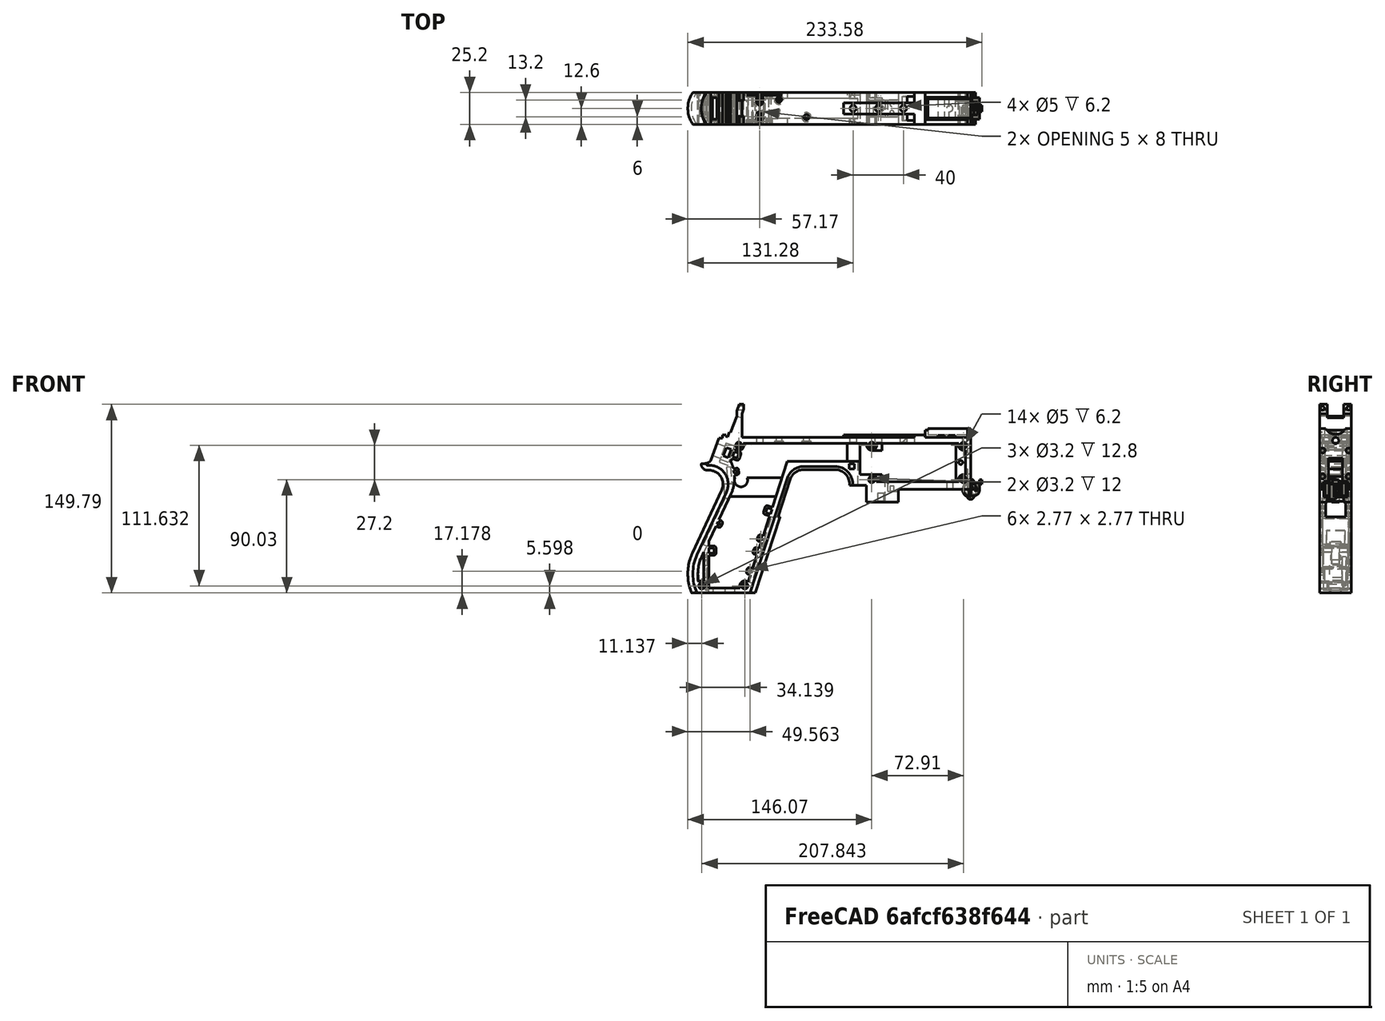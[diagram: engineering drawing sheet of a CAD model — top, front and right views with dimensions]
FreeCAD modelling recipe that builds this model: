
FCSTD DOCUMENT  (FreeCAD 1.0R39319 (Git))
Label: PICON-OF_ver_46
License: All rights reserved
LicenseURL: https://en.wikipedia.org/wiki/All_rights_reserved
objects: Sketcher::SketchObject×119, Part::Extrusion×62, Part::Cut×48, PartDesign::Pad×29, PartDesign::Pocket×18, PartDesign::Chamfer×15, PartDesign::Body×10, PartDesign::Fillet×6, Part::MultiFuse×4, PartDesign::SubtractivePipe×4, Part::Part2DObjectPython×4, PartDesign::SubtractiveLoft×4, PartDesign::Plane×2, PartDesign::SubShapeBinder×2, Part::Sweep×1, PartDesign::ShapeBinder×1, Mesh::Feature×1
note: 600 computed .brp shape members not serialized (recipe doc carries the construction recipe); baked Part::Feature solids carry a one-line shape summary decoded from their .brp

FEATURE [Sketcher::SketchObject] Sketch  label="corpo principale"
  ArcFitTolerance = 1e-06
  AttacherType = Attacher::AttachEngine3D
  AttachmentSupport = -> [XZ_Plane]
  FullyConstrained = true
  MakeInternals = false
  MapMode = 5
  Placement = pos=(0,0,0) rot=(1,0,0;1.5708rad)
  sketch-geometry (65):
    g0: LineSegment StartX=0 StartY=0 StartZ=0 EndX=-57.2 EndY=0 EndZ=0
    g1: LineSegment StartX=-57.2 StartY=0 StartZ=0 EndX=-57.2 EndY=-10.4 EndZ=0
    g2: LineSegment StartX=-57.2 StartY=-10.4 StartZ=0 EndX=-82.8 EndY=-10.4 EndZ=0
    g3: LineSegment StartX=-82.8 StartY=-10.4 StartZ=0 EndX=-82.8 EndY=3.2 EndZ=0
    g4: LineSegment StartX=-82.8 StartY=3.2 StartZ=0 EndX=-93.6 EndY=3.2 EndZ=0
    g5: LineSegment StartX=-93.6 StartY=3.2 StartZ=0 EndX=-93.6 EndY=4 EndZ=0
    g6: LineSegment StartX=-107.6 StartY=18 StartZ=0 EndX=-132.428 EndY=18 EndZ=0
    g7: LineSegment StartX=-145.743 StartY=8.32624 StartZ=0 EndX=-175.232 EndY=-82.4316 EndZ=0
    g8: LineSegment StartX=-175.232 StartY=-82.4316 StartZ=0 EndX=-217.232 EndY=-82.4316 EndZ=0
    g9: LineSegment StartX=-217.232 StartY=-52.1862 StartZ=0 EndX=-193.988 EndY=-2.33927 EndZ=0
    g10: LineSegment StartX=-206.196 StartY=23.0857 StartZ=0 EndX=-199.861 EndY=40.4914 EndZ=0
    g11: LineSegment StartX=-199.861 StartY=40.4914 StartZ=0 EndX=-197.061 EndY=40.4914 EndZ=0
    g12: LineSegment StartX=-197.061 StartY=40.4914 StartZ=0 EndX=-197.061 EndY=42.8914 EndZ=0
    g13: LineSegment StartX=-197.061 StartY=42.8914 StartZ=0 EndX=-194.261 EndY=42.8914 EndZ=0
    g14: LineSegment StartX=-194.261 StartY=42.8914 StartZ=0 EndX=-194.535 EndY=42.1397 EndZ=0
    g15: LineSegment StartX=-194.535 StartY=42.1397 StartZ=0 EndX=-193.031 EndY=41.5924 EndZ=0
    g16: LineSegment StartX=-193.031 StartY=41.5924 StartZ=0 EndX=-191.663 EndY=45.3512 EndZ=0
    g17: LineSegment StartX=-191.663 StartY=45.3512 StartZ=0 EndX=-190.536 EndY=44.9408 EndZ=0
    g18: LineSegment StartX=-190.536 StartY=44.9408 StartZ=0 EndX=-185.747 EndY=58.0965 EndZ=0
    g19: LineSegment StartX=-185.747 StartY=58.0965 StartZ=0 EndX=-185.747 EndY=62.0965 EndZ=0
    g20: LineSegment StartX=-185.747 StartY=62.0965 StartZ=0 EndX=-183.832 EndY=67.3588 EndZ=0
    g21: LineSegment StartX=-183.832 StartY=67.3588 StartZ=0 EndX=-180.232 EndY=67.3588 EndZ=0
    g22: LineSegment StartX=-180.232 StartY=67.3588 StartZ=0 EndX=-180.232 EndY=63.7588 EndZ=0
    g23: LineSegment StartX=-180.232 StartY=63.7588 StartZ=0 EndX=-181.6 EndY=60 EndZ=0
    g24: LineSegment StartX=-181.6 StartY=60 StartZ=0 EndX=-181.6 EndY=41.2 EndZ=0
    g25: LineSegment StartX=-181.6 StartY=41.2 StartZ=0 EndX=-100.8 EndY=41.2 EndZ=0
    g26: LineSegment StartX=-36 StartY=43.2 StartZ=0 EndX=-36 EndY=41.2 EndZ=0
    g27: LineSegment StartX=0 StartY=48 StartZ=0 EndX=0 EndY=0 EndZ=0
    g28: LineSegment StartX=-209.901 StartY=19.85 StartZ=0 EndX=-209.901 EndY=20.1 EndZ=0
    g29: LineSegment StartX=-208.001 StartY=22 StartZ=0 EndX=-207.747 EndY=22 EndZ=0
    g30: LineSegment StartX=-207.583 StartY=19 StartZ=0 EndX=-209.051 EndY=19 EndZ=0
    g31: ArcOfCircle CenterX=-208.001 CenterY=20.1 CenterZ=0 NormalX=0 NormalY=0 NormalZ=1 AngleXU=0 Radius=1.9 StartAngle=1.5708 EndAngle=3.14159
    g32: GeomPoint [constr] X=-209.901 Y=22 Z=0
    g33: ArcOfCircle CenterX=-209.051 CenterY=19.85 CenterZ=0 NormalX=0 NormalY=0 NormalZ=1 AngleXU=0 Radius=0.85 StartAngle=3.14159 EndAngle=4.71239
    g34: GeomPoint [constr] X=-209.901 Y=19 Z=0
    g35: ArcOfCircle CenterX=-207.747 CenterY=23.65 CenterZ=0 NormalX=0 NormalY=0 NormalZ=1 AngleXU=0 Radius=1.65 StartAngle=4.71239 EndAngle=5.93412
    g36: GeomPoint [constr] X=-206.591 Y=22 Z=0
    g37: LineSegment StartX=-4 StartY=6 StartZ=0 EndX=-4 EndY=36.4 EndZ=0
    g38: LineSegment StartX=-4 StartY=36.4 StartZ=0 EndX=-185.2 EndY=36.4 EndZ=0
    g39: LineSegment StartX=-185.2 StartY=36.4 StartZ=0 EndX=-190.441 EndY=22 EndZ=0
    g40: LineSegment StartX=-214.575 StartY=-78.4316 StartZ=0 EndX=-178.142 EndY=-78.4316 EndZ=0
    g41: LineSegment StartX=-178.142 StartY=-78.4316 StartZ=0 EndX=-145.51 EndY=22 EndZ=0
    g42: LineSegment StartX=-145.51 StartY=22 StartZ=0 EndX=-87.91 EndY=22 EndZ=0
    g43: LineSegment StartX=-87.91 StartY=22 StartZ=0 EndX=-87.91 EndY=11.6 EndZ=0
    g44: LineSegment StartX=-87.91 StartY=11.6 StartZ=0 EndX=-80.11 EndY=11.6 EndZ=0
    g45: LineSegment StartX=-80.11 StartY=11.6 StartZ=0 EndX=-80.11 EndY=6 EndZ=0
    g46: LineSegment StartX=-80.11 StartY=6 StartZ=0 EndX=-4 EndY=6 EndZ=0
    g47: LineSegment StartX=-190.363 StartY=-4.02975 StartZ=0 EndX=-213.607 EndY=-53.8767 EndZ=0
    g48: ArcOfCircle CenterX=-132.428 CenterY=4 CenterZ=0 NormalX=0 NormalY=0 NormalZ=1 AngleXU=0 Radius=14 StartAngle=1.5708 EndAngle=2.82743
    g49: GeomPoint [constr] X=-142.6 Y=18 Z=0
    g50: ArcOfCircle CenterX=-107.6 CenterY=4 CenterZ=0 NormalX=0 NormalY=0 NormalZ=1 AngleXU=0 Radius=14 StartAngle=0 EndAngle=1.5708
    g51: GeomPoint [constr] X=-93.6 Y=18 Z=0
    g52: ArcOfCircle CenterX=-184.801 CenterY=-67.3089 CenterZ=0 NormalX=0 NormalY=0 NormalZ=1 AngleXU=0 Radius=35.7833 StartAngle=2.70526 EndAngle=3.57792
    g53: ArcOfCircle CenterX=-207.583 CenterY=4 CenterZ=0 NormalX=0 NormalY=0 NormalZ=1 AngleXU=0 Radius=15 StartAngle=5.84685 EndAngle=7.85398
    g54: LineSegment [constr] StartX=-213.607 StartY=-53.8767 StartZ=0 EndX=-217.232 EndY=-52.1862 EndZ=0
    g55: ArcOfCircle CenterX=-184.801 CenterY=-67.3089 CenterZ=0 NormalX=0 NormalY=0 NormalZ=1 AngleXU=0 Radius=31.7833 StartAngle=2.70526 EndAngle=3.49911
    g56: ArcOfCircle CenterX=-218.095 CenterY=8.90192 CenterZ=0 NormalX=0 NormalY=0 NormalZ=1 AngleXU=0 Radius=30.5989 StartAngle=5.84685 EndAngle=6.72553
    g57: LineSegment StartX=-44.6 StartY=43.2 StartZ=0 EndX=-36 EndY=43.2 EndZ=0
    g58: LineSegment StartX=-100.8 StartY=41.2 StartZ=0 EndX=-44.6 EndY=41.2 EndZ=0
    g59: LineSegment StartX=-44.6 StartY=41.2 StartZ=0 EndX=-44.6 EndY=43.2 EndZ=0
    g60: LineSegment StartX=-2.4 StartY=48 StartZ=0 EndX=0 EndY=48 EndZ=0
    g61: LineSegment StartX=-36 StartY=41.2 StartZ=0 EndX=-2.4 EndY=41.2 EndZ=0
    g62: LineSegment StartX=-2.4 StartY=41.2 StartZ=0 EndX=-2.4 EndY=48 EndZ=0
    g63: LineSegment [constr] StartX=-181.6 StartY=36.4 StartZ=0 EndX=-152.209 EndY=36.4 EndZ=0
    g64: LineSegment [constr] StartX=-181.6 StartY=36.4 StartZ=0 EndX=-130.41 EndY=36.4 EndZ=0
  constraints (183):
    c: Coincident(g-1,g0)
    c: PointOnObject(g0,g-1)
    c: Coincident(g0,g1)
    c: Vertical(g1)
    c: Coincident(g1,g2)
    c: Horizontal(g2)
    c: Coincident(g2,g3)
    c: Vertical(g3)
    c: Coincident(g3,g4)
    c: Coincident(g4,g5)
    c: Vertical(g5)
    c: Horizontal(g6)
    c: Coincident(g7,g8)
    c: Horizontal(g8)
    c: Coincident(g10,g11)
    c: Horizontal(g11)
    c: Coincident(g11,g12)
    c: Vertical(g12)
    c: Coincident(g12,g13)
    c: Horizontal(g13)
    c: Coincident(g13,g14)
    c: Coincident(g14,g15)
    c: Coincident(g15,g16)
    c: Coincident(g16,g17)
    c: Coincident(g17,g18)
    c: Coincident(g18,g19)
    c: Vertical(g19)
    c: Coincident(g19,g20)
    c: Coincident(g20,g21)
    c: Horizontal(g21)
    c: Coincident(g21,g22)
    c: Vertical(g22)
    c: Coincident(g22,g23)
    c: Coincident(g23,g24)
    c: Vertical(g24)
    c: Coincident(g24,g25)
    c: Horizontal(g25)
    c: Coincident(g57,g26)
    c: Vertical(g26)
    c: Coincident(g26,g61)
    c: PointOnObject(g60,g-2)
    c: Coincident(g60,g27)
    c: Coincident(g27,g0)
    c: DistanceY(g27,g27) = 48
    c: DistanceY(g1,g1) = 10.4
    c: DistanceX(g0,g0) = 57.2
    c: DistanceX(g2,g2) = 25.6
    c: Horizontal(g4)
    c: DistanceY(g3,g3) = 13.6
    c: DistanceX(g4,g4) = 10.8
    c: DistanceY(g5,g51) = 14.8
    c: DistanceX(g49,g51) = 49
    c: Distance(g7,g49) = 105.6
    c: DistanceX(g61,g60) = 36
    c: DistanceX(g25,g25) = 80.8
    c: DistanceY(g24,g24) = 18.8
    c: DistanceY(g22,g22) = 3.6
    c: Distance(g23) = 4
    c: Angle(g-1,g23) = 1.22173
    c: DistanceX(g21,g21) = 3.6
    c: Distance(g20) = 5.6
    c: Angle(g-1,g20) = 1.22173
    c: DistanceY(g19,g19) = 4
    c: Distance(g18) = 14
    c: Angle(g-1,g18) = 1.22173
    c: Distance(g17) = 1.2
    c: Distance(g16) = 4
    c: Angle(g16) = 1.22173
    c: Perpendicular(g18,g17)
    c: Distance(g15) = 1.6
    c: Perpendicular(g16,g15)
    c: Distance(g14) = 0.8
    c: DistanceX(g13,g13) = 2.8
    c: Perpendicular(g15,g14)
    c: DistanceY(g12,g12) = 2.4
    c: DistanceX(g11,g11) = 2.8
    c: Distance(g9) = 55
    c: Angle(g9,g-1) = 2.00713
    c: Horizontal(g29)
    c: Vertical(g28)
    c: Horizontal(g30)
    c: PointOnObject(g32,g29)
    c: PointOnObject(g32,g28)
    c: Tangent(g29,g31) = 1.5708
    c: Tangent(g28,g31) = 1.5708
    c: PointOnObject(g34,g28)
    c: PointOnObject(g34,g30)
    c: Tangent(g28,g33) = 1.5708
    c: Tangent(g30,g33) = 1.5708
    c: PointOnObject(g36,g29)
    c: PointOnObject(g36,g10)
    c: Tangent(g29,g35) = -1.5708
    c: Tangent(g10,g35) = -1.5708
    c: Angle(g-1,g10) = 1.22173
    c: Radius(g35) = 1.65
    c: Vertical(g37)
    c: Coincident(g37,g38)
    c: Horizontal(g38)
    c: Coincident(g38,g39)
    c: Horizontal(g40)
    c: Coincident(g40,g41)
    c: Coincident(g41,g42)
    c: Horizontal(g42)
    c: Coincident(g42,g43)
    c: Vertical(g43)
    c: Coincident(g43,g44)
    c: Horizontal(g44)
    c: Coincident(g44,g45)
    c: Vertical(g45)
    c: Coincident(g45,g46)
    c: Coincident(g46,g37)
    c: Horizontal(g46)
    c: DistanceY(g0,g37) = 6
    c: DistanceX(g37,g0) = 4
    c: DistanceY(g37,g25) = 4.8
    c: DistanceX(g38,g38) = 181.2
    c: DistanceX(g42,g42) = 57.6
    c: DistanceY(g49,g41) = 4
    c: DistanceX(g41,g49) = 2.91
    c: DistanceY(g43,g43) = 10.4
    c: DistanceX(g44,g44) = 7.8
    c: DistanceY(g7,g40) = 4
    c: Distance(g47) = 55
    c: Angle(g-1,g39) = 1.22173
    c: PointOnObject(g49,g7)
    c: PointOnObject(g49,g6)
    c: Tangent(g7,g48) = -1.5708
    c: Tangent(g6,g48) = -1.5708
    c: PointOnObject(g51,g5)
    c: PointOnObject(g51,g6)
    c: Tangent(g5,g50) = -1.5708
    c: Tangent(g6,g50) = -1.5708
    c: Radius(g50) = 14
    c: Radius(g48) = 14
    c: DistanceX(g8,g8) = 42
    c: Angle(g7,g-1) = 1.88496
    c: Parallel(g41,g7)
    c: Parallel(g47,g9)
    c: Coincident(g52,g8)
    c: Tangent(g52,g9) = 1.5708
    c: DistanceX(g9,g8) = 0
    c: Tangent(g53,g9) = -1.5708
    c: Tangent(g53,g30) = -1.5708
    c: Diameter(g53) = 30
    c: DistanceY(g53,g0) = -4
    c: Coincident(g54,g47)
    c: Distance(g54) = 4
    c: Coincident(g54,g9)
    c: Coincident(g55,g40)
    c: Tangent(g55,g47) = -1.5708
    c: Coincident(g52,g55)
    c: Coincident(g56,g39)
    c: Tangent(g56,g47) = 1.5708
    c: Horizontal(g57)
    c: DistanceX(g57,g57) = 8.6
    c: Coincident(g58,g25)
    c: Horizontal(g58)
    c: Coincident(g59,g58)
    c: Vertical(g59)
    c: DistanceY(g58,g57) = 2
    c: DistanceX(g58,g58) = 56.2
    c: Coincident(g59,g57)
    c: DistanceY(g41,g36) = 0
    c: DistanceY(g36,g39) = 0
    c: DistanceY(g28,g28) = 0.25
    c: DistanceX(g30,g36) = 2.46
    c: DistanceX(g28,g29) = 1.9
    c: Coincident(g62,g60)
    c: Horizontal(g60)
    c: DistanceX(g62,g27) = 2.4
    c: Coincident(g61,g62)
    c: DistanceY(g26,g26) = 2
    c: Vertical(g62)
    c: DistanceY(g61,g60) = 6.8
    c: Horizontal(g61)
    c: Distance(g63) = 29.391
    c: PointOnObject(g63,g38)
    c: PointOnObject(g63,g38)
    c: Distance(g64) = 51.19
    c: PointOnObject(g64,g38)
    c: PointOnObject(g64,g38)
    c: DistanceX(g24,g63) = 0
    c: DistanceX(g24,g64) = 0
FEATURE [Part::Extrusion] Extrude  label="Extrude corpo principale"
  Base = -> Sketch
  Dir = (0,-1,2e-16)
  DirMode = 2
  FaceMakerClass = Part::FaceMakerBullseye
  FaceMakerMode = 3
  LengthFwd = 25.2
  LengthRev = 12.6
  Solid = true
  Symmetric = true
FEATURE [Sketcher::SketchObject] Sketch002  label="scavo grilletto"
  ArcFitTolerance = 1e-06
  AttachmentSupport = -> [XZ_Plane]
  ExternalGeometry = -> [Sketch]
  FullyConstrained = true
  MakeInternals = false
  MapMode = 5
  Placement = pos=(0,0,0) rot=(1,0,0;1.5708rad)
  sketch-geometry (4):
    g0: LineSegment StartX=-89.51 StartY=22 StartZ=0 EndX=-152.71 EndY=22 EndZ=0
    g1: LineSegment StartX=-152.71 StartY=22 StartZ=0 EndX=-167.006 EndY=-22 EndZ=0
    g2: LineSegment StartX=-167.006 StartY=-22 StartZ=0 EndX=-89.51 EndY=-22 EndZ=0
    g3: LineSegment StartX=-89.51 StartY=-22 StartZ=0 EndX=-89.51 EndY=22 EndZ=0
  constraints (12):
    c: Horizontal(g0)
    c: Coincident(g0,g1)
    c: Coincident(g1,g2)
    c: Horizontal(g2)
    c: Coincident(g2,g3)
    c: Coincident(g3,g0)
    c: Vertical(g3)
    c: Angle(g1,g0) = 1.88496
    c: DistanceY(g3,g3) = 44
    c: DistanceX(g0,g0) = 63.2
    c: DistanceX(g0,g-3) = 1.6
    c: DistanceY(g-3,g0) = 0
FEATURE [Sketcher::SketchObject] Sketch004  label="traiettoria arrotondamento impugnatura anteriore"
  ArcFitTolerance = 1e-06
  AttachmentSupport = -> [XZ_Plane]
  ExternalGeometry = -> [Sketch]
  FullyConstrained = true
  MakeInternals = false
  MapMode = 5
  Placement = pos=(0,0,0) rot=(1,0,0;1.5708rad)
  sketch-geometry (13):
    g0: LineSegment StartX=-175.232 StartY=-82.4316 StartZ=0 EndX=-145.743 EndY=8.32624 EndZ=0
    g1: LineSegment StartX=-93.6 StartY=3.2 StartZ=0 EndX=-93.6 EndY=4 EndZ=0
    g2: LineSegment StartX=-132.428 StartY=18 StartZ=0 EndX=-107.6 EndY=18 EndZ=0
    g3: ArcOfCircle CenterX=-132.428 CenterY=4 CenterZ=0 NormalX=0 NormalY=0 NormalZ=1 AngleXU=0 Radius=14 StartAngle=1.5708 EndAngle=2.82743
    g4: ArcOfCircle CenterX=-107.6 CenterY=4 CenterZ=0 NormalX=0 NormalY=0 NormalZ=1 AngleXU=0 Radius=14 StartAngle=0 EndAngle=1.5708
    g5: LineSegment StartX=-175.232 StartY=-82.4316 StartZ=0 EndX=-217.232 EndY=-82.4316 EndZ=0
    g6: LineSegment StartX=-217.232 StartY=-52.1862 StartZ=0 EndX=-193.988 EndY=-2.33927 EndZ=0
    g7: LineSegment StartX=-209.051 StartY=19 StartZ=0 EndX=-207.583 EndY=19 EndZ=0
    g8: LineSegment StartX=-209.901 StartY=20.1 StartZ=0 EndX=-209.901 EndY=19.85 EndZ=0
    g9: ArcOfCircle CenterX=-184.801 CenterY=-67.3089 CenterZ=0 NormalX=0 NormalY=0 NormalZ=1 AngleXU=0 Radius=35.7833 StartAngle=2.70526 EndAngle=3.57792
    g10: ArcOfCircle CenterX=-207.583 CenterY=4 CenterZ=0 NormalX=0 NormalY=0 NormalZ=1 AngleXU=0 Radius=15 StartAngle=5.84685 EndAngle=7.85398
    g11: ArcOfCircle CenterX=-209.051 CenterY=19.85 CenterZ=0 NormalX=0 NormalY=0 NormalZ=1 AngleXU=0 Radius=0.85 StartAngle=3.14159 EndAngle=4.71239
    g12: ArcOfCircle CenterX=-208.001 CenterY=20.1 CenterZ=0 NormalX=0 NormalY=0 NormalZ=1 AngleXU=0 Radius=1.9 StartAngle=1.5708 EndAngle=3.14159
  constraints (26):
    c: Coincident(g0,g-3)
    c: Coincident(g0,g-6)
    c: Coincident(g1,g-8)
    c: Coincident(g1,g-7)
    c: Coincident(g2,g-5)
    c: Coincident(g2,g-4)
    c: Coincident(g3,g2)
    c: Tangent(g3,g0) = 1.5708
    c: Coincident(g4,g1)
    c: Tangent(g4,g2) = 1.5708
    c: Coincident(g5,g0)
    c: Coincident(g5,g-9)
    c: Coincident(g6,g-12)
    c: Coincident(g6,g-11)
    c: Coincident(g7,g-15)
    c: Coincident(g7,g-14)
    c: Coincident(g8,g-16)
    c: Coincident(g8,g-17)
    c: Tangent(g9,g6) = 1.5708
    c: Coincident(g9,g5)
    c: Coincident(g10,g7)
    c: Tangent(g10,g6) = -1.5708
    c: Tangent(g11,g7) = -1.5708
    c: Coincident(g11,g8)
    c: Tangent(g12,g8) = -1.5708
    c: Coincident(g12,g-17)
FEATURE [PartDesign::Plane] DatumPlane  label="Piano per disegno arrotondamento impugnatura"
  AttachmentSupport = -> [Sketch]
  Length = 73.6581
  MapMode = 7
  Placement = pos=(-145.743,1.8e-15,8.32624) rot=(0.154555,0.154555,0.97582;1.59527rad)
  ResizeMode = 0
  Width = 303.511
FEATURE [Sketcher::SketchObject] Sketch005  label="forma arrotondamento impugnatura anteriore"
  ArcFitTolerance = 1e-06
  AttachmentSupport = -> [DatumPlane]
  FullyConstrained = true
  MakeInternals = false
  MapMode = 5
  Placement = pos=(-145.743,1.8e-15,8.32624) rot=(0.154555,0.154555,0.97582;1.59527rad)
  sketch-geometry (5):
    g0: GeomPoint [constr] X=0 Y=-4 Z=0
    g1: GeomPoint [constr] X=-12.6 Y=7.1e-15 Z=0
    g2: GeomPoint [constr] X=12.6 Y=4.97e-14 Z=0
    g3: LineSegment StartX=-12.6 StartY=7.1e-15 StartZ=0 EndX=12.6 EndY=4.97e-14 EndZ=0
    g4: ArcOfCircle CenterX=-3.88e-14 CenterY=17.845 CenterZ=0 NormalX=0 NormalY=0 NormalZ=1 AngleXU=0 Radius=21.845 StartAngle=4.09759 EndAngle=5.32718
  constraints (11):
    c: DistanceY(g0,g-1) = 4
    c: DistanceX(g-1,g0) = 0
    c: DistanceX(g1,g-1) = 12.6
    c: DistanceX(g-1,g2) = 12.6
    c: DistanceY(g-1,g2) = 0
    c: DistanceY(g-1,g1) = 0
    c: Coincident(g3,g1)
    c: Coincident(g3,g2)
    c: Coincident(g4,g1)
    c: Coincident(g4,g2)
    c: PointOnObject(g0,g4)
FEATURE [Part::Sweep] Sweep  label="Sweep impugnatura"
  Frenet = true
  Sections = -> [Sketch005]
  Solid = true
  Spine = -> Sketch [Edge32,Edge33,Edge34,Edge35,Edge36,Edge37,Edge38,Edge39,Edge40,Edge41,Edge42,Edge43,Edge44]
  Transition = 1
FEATURE [Sketcher::SketchObject] Sketch008  label="buchi e pulizie varie"
  ArcFitTolerance = 1e-06
  AttachmentSupport = -> [XZ_Plane]
  ExternalGeometry = -> [Sketch]
  FullyConstrained = true
  MakeInternals = false
  MapMode = 5
  Placement = pos=(0,0,0) rot=(1,0,0;1.5708rad)
  sketch-geometry (26):
    g0: LineSegment StartX=-96.278 StartY=20.155 StartZ=0 EndX=-92.278 EndY=20.155 EndZ=0
    g1: LineSegment StartX=-92.278 StartY=20.155 StartZ=0 EndX=-92.278 EndY=16.155 EndZ=0
    g2: LineSegment StartX=-92.278 StartY=16.155 StartZ=0 EndX=-96.278 EndY=16.155 EndZ=0
    g3: LineSegment StartX=-96.278 StartY=16.155 StartZ=0 EndX=-96.278 EndY=20.155 EndZ=0
    g4: LineSegment StartX=-222.232 StartY=-82.4316 StartZ=0 EndX=-170.232 EndY=-82.4316 EndZ=0
    g5: LineSegment StartX=-170.232 StartY=-82.4316 StartZ=0 EndX=-170.232 EndY=-86.4316 EndZ=0
    g6: LineSegment StartX=-170.232 StartY=-86.4316 StartZ=0 EndX=-222.232 EndY=-86.4316 EndZ=0
    g7: LineSegment StartX=-222.232 StartY=-86.4316 StartZ=0 EndX=-222.232 EndY=-82.4316 EndZ=0
    g8: LineSegment StartX=-213.901 StartY=20.1 StartZ=0 EndX=-213.901 EndY=26 EndZ=0
    g9: LineSegment StartX=-213.901 StartY=26 StartZ=0 EndX=-206.196 EndY=26 EndZ=0
    g10: LineSegment StartX=-17.4 StartY=42.8 StartZ=0 EndX=-12.4 EndY=42.8 EndZ=0
    g11: LineSegment StartX=-12.4 StartY=42.8 StartZ=0 EndX=-12.4 EndY=41.2 EndZ=0
    g12: LineSegment StartX=-12.4 StartY=41.2 StartZ=0 EndX=-17.4 EndY=41.2 EndZ=0
    g13: LineSegment StartX=-17.4 StartY=41.2 StartZ=0 EndX=-17.4 EndY=42.8 EndZ=0
    g14: LineSegment StartX=-25.9 StartY=42.8 StartZ=0 EndX=-20.9 EndY=42.8 EndZ=0
    g15: LineSegment StartX=-20.9 StartY=42.8 StartZ=0 EndX=-20.9 EndY=41.2 EndZ=0
    g16: LineSegment StartX=-20.9 StartY=41.2 StartZ=0 EndX=-25.9 EndY=41.2 EndZ=0
    g17: LineSegment StartX=-25.9 StartY=41.2 StartZ=0 EndX=-25.9 EndY=42.8 EndZ=0
    g18: GeomPoint [constr] X=-206.196 Y=23.0857 Z=0
    g19: GeomPoint [constr] X=-213.901 Y=20.1 Z=0
    g20: BSplineCurve PolesCount=4 KnotsCount=2 Degree=3 IsPeriodic=0
    g21-g24: Circle [constr] x4 (B-spline internal-alignment scaffolding for g20; pole/knot coordinates omitted)
    g25: LineSegment StartX=-206.196 StartY=26 StartZ=0 EndX=-206.196 EndY=23.0857 EndZ=0
  constraints (73):
    c: Horizontal(g0)
    c: Coincident(g1,g0)
    c: Vertical(g1)
    c: Coincident(g2,g1)
    c: Horizontal(g2)
    c: Coincident(g3,g2)
    c: Coincident(g3,g0)
    c: Vertical(g3)
    c: DistanceX(g0,g-4) = 4.368
    c: DistanceY(g0,g-4) = 1.845
    c: DistanceY(g1,g1) = 4
    c: DistanceX(g2,g2) = 4
    c: Horizontal(g4)
    c: Coincident(g5,g4)
    c: Vertical(g5)
    c: Coincident(g6,g5)
    c: Horizontal(g6)
    c: Coincident(g7,g6)
    c: Coincident(g7,g4)
    c: Vertical(g7)
    c: DistanceY(g7,g7) = 4
    c: DistanceX(g4,g-5) = 5
    c: DistanceX(g-5,g4) = 5
    c: DistanceY(g4,g-5) = 0
    c: Coincident(g9,g8)
    c: Parallel(g9,g-6)
    c: DistanceX(g8,g-8) = 4
    c: Horizontal(g10)
    c: Coincident(g11,g10)
    c: Vertical(g11)
    c: Coincident(g12,g11)
    c: Horizontal(g12)
    c: Coincident(g13,g12)
    c: Coincident(g13,g10)
    c: Vertical(g13)
    c: Horizontal(g14)
    c: Coincident(g15,g14)
    c: Vertical(g15)
    c: Coincident(g16,g15)
    c: Horizontal(g16)
    c: Coincident(g17,g16)
    c: Coincident(g17,g14)
    c: Vertical(g17)
    c: DistanceY(g11,g10) = 1.6
    c: DistanceX(g10,g10) = 5
    c: DistanceY(g15,g14) = 1.6
    c: DistanceX(g14,g14) = 5
    c: DistanceX(g15,g12) = 3.5
    c: DistanceX(g11,g-9) = 10
    c: DistanceY(g-9,g11) = 0
    c: DistanceY(g-9,g15) = 0
    c: Perpendicular(g8,g9)
    c: DistanceY(g-7,g9) = 4
    c: DistanceY(g8,g-8) = 0
    c: InternalAlignment(g18,g20)
    c: InternalAlignment(g19,g20)
    c: InternalAlignment(g21,g20)
    c: Weight(g21) = 1
    c: InternalAlignment(g22,g20)
    c: Equal(g22,g21)
    c: InternalAlignment(g23,g20)
    c: Equal(g23,g21)
    c: InternalAlignment(g24,g20)
    c: Equal(g24,g21)
    c: Coincident(g18,g-12)
    c: Coincident(g19,g8)
    c: Coincident(g25,g9)
    c: Coincident(g25,g20)
    c: Vertical(g25)
    c: DistanceY(g20,g23) = 0
    c: DistanceY(g22,g18) = 2.26
    c: DistanceX(g22,g18) = 0.93
    c: DistanceX(g20,g23) = 2.9
FEATURE [Part::Extrusion] Extrude004  label="Extrude Buchi e pulizie varie"
  Base = -> Sketch008
  Dir = (0,-1,2e-16)
  DirMode = 2
  FaceMakerClass = Part::FaceMakerBullseye
  FaceMakerMode = 3
  LengthFwd = 25.2
  LengthRev = 0
  Solid = true
  Symmetric = true
FEATURE [Sketcher::SketchObject] Sketch009  label="rinforzi"
  ArcFitTolerance = 1e-06
  AttachmentSupport = -> [XZ_Plane]
  ExternalGeometry = -> [Sketch]
  FullyConstrained = true
  MakeInternals = false
  MapMode = 5
  Placement = pos=(0,0,0) rot=(1,0,0;1.5708rad)
  sketch-geometry (9):
    g0: LineSegment StartX=-87.91 StartY=22 StartZ=0 EndX=-87.91 EndY=36.4 EndZ=0
    g1: LineSegment StartX=-87.91 StartY=36.4 StartZ=0 EndX=-97.91 EndY=36.4 EndZ=0
    g2: LineSegment StartX=-97.91 StartY=36.4 StartZ=0 EndX=-97.91 EndY=22 EndZ=0
    g3: LineSegment StartX=-97.91 StartY=22 StartZ=0 EndX=-87.91 EndY=22 EndZ=0
    g4: LineSegment StartX=-149.713 StartY=9.06563 StartZ=0 EndX=-154.586 EndY=-5.93437 EndZ=0
    g5: LineSegment StartX=-154.586 StartY=-5.93437 StartZ=0 EndX=-191.863 EndY=-5.93437 EndZ=0
    g6: LineSegment StartX=-191.863 StartY=-5.93437 StartZ=0 EndX=-191.863 EndY=9.06563 EndZ=0
    g7: LineSegment StartX=-191.863 StartY=9.06563 StartZ=0 EndX=-149.713 EndY=9.06563 EndZ=0
    g8: LineSegment [constr] StartX=-145.51 StartY=22 StartZ=0 EndX=-149.713 EndY=9.06563 EndZ=0
  constraints (25):
    c: Vertical(g0)
    c: Coincident(g1,g0)
    c: Horizontal(g1)
    c: Coincident(g2,g1)
    c: Vertical(g2)
    c: Coincident(g3,g2)
    c: Coincident(g3,g0)
    c: Horizontal(g3)
    c: Coincident(g0,g-4)
    c: DistanceX(g3,g3) = 10
    c: DistanceY(g0,g-3) = 0
    c: Coincident(g5,g4)
    c: Horizontal(g5)
    c: Coincident(g6,g5)
    c: Vertical(g6)
    c: Coincident(g7,g6)
    c: Coincident(g7,g4)
    c: Horizontal(g7)
    c: Distance(g8) = 13.6
    c: Parallel(g-6,g8)
    c: Coincident(g-6,g8)
    c: Parallel(g4,g-6)
    c: DistanceY(g4,g4) = 15
    c: Coincident(g4,g8)
    c: DistanceX(g-5,g5) = -1.5
FEATURE [Part::Extrusion] Extrude001  label="Extrude scavo grilletto"
  Base = -> Sketch002
  Dir = (0,-1,2e-16)
  DirMode = 2
  FaceMakerClass = Part::FaceMakerBullseye
  FaceMakerMode = 3
  LengthFwd = 16
  LengthRev = 0
  Solid = true
  Symmetric = true
FEATURE [Part::Extrusion] Extrude005  label="Extrude Rinforzi"
  Base = -> Sketch009
  Dir = (0,-1,2e-16)
  DirMode = 2
  FaceMakerClass = Part::FaceMakerBullseye
  FaceMakerMode = 3
  LengthFwd = 2
  LengthRev = 0
  Placement = pos=(0,12.6,0) rot=(0,0,1;0rad)
  Solid = true
  Symmetric = false
FEATURE [PartDesign::ShapeBinder] CopyCut
  TraceSupport = false
FEATURE [PartDesign::Plane] DatumPlane001
  AttachmentSupport = -> [CopyCut]
  Length = 283.944
  MapMode = 5
  Placement = pos=(0,12.6,0) rot=(0,0.707107,0.707107;3.14159rad)
  ResizeMode = 0
  Width = 188.15
FEATURE [Sketcher::SketchObject] Sketch010  label="buco neopixel"
  ArcFitTolerance = 1e-06
  AttachmentSupport = -> [XZ_Plane]
  ExternalGeometry = -> [Sketch]
  FullyConstrained = true
  MakeInternals = false
  MapMode = 5
  Placement = pos=(0,0,0) rot=(1,0,0;1.5708rad)
  sketch-geometry (5):
    g0: LineSegment [constr] StartX=-199.861 StartY=40.4914 StartZ=0 EndX=-201.368 EndY=36.3521 EndZ=0
    g1: LineSegment StartX=-201.368 StartY=36.3521 StartZ=0 EndX=-204.932 EndY=26.5605 EndZ=0
    g2: LineSegment StartX=-201.368 StartY=36.3521 StartZ=0 EndX=-180.2 EndY=28.6477 EndZ=0
    g3: LineSegment StartX=-180.2 StartY=28.6477 StartZ=0 EndX=-183.764 EndY=18.8561 EndZ=0
    g4: LineSegment StartX=-183.764 StartY=18.8561 StartZ=0 EndX=-204.932 EndY=26.5605 EndZ=0
  constraints (14):
    c: Parallel(g0,g-3)
    c: Distance(g0) = 4.405
    c: Coincident(g0,g-3)
    c: Coincident(g2,g1)
    c: Coincident(g3,g2)
    c: Coincident(g4,g3)
    c: Coincident(g4,g1)
    c: Parallel(g1,g-3)
    c: Distance(g1) = 10.42
    c: Coincident(g1,g0)
    c: Parallel(g2,g4)
    c: Perpendicular(g1,g2)
    c: DistanceX(g-4,g2) = 5
    c: Parallel(g3,g1)
FEATURE [Part::Extrusion] Extrude006  label="Extrude buco neopixel"
  Base = -> Sketch010
  Dir = (0,-1,2e-16)
  DirMode = 2
  FaceMakerClass = Part::FaceMakerBullseye
  FaceMakerMode = 3
  LengthFwd = 17.2
  LengthRev = 0
  Solid = true
  Symmetric = true
FEATURE [Sketcher::SketchObject] Sketch011  label="fermo grilletto"
  ArcFitTolerance = 1e-06
  AttachmentSupport = -> [XZ_Plane]
  ExternalGeometry = -> [Sketch]
  FullyConstrained = true
  MakeInternals = false
  MapMode = 5
  Placement = pos=(0,0,0) rot=(1,0,0;1.5708rad)
  sketch-geometry (18):
    g0: LineSegment [constr] StartX=-145.51 StartY=22 StartZ=0 EndX=-157.347 EndY=-14.4293 EndZ=0
    g1: LineSegment [constr] StartX=-157.347 StartY=-14.4293 StartZ=0 EndX=-157.841 EndY=-15.951 EndZ=0
    g2: LineSegment StartX=-161.151 StartY=-13.1932 StartZ=0 EndX=-155.825 EndY=-14.9237 EndZ=0
    g3: LineSegment StartX=-163.167 StartY=-14.2205 StartZ=0 EndX=-164.403 EndY=-18.0247 EndZ=0
    g4: LineSegment StartX=-163.376 StartY=-20.0408 StartZ=0 EndX=-158.05 EndY=-21.7713 EndZ=0
    g5: LineSegment StartX=-158.05 StartY=-21.7713 StartZ=0 EndX=-155.825 EndY=-14.9237 EndZ=0
    g6: LineSegment StartX=-161.645 StartY=-14.7149 StartZ=0 EndX=-157.841 EndY=-15.951 EndZ=0
    g7: LineSegment StartX=-157.841 StartY=-15.951 StartZ=0 EndX=-159.077 EndY=-19.7552 EndZ=0
    g8: LineSegment StartX=-159.077 StartY=-19.7552 StartZ=0 EndX=-162.881 EndY=-18.5191 EndZ=0
    g9: LineSegment StartX=-162.881 StartY=-18.5191 StartZ=0 EndX=-161.645 EndY=-14.7149 EndZ=0
    g10: LineSegment [constr] StartX=-161.645 StartY=-14.7149 StartZ=0 EndX=-161.151 EndY=-13.1932 EndZ=0
    g11: LineSegment [constr] StartX=-159.077 StartY=-19.7552 StartZ=0 EndX=-157.555 EndY=-20.2496 EndZ=0
    g12: LineSegment [constr] StartX=-159.077 StartY=-19.7552 StartZ=0 EndX=-159.572 EndY=-21.2769 EndZ=0
    g13: LineSegment [constr] StartX=-161.645 StartY=-14.7149 StartZ=0 EndX=-163.167 EndY=-14.2205 EndZ=0
    g14: ArcOfCircle CenterX=-161.645 CenterY=-14.7149 CenterZ=0 NormalX=0 NormalY=0 NormalZ=1 AngleXU=0 Radius=1.6 StartAngle=1.25664 EndAngle=2.82743
    g15: GeomPoint [constr] X=-162.673 Y=-12.6988 Z=0
    g16: ArcOfCircle CenterX=-162.881 CenterY=-18.5191 CenterZ=0 NormalX=0 NormalY=0 NormalZ=1 AngleXU=0 Radius=1.6 StartAngle=2.82743 EndAngle=4.39823
    g17: GeomPoint [constr] X=-164.897 Y=-19.5464 Z=0
  constraints (48):
    c: Parallel(g0,g-3)
    c: Distance(g0) = 38.304
    c: Coincident(g0,g-3)
    c: Parallel(g1,g-3)
    c: Distance(g1) = 1.6
    c: Coincident(g1,g0)
    c: Coincident(g5,g4)
    c: Coincident(g5,g2)
    c: Coincident(g7,g6)
    c: Coincident(g8,g7)
    c: Coincident(g9,g8)
    c: Coincident(g9,g6)
    c: Parallel(g7,g-3)
    c: Parallel(g9,g7)
    c: Perpendicular(g6,g7)
    c: Parallel(g6,g8)
    c: Distance(g6) = 4
    c: Distance(g9) = 4
    c: Parallel(g5,g7)
    c: Parallel(g9,g3)
    c: Parallel(g2,g6)
    c: Parallel(g4,g8)
    c: Parallel(g13,g6)
    c: Parallel(g10,g9)
    c: Parallel(g11,g8)
    c: Parallel(g12,g7)
    c: Distance(g10) = 1.6
    c: Distance(g13) = 1.6
    c: Distance(g12) = 1.6
    c: Distance(g11) = 1.6
    c: Coincident(g10,g6)
    c: Coincident(g13,g6)
    c: Coincident(g12,g7)
    c: Coincident(g11,g7)
    c: Distance(g10,g15) = 1.6
    c: Distance(g15,g13) = 1.6
    c: Distance(g4,g12) = 1.6
    c: Distance(g4,g11) = 1.6
    c: PointOnObject(g15,g2)
    c: Tangent(g3,g14) = -1.5708
    c: Tangent(g2,g14) = 1.5708
    c: PointOnObject(g17,g4)
    c: PointOnObject(g17,g3)
    c: Tangent(g4,g16) = -1.5708
    c: Tangent(g3,g16) = -1.5708
    c: Equal(g16,g14)
    c: Coincident(g16,g8)
    c: Coincident(g6,g1)
FEATURE [Part::Extrusion] Extrude007  label="Extrude fermo grilletto"
  Base = -> Sketch011
  Dir = (0,-1,2e-16)
  DirMode = 2
  FaceMakerClass = Part::FaceMakerBullseye
  FaceMakerMode = 3
  LengthFwd = 25.2
  LengthRev = 0
  Solid = true
  Symmetric = true
FEATURE [Sketcher::SketchObject] Sketch012  label="buco oled"
  ArcFitTolerance = 1e-06
  AttachmentSupport = -> [XZ_Plane]
  ExternalGeometry = -> [Sketch]
  FullyConstrained = true
  MakeInternals = false
  MapMode = 5
  Placement = pos=(0,0,0) rot=(1,0,0;1.5708rad)
  sketch-geometry (4):
    g0: LineSegment StartX=-185.747 StartY=58.0965 StartZ=0 EndX=-180.232 EndY=56.0891 EndZ=0
    g1: LineSegment StartX=-185.747 StartY=58.0965 StartZ=0 EndX=-185.747 EndY=67.3588 EndZ=0
    g2: LineSegment StartX=-185.747 StartY=67.3588 StartZ=0 EndX=-180.232 EndY=67.3588 EndZ=0
    g3: LineSegment StartX=-180.232 StartY=67.3588 StartZ=0 EndX=-180.232 EndY=56.0891 EndZ=0
  constraints (10):
    c: Coincident(g1,g0)
    c: Coincident(g2,g1)
    c: Coincident(g3,g2)
    c: Coincident(g3,g0)
    c: Parallel(g1,g-5)
    c: Perpendicular(g-3,g0)
    c: Parallel(g2,g-6)
    c: Parallel(g3,g-4)
    c: Coincident(g0,g-5)
    c: Coincident(g2,g-6)
FEATURE [Part::Extrusion] Extrude008  label="Extrude buco oled"
  Base = -> Sketch012
  Dir = (0,-1,2e-16)
  DirMode = 2
  FaceMakerClass = Part::FaceMakerBullseye
  FaceMakerMode = 3
  LengthFwd = 12.8
  LengthRev = 0
  Solid = true
  Symmetric = true
FEATURE [Sketcher::SketchObject] Sketch013  label="buco pompa"
  ArcFitTolerance = 1e-06
  AttachmentSupport = -> [XZ_Plane]
  ExternalGeometry = -> [Sketch]
  FullyConstrained = true
  MakeInternals = false
  MapMode = 5
  Placement = pos=(0,0,0) rot=(1,0,0;1.5708rad)
  sketch-geometry (8):
    g0: LineSegment StartX=-82.8 StartY=-10.4 StartZ=0 EndX=-82.8 EndY=-9.6 EndZ=0
    g1: LineSegment StartX=-82.8 StartY=-9.6 StartZ=0 EndX=-67.9 EndY=-9.6 EndZ=0
    g2: LineSegment StartX=-67.9 StartY=-9.6 StartZ=0 EndX=-67.9 EndY=6 EndZ=0
    g3: LineSegment StartX=-67.9 StartY=6 StartZ=0 EndX=-65.9 EndY=6 EndZ=0
    g4: LineSegment StartX=-65.9 StartY=6 StartZ=0 EndX=-65.9 EndY=-1.7 EndZ=0
    g5: LineSegment StartX=-65.9 StartY=-1.7 StartZ=0 EndX=-57.2 EndY=-1.7 EndZ=0
    g6: LineSegment StartX=-57.2 StartY=-1.7 StartZ=0 EndX=-57.2 EndY=-10.4 EndZ=0
    g7: LineSegment StartX=-57.2 StartY=-10.4 StartZ=0 EndX=-82.8 EndY=-10.4 EndZ=0
  constraints (22):
    c: Vertical(g0)
    c: Coincident(g1,g0)
    c: Horizontal(g1)
    c: Coincident(g2,g1)
    c: Vertical(g2)
    c: Coincident(g3,g2)
    c: Horizontal(g3)
    c: Coincident(g4,g3)
    c: Vertical(g4)
    c: Coincident(g5,g4)
    c: Horizontal(g5)
    c: Coincident(g6,g5)
    c: Vertical(g6)
    c: Coincident(g7,g6)
    c: Coincident(g7,g0)
    c: DistanceY(g0,g0) = 0.8
    c: DistanceY(g6,g6) = 8.7
    c: DistanceX(g1,g1) = 14.9
    c: DistanceX(g3,g3) = 2
    c: Coincident(g0,g-4)
    c: DistanceY(g2,g-6) = 0
    c: Coincident(g6,g-5)
FEATURE [Part::Extrusion] Extrude009  label="Extrude buco pompa"
  Base = -> Sketch013
  Dir = (0,-1,2e-16)
  DirMode = 2
  FaceMakerClass = Part::FaceMakerBullseye
  FaceMakerMode = 3
  LengthFwd = 13.2
  LengthRev = 0
  Solid = true
  Symmetric = true
FEATURE [Sketcher::SketchObject] Sketch014  label="buco frontale"
  ArcFitTolerance = 1e-06
  AttachmentSupport = -> [XZ_Plane]
  ExternalGeometry = -> [Sketch]
  FullyConstrained = true
  MakeInternals = false
  MapMode = 5
  Placement = pos=(0,0,0) rot=(1,0,0;1.5708rad)
  sketch-geometry (10):
    g0: LineSegment StartX=0 StartY=0 StartZ=0 EndX=0 EndY=24.671 EndZ=0
    g1: LineSegment StartX=0 StartY=24.671 StartZ=0 EndX=-4 EndY=24.671 EndZ=0
    g2: LineSegment StartX=-4 StartY=24.671 StartZ=0 EndX=-4 EndY=16 EndZ=0
    g3: LineSegment StartX=-4 StartY=16 StartZ=0 EndX=-2.4 EndY=16 EndZ=0
    g4: LineSegment StartX=-2.4 StartY=16 StartZ=0 EndX=-2.4 EndY=10 EndZ=0
    g5: LineSegment StartX=-2.4 StartY=10 StartZ=0 EndX=-12 EndY=10 EndZ=0
    g6: LineSegment StartX=-12 StartY=10 StartZ=0 EndX=-12 EndY=6 EndZ=0
    g7: LineSegment StartX=-12 StartY=6 StartZ=0 EndX=-2.4 EndY=6 EndZ=0
    g8: LineSegment StartX=-2.4 StartY=6 StartZ=0 EndX=-2.4 EndY=0 EndZ=0
    g9: LineSegment StartX=-2.4 StartY=0 StartZ=0 EndX=0 EndY=0 EndZ=0
  constraints (29):
    c: Vertical(g0)
    c: Coincident(g1,g0)
    c: Horizontal(g1)
    c: Coincident(g2,g1)
    c: Vertical(g2)
    c: Coincident(g3,g2)
    c: Horizontal(g3)
    c: Coincident(g4,g3)
    c: Vertical(g4)
    c: Coincident(g5,g4)
    c: Horizontal(g5)
    c: Coincident(g6,g5)
    c: Vertical(g6)
    c: Coincident(g7,g6)
    c: Coincident(g8,g7)
    c: Vertical(g8)
    c: Coincident(g9,g8)
    c: Coincident(g9,g0)
    c: Horizontal(g9)
    c: DistanceY(g0,g0) = 24.671
    c: Horizontal(g7)
    c: DistanceY(g6,g6) = 4
    c: DistanceY(g4,g4) = 6
    c: DistanceX(g9,g9) = 2.4
    c: Coincident(g0,g-1)
    c: DistanceY(g-3,g7) = 0
    c: DistanceX(g8,g4) = 0
    c: DistanceX(g-3,g1) = 0
    c: DistanceX(g6,g-3) = 8
FEATURE [Part::Extrusion] Extrude010  label="Extrude buco frontale"
  Base = -> Sketch014
  Dir = (0,-1,2e-16)
  DirMode = 2
  FaceMakerClass = Part::FaceMakerBullseye
  FaceMakerMode = 3
  LengthFwd = 11.2
  LengthRev = 0
  Solid = true
  Symmetric = true
FEATURE [Sketcher::SketchObject] Sketch015  label="guida rail"
  ArcFitTolerance = 1e-06
  AttachmentSupport = -> [XZ_Plane]
  ExternalGeometry = -> [Sketch]
  FullyConstrained = true
  MakeInternals = false
  MapMode = 5
  Placement = pos=(0,0,0) rot=(1,0,0;1.5708rad)
  sketch-geometry (4):
    g0: LineSegment StartX=-100.8 StartY=43.2 StartZ=0 EndX=-44.6 EndY=43.2 EndZ=0
    g1: LineSegment StartX=-44.6 StartY=43.2 StartZ=0 EndX=-44.6 EndY=41.2 EndZ=0
    g2: LineSegment StartX=-44.6 StartY=41.2 StartZ=0 EndX=-100.8 EndY=41.2 EndZ=0
    g3: LineSegment StartX=-100.8 StartY=41.2 StartZ=0 EndX=-100.8 EndY=43.2 EndZ=0
  constraints (9):
    c: Horizontal(g0)
    c: Coincident(g1,g0)
    c: Coincident(g2,g1)
    c: Coincident(g3,g2)
    c: Coincident(g3,g0)
    c: Vertical(g3)
    c: Coincident(g2,g-3)
    c: Coincident(g1,g-3)
    c: Coincident(g0,g-4)
FEATURE [Part::Extrusion] Extrude011  label="Extrude guida rail"
  Base = -> Sketch015
  Dir = (0,-1,2e-16)
  DirMode = 2
  FaceMakerClass = Part::FaceMakerBullseye
  FaceMakerMode = 3
  LengthFwd = 9
  LengthRev = 0
  Solid = true
  Symmetric = true
FEATURE [Sketcher::SketchObject] Sketch016  label="guide per coperture laterali"
  ArcFitTolerance = 1e-06
  AttachmentSupport = -> [XZ_Plane]
  ExternalGeometry = -> [Sketch]
  FullyConstrained = true
  MakeInternals = false
  MapMode = 5
  Placement = pos=(0,0,0) rot=(1,0,0;1.5708rad)
  sketch-geometry (14):
    g0: Circle CenterX=-5.6 CenterY=7.6 CenterZ=0 NormalX=0 NormalY=0 NormalZ=1 AngleXU=0 Radius=1.6
    g1: Circle CenterX=-5.6 CenterY=7.6 CenterZ=0 NormalX=0 NormalY=0 NormalZ=1 AngleXU=0 Radius=4
    g2: Circle CenterX=-5.6 CenterY=34.8 CenterZ=0 NormalX=0 NormalY=0 NormalZ=1 AngleXU=0 Radius=1.6
    g3: Circle CenterX=-5.6 CenterY=34.8 CenterZ=0 NormalX=0 NormalY=0 NormalZ=1 AngleXU=0 Radius=4
    g4: Circle CenterX=-184.08 CenterY=34.8 CenterZ=0 NormalX=0 NormalY=0 NormalZ=1 AngleXU=0 Radius=1.6
    g5: Circle CenterX=-184.08 CenterY=34.8 CenterZ=0 NormalX=0 NormalY=0 NormalZ=1 AngleXU=0 Radius=4
    g6: Circle CenterX=-179.305 CenterY=-76.8316 CenterZ=0 NormalX=0 NormalY=0 NormalZ=1 AngleXU=0 Radius=1.6
    g7: Circle CenterX=-179.305 CenterY=-76.8316 CenterZ=0 NormalX=0 NormalY=0 NormalZ=1 AngleXU=0 Radius=4
    g8: Circle CenterX=-213.443 CenterY=-76.8316 CenterZ=0 NormalX=0 NormalY=0 NormalZ=1 AngleXU=0 Radius=1.6
    g9: Circle CenterX=-213.443 CenterY=-76.8316 CenterZ=0 NormalX=0 NormalY=0 NormalZ=1 AngleXU=0 Radius=4
    g10: Circle CenterX=-78.51 CenterY=7.6 CenterZ=0 NormalX=0 NormalY=0 NormalZ=1 AngleXU=0 Radius=1.6
    g11: Circle CenterX=-78.51 CenterY=7.6 CenterZ=0 NormalX=0 NormalY=0 NormalZ=1 AngleXU=0 Radius=4
    g12: Circle CenterX=-78.51 CenterY=34.8 CenterZ=0 NormalX=0 NormalY=0 NormalZ=1 AngleXU=0 Radius=1.6
    g13: Circle CenterX=-78.51 CenterY=34.8 CenterZ=0 NormalX=0 NormalY=0 NormalZ=1 AngleXU=0 Radius=4
  constraints (35):
    c: Diameter(g0) = 3.2
    c: Diameter(g1) = 8
    c: Coincident(g0,g1)
    c: Diameter(g2) = 3.2
    c: Diameter(g3) = 8
    c: Coincident(g3,g2)
    c: Tangent(g2,g-7)
    c: Diameter(g4) = 3.2
    c: Diameter(g5) = 8
    c: Coincident(g5,g4)
    c: Tangent(g4,g-7)
    c: Tangent(g4,g-8)
    c: Diameter(g6) = 3.2
    c: Diameter(g7) = 8
    c: Coincident(g7,g6)
    c: Tangent(g6,g-9)
    c: Tangent(g6,g-10)
    c: Diameter(g8) = 3.2
    c: Diameter(g9) = 8
    c: Coincident(g9,g8)
    c: Tangent(g8,g-10)
    c: Tangent(g8,g-11)
    c: Diameter(g10) = 3.2
    c: Diameter(g11) = 8
    c: Diameter(g12) = 3.2
    c: Diameter(g13) = 8
    c: Coincident(g12,g13)
    c: Coincident(g10,g11)
    c: Tangent(g12,g-7)
    c: DistanceX(g12,g10) = 0
    c: Tangent(g2,g-6)
    c: Tangent(g0,g-6)
    c: Tangent(g0,g-3)
    c: Tangent(g10,g-3)
    c: Tangent(g10,g-4)
FEATURE [Part::Extrusion] Extrude012  label="extrude guide per coperture laterali"
  Base = -> Sketch016
  Dir = (0,-1,2e-16)
  DirMode = 2
  FaceMakerClass = Part::FaceMakerBullseye
  FaceMakerMode = 3
  LengthFwd = 25.2
  LengthRev = 0
  Solid = true
  Symmetric = true
FEATURE [Sketcher::SketchObject] Sketch017  label="supporto CAM"
  ArcFitTolerance = 1e-06
  AttachmentSupport = -> [XZ_Plane]
  ExternalGeometry = -> [Sketch]
  FullyConstrained = true
  MakeInternals = false
  MapMode = 5
  Placement = pos=(0,0,0) rot=(1,0,0;1.5708rad)
  sketch-geometry (6):
    g0: LineSegment StartX=-2.4 StartY=48 StartZ=0 EndX=-2.4 EndY=41.2 EndZ=0
    g1: LineSegment StartX=-2.4 StartY=48 StartZ=0 EndX=-34 EndY=48 EndZ=0
    g2: LineSegment StartX=-34 StartY=48 StartZ=0 EndX=-34 EndY=46.72 EndZ=0
    g3: LineSegment StartX=-34 StartY=46.72 StartZ=0 EndX=-36 EndY=46.72 EndZ=0
    g4: LineSegment StartX=-36 StartY=46.72 StartZ=0 EndX=-36 EndY=41.2 EndZ=0
    g5: LineSegment StartX=-36 StartY=41.2 StartZ=0 EndX=-2.4 EndY=41.2 EndZ=0
  constraints (15):
    c: Coincident(g1,g0)
    c: Horizontal(g1)
    c: Coincident(g2,g1)
    c: Vertical(g2)
    c: Coincident(g3,g2)
    c: Horizontal(g3)
    c: Coincident(g4,g3)
    c: Coincident(g5,g4)
    c: DistanceX(g1,g0) = 31.6
    c: Coincident(g5,g0)
    c: Vertical(g4)
    c: DistanceY(g2,g1) = 1.28
    c: Coincident(g0,g-3)
    c: Coincident(g0,g-3)
    c: Coincident(g4,g-4)
FEATURE [Part::Extrusion] Extrude013  label="Extrude supporto CAM"
  Base = -> Sketch017
  Dir = (0,-1,2e-16)
  DirMode = 2
  FaceMakerClass = Part::FaceMakerBullseye
  FaceMakerMode = 3
  LengthFwd = 17.8
  LengthRev = 0
  Solid = true
  Symmetric = true
FEATURE [Sketcher::SketchObject] Sketch018  label="Scavo CAM"
  ArcFitTolerance = 1e-06
  AttachmentSupport = -> [YZ_Plane]
  ExternalGeometry = -> [Sketch]
  FullyConstrained = true
  MakeInternals = false
  MapMode = 5
  Placement = pos=(0,0,0) rot=(0.57735,0.57735,0.57735;2.0944rad)
  sketch-geometry (4):
    g0: LineSegment StartX=-7.73 StartY=48 StartZ=0 EndX=7.73 EndY=48 EndZ=0
    g1: LineSegment [constr] StartX=1.07e-14 StartY=48 StartZ=0 EndX=0 EndY=43.5155 EndZ=0
    g2: ArcOfCircle CenterX=9e-15 CenterY=52.42 CenterZ=0 NormalX=0 NormalY=0 NormalZ=1 AngleXU=0 Radius=8.90445 StartAngle=3.66102 EndAngle=5.76376
    g3: Circle [constr] CenterX=9e-15 CenterY=52.42 CenterZ=0 NormalX=0 NormalY=0 NormalZ=1 AngleXU=0 Radius=8.9
  constraints (13):
    c: Horizontal(g0)
    c: DistanceY(g-3,g0) = 0
    c: DistanceX(g0,g0) = 15.46
    c: DistanceX(g0,g-3) = 7.73
    c: DistanceX(g-3) = 0
    c: Coincident(g1,g-3)
    c: PointOnObject(g1,g-2)
    c: Coincident(g2,g0)
    c: Coincident(g2,g0)
    c: PointOnObject(g1,g2)
    c: Diameter(g3) = 17.8
    c: DistanceY(g1,g3) = 4.42
    c: Coincident(g2,g3)
FEATURE [Part::Extrusion] Extrude014  label="Extrude Scavo CAM"
  Base = -> Sketch018
  Dir = (1,0,0)
  DirMode = 2
  FaceMakerClass = Part::FaceMakerBullseye
  FaceMakerMode = 3
  LengthFwd = -34
  LengthRev = 0
  Solid = true
  Symmetric = false
FEATURE [Sketcher::SketchObject] Sketch019  label="scavo rumble"
  ArcFitTolerance = 1e-06
  AttachmentSupport = -> [XZ_Plane]
  ExternalGeometry = -> [Sketch]
  FullyConstrained = true
  MakeInternals = false
  MapMode = 5
  Placement = pos=(0,0,0) rot=(1,0,0;1.5708rad)
  sketch-geometry (6):
    g0: LineSegment StartX=-163.771 StartY=-21.9058 StartZ=0 EndX=-158.636 EndY=-23.5745 EndZ=0
    g1: LineSegment StartX=-158.636 StartY=-23.5745 StartZ=0 EndX=-165.743 EndY=-45.4488 EndZ=0
    g2: LineSegment StartX=-165.743 StartY=-45.4488 StartZ=0 EndX=-170.879 EndY=-43.7801 EndZ=0
    g3: LineSegment StartX=-170.879 StartY=-43.7801 StartZ=0 EndX=-163.771 EndY=-21.9058 EndZ=0
    g4: LineSegment [constr] StartX=-145.51 StartY=22 StartZ=0 EndX=-160.157 EndY=-23.0801 EndZ=0
    g5: LineSegment [constr] StartX=-158.636 StartY=-23.5745 StartZ=0 EndX=-160.157 EndY=-23.0801 EndZ=0
  constraints (17):
    c: Coincident(g1,g0)
    c: Coincident(g2,g1)
    c: Coincident(g3,g2)
    c: Coincident(g3,g0)
    c: Parallel(g3,g-3)
    c: Parallel(g3,g1)
    c: Perpendicular(g3,g0)
    c: Perpendicular(g2,g3)
    c: Distance(g2,g0) = 23
    c: Parallel(g4,g-3)
    c: Distance(g4) = 47.4
    c: Coincident(g4,g-3)
    c: Parallel(g5,g0)
    c: Distance(g5) = 1.6
    c: Coincident(g5,g0)
    c: Distance(g5,g0) = 3.8
    c: Coincident(g5,g4)
FEATURE [Part::Extrusion] Extrude015  label="scavo rumble001"
  Base = -> Sketch019
  Dir = (0,-1,2e-16)
  DirMode = 2
  FaceMakerClass = Part::FaceMakerBullseye
  FaceMakerMode = 3
  LengthFwd = 21
  LengthRev = 0
  Solid = true
  Symmetric = true
FEATURE [Sketcher::SketchObject] Sketch020  label="fermo rumble"
  ArcFitTolerance = 1e-06
  AttachmentSupport = -> [XZ_Plane]
  ExternalGeometry = -> [Sketch019,Sketch]
  FullyConstrained = true
  MakeInternals = false
  MapMode = 5
  Placement = pos=(0,0,0) rot=(1,0,0;1.5708rad)
  sketch-geometry (16):
    g0: LineSegment [constr] StartX=-165.905 StartY=-40.7697 StartZ=0 EndX=-167.265 EndY=-44.9544 EndZ=0
    g1: LineSegment [constr] StartX=-167.265 StartY=-44.9544 StartZ=0 EndX=-165.743 EndY=-45.4488 EndZ=0
    g2: LineSegment StartX=-167.318 StartY=-37.9976 StartZ=0 EndX=-165.225 EndY=-38.6774 EndZ=0
    g3: LineSegment StartX=-165.225 StartY=-38.6774 StartZ=0 EndX=-165.905 EndY=-40.7697 EndZ=0
    g4: LineSegment StartX=-165.905 StartY=-40.7697 StartZ=0 EndX=-167.997 EndY=-40.0899 EndZ=0
    g5: LineSegment StartX=-167.997 StartY=-40.0899 StartZ=0 EndX=-167.318 EndY=-37.9976 EndZ=0
    g6: LineSegment StartX=-166.823 StartY=-36.4759 StartZ=0 EndX=-163.399 EndY=-37.5883 EndZ=0
    g7: LineSegment StartX=-163.399 StartY=-37.5883 StartZ=0 EndX=-165.006 EndY=-42.5338 EndZ=0
    g8: LineSegment StartX=-165.006 StartY=-42.5338 StartZ=0 EndX=-168.43 EndY=-41.4214 EndZ=0
    g9: LineSegment StartX=-169.457 StartY=-39.4053 StartZ=0 EndX=-168.839 EndY=-37.5031 EndZ=0
    g10: LineSegment [constr] StartX=-168.839 StartY=-37.5031 StartZ=0 EndX=-168.345 EndY=-35.9815 EndZ=0
    g11: LineSegment [constr] StartX=-168.345 StartY=-35.9815 StartZ=0 EndX=-166.823 EndY=-36.4759 EndZ=0
    g12: ArcOfCircle CenterX=-167.936 CenterY=-39.8997 CenterZ=0 NormalX=0 NormalY=0 NormalZ=1 AngleXU=0 Radius=1.6 StartAngle=2.82743 EndAngle=4.39823
    g13: GeomPoint [constr] X=-169.952 Y=-40.9269 Z=0
    g14: ArcOfCircle CenterX=-167.318 CenterY=-37.9976 CenterZ=0 NormalX=0 NormalY=0 NormalZ=1 AngleXU=0 Radius=1.6 StartAngle=1.25664 EndAngle=2.82743
    g15: GeomPoint [constr] X=-168.345 Y=-35.9815 Z=0
  constraints (42):
    c: Parallel(g0,g-4)
    c: Distance(g0) = 4.4
    c: Coincident(g1,g0)
    c: Perpendicular(g0,g1)
    c: Distance(g1) = 1.6
    c: Coincident(g1,g-5)
    c: Coincident(g3,g2)
    c: Coincident(g4,g3)
    c: Coincident(g5,g4)
    c: Coincident(g5,g2)
    c: Parallel(g3,g-4)
    c: Parallel(g3,g5)
    c: Perpendicular(g2,g3)
    c: Parallel(g4,g2)
    c: Distance(g2) = 2.2
    c: Distance(g3) = 2.2
    c: Coincident(g7,g6)
    c: Coincident(g8,g7)
    c: Parallel(g7,g-4)
    c: Parallel(g7,g9)
    c: Perpendicular(g6,g7)
    c: Parallel(g6,g8)
    c: Distance(g6,g15) = 5.2
    c: Distance(g7) = 5.2
    c: Coincident(g11,g10)
    c: Parallel(g10,g9)
    c: Parallel(g11,g6)
    c: Distance(g10) = 1.6
    c: Distance(g11) = 1.6
    c: Coincident(g10,g15)
    c: Distance(g11,g2) = 1.6
    c: Distance(g2,g10) = 1.6
    c: PointOnObject(g13,g8)
    c: PointOnObject(g13,g9)
    c: Tangent(g8,g12) = 1.5708
    c: Tangent(g9,g12) = 1.5708
    c: PointOnObject(g15,g9)
    c: Tangent(g6,g14) = 1.5708
    c: Tangent(g9,g14) = 1.5708
    c: Equal(g12,g14)
    c: Coincident(g6,g11)
    c: Coincident(g3,g0)
FEATURE [Part::Extrusion] Extrude016  label="Extrude fermo rumble"
  Base = -> Sketch020
  Dir = (0,-1,2e-16)
  DirMode = 2
  FaceMakerClass = Part::FaceMakerBullseye
  FaceMakerMode = 3
  LengthFwd = 25.2
  LengthRev = 0
  Solid = true
  Symmetric = true
FEATURE [Sketcher::SketchObject] Sketch021  label="perno fermo rumble001"
  ArcFitTolerance = 1e-06
  AttachmentSupport = -> [XZ_Plane001]
  FullyConstrained = true
  MakeInternals = false
  MapMode = 5
  Placement = pos=(0,0,0) rot=(1,0,0;1.5708rad)
  sketch-geometry (16):
    g0: LineSegment StartX=0 StartY=0.45 StartZ=0 EndX=0 EndY=1.55 EndZ=0
    g1: LineSegment StartX=0.45 StartY=2 StartZ=0 EndX=1.55 EndY=2 EndZ=0
    g2: LineSegment StartX=2 StartY=1.55 StartZ=0 EndX=2 EndY=0.45 EndZ=0
    g3: LineSegment StartX=1.55 StartY=0 StartZ=0 EndX=0.45 EndY=0 EndZ=0
    g4: ArcOfCircle [constr] CenterX=0.45 CenterY=1.55 CenterZ=0 NormalX=0 NormalY=0 NormalZ=1 AngleXU=0 Radius=0.45 StartAngle=1.5708 EndAngle=3.14159
    g5: GeomPoint [constr] X=0 Y=2 Z=0
    g6: LineSegment StartX=0.45 StartY=2 StartZ=0 EndX=0 EndY=1.55 EndZ=0
    g7: ArcOfCircle [constr] CenterX=1.55 CenterY=1.55 CenterZ=0 NormalX=0 NormalY=0 NormalZ=1 AngleXU=0 Radius=0.45 StartAngle=0 EndAngle=1.5708
    g8: GeomPoint [constr] X=2 Y=2 Z=0
    g9: LineSegment StartX=2 StartY=1.55 StartZ=0 EndX=1.55 EndY=2 EndZ=0
    g10: ArcOfCircle [constr] CenterX=1.55 CenterY=0.45 CenterZ=0 NormalX=0 NormalY=0 NormalZ=1 AngleXU=0 Radius=0.45 StartAngle=4.71239 EndAngle=6.28319
    g11: GeomPoint [constr] X=2 Y=0 Z=0
    g12: LineSegment StartX=1.55 StartY=0 StartZ=0 EndX=2 EndY=0.45 EndZ=0
    g13: ArcOfCircle [constr] CenterX=0.45 CenterY=0.45 CenterZ=0 NormalX=0 NormalY=0 NormalZ=1 AngleXU=0 Radius=0.45 StartAngle=3.14159 EndAngle=4.71239
    g14: GeomPoint [constr] X=0 Y=0 Z=0
    g15: LineSegment StartX=0 StartY=0.45 StartZ=0 EndX=0.45 EndY=0 EndZ=0
  constraints (35):
    c: Coincident(g14,g-1)
    c: PointOnObject(g5,g-2)
    c: Horizontal(g1)
    c: Vertical(g2)
    c: Horizontal(g3)
    c: DistanceX(g5,g8) = 2
    c: DistanceY(g11,g8) = 2
    c: PointOnObject(g5,g0)
    c: PointOnObject(g5,g1)
    c: Tangent(g0,g4) = 1.5708
    c: Tangent(g1,g4) = 1.5708
    c: Coincident(g6,g0)
    c: Coincident(g6,g1)
    c: PointOnObject(g8,g2)
    c: PointOnObject(g8,g1)
    c: Tangent(g2,g7) = 1.5708
    c: Tangent(g1,g7) = 1.5708
    c: Coincident(g9,g2)
    c: Coincident(g9,g1)
    c: PointOnObject(g11,g2)
    c: PointOnObject(g11,g3)
    c: Tangent(g2,g10) = 1.5708
    c: Tangent(g3,g10) = 1.5708
    c: Coincident(g12,g2)
    c: Coincident(g12,g3)
    c: PointOnObject(g14,g0)
    c: PointOnObject(g14,g3)
    c: Tangent(g0,g13) = 1.5708
    c: Tangent(g3,g13) = 1.5708
    c: Coincident(g15,g0)
    c: Coincident(g15,g3)
    c: Equal(g6,g9)
    c: Equal(g9,g12)
    c: Equal(g12,g15)
    c: DistanceX(g14,g3) = 0.45
FEATURE [Sketcher::SketchObject] Sketch022  label="fori per M3x5(OD)x6(L)"
  ArcFitTolerance = 1e-06
  AttachmentSupport = -> [XZ_Plane]
  ExternalGeometry = -> [Sketch016]
  FullyConstrained = true
  MakeInternals = false
  MapMode = 5
  Placement = pos=(0,0,0) rot=(1,0,0;1.5708rad)
  sketch-geometry (7):
    g0: Circle CenterX=-5.6 CenterY=34.8 CenterZ=0 NormalX=0 NormalY=0 NormalZ=1 AngleXU=0 Radius=2.5
    g1: Circle CenterX=-5.6 CenterY=7.6 CenterZ=0 NormalX=0 NormalY=0 NormalZ=1 AngleXU=0 Radius=2.5
    g2: Circle CenterX=-78.51 CenterY=34.8 CenterZ=0 NormalX=0 NormalY=0 NormalZ=1 AngleXU=0 Radius=2.5
    g3: Circle CenterX=-78.51 CenterY=7.6 CenterZ=0 NormalX=0 NormalY=0 NormalZ=1 AngleXU=0 Radius=2.5
    g4: Circle CenterX=-184.08 CenterY=34.8 CenterZ=0 NormalX=0 NormalY=0 NormalZ=1 AngleXU=0 Radius=2.5
    g5: Circle CenterX=-179.305 CenterY=-76.8316 CenterZ=0 NormalX=0 NormalY=0 NormalZ=1 AngleXU=0 Radius=2.5
    g6: Circle CenterX=-213.443 CenterY=-76.8316 CenterZ=0 NormalX=0 NormalY=0 NormalZ=1 AngleXU=0 Radius=2.5
  constraints (14):
    c: Diameter(g0) = 5
    c: Diameter(g1) = 5
    c: Diameter(g2) = 5
    c: Diameter(g3) = 5
    c: Diameter(g4) = 5
    c: Diameter(g5) = 5
    c: Diameter(g6) = 5
    c: Coincident(g0,g-8)
    c: Coincident(g1,g-9)
    c: Coincident(g2,g-6)
    c: Coincident(g3,g-7)
    c: Coincident(g4,g-5)
    c: Coincident(g5,g-4)
    c: Coincident(g6,g-3)
FEATURE [Part::Extrusion] Extrude018  label="Extrude fori M3x5x6 - dx"
  Base = -> Sketch022
  Dir = (0,-1,2e-16)
  DirMode = 2
  FaceMakerClass = Part::FaceMakerBullseye
  FaceMakerMode = 3
  LengthFwd = 6.2
  LengthRev = 0
  Placement = pos=(0,-9.5,0) rot=(0,0,1;0rad)
  Solid = true
  Symmetric = true
FEATURE [Part::Extrusion] Extrude019  label="Extrude fori M3x5x6 - sx"
  Base = -> Sketch022
  Dir = (0,-1,2e-16)
  DirMode = 2
  FaceMakerClass = Part::FaceMakerBullseye
  FaceMakerMode = 3
  LengthFwd = 6.2
  LengthRev = 0
  Placement = pos=(0,9.5,0) rot=(0,0,1;0rad)
  Solid = true
  Symmetric = true
FEATURE [Sketcher::SketchObject] Sketch023  label="foro anteriore M3x5x6"
  ArcFitTolerance = 1e-06
  AttachmentSupport = -> [YZ_Plane]
  FullyConstrained = true
  MakeInternals = false
  MapMode = 5
  Placement = pos=(0,0,0) rot=(0.57735,0.57735,0.57735;2.0944rad)
  sketch-geometry (2):
    g0: LineSegment [constr] StartX=0 StartY=0 StartZ=0 EndX=0 EndY=38.6 EndZ=0
    g1: Circle CenterX=0 CenterY=38.6 CenterZ=0 NormalX=0 NormalY=0 NormalZ=1 AngleXU=0 Radius=2.5
  constraints (5):
    c: Coincident(g0,g-1)
    c: PointOnObject(g0,g-2)
    c: DistanceY(g0,g0) = 38.6
    c: Diameter(g1) = 5
    c: Coincident(g1,g0)
FEATURE [Part::Extrusion] Extrude020  label="Extrude foro anteriore M3x5x6"
  Base = -> Sketch023
  Dir = (1,0,0)
  DirMode = 2
  FaceMakerClass = Part::FaceMakerBullseye
  FaceMakerMode = 3
  LengthFwd = -6.2
  LengthRev = 0
  Solid = true
  Symmetric = false
FEATURE [Sketcher::SketchObject] Sketch024  label="fori per viti frontale"
  ArcFitTolerance = 1e-06
  AttachmentSupport = -> [YZ_Plane]
  FullyConstrained = true
  MakeInternals = false
  MapMode = 5
  Placement = pos=(0,0,0) rot=(0.57735,0.57735,0.57735;2.0944rad)
  sketch-geometry (9):
    g0: LineSegment [constr] StartX=-10.3 StartY=30.721 StartZ=0 EndX=10.3 EndY=30.721 EndZ=0
    g1: LineSegment [constr] StartX=10.3 StartY=30.721 StartZ=0 EndX=10.3 EndY=10.121 EndZ=0
    g2: LineSegment [constr] StartX=10.3 StartY=10.121 StartZ=0 EndX=-10.3 EndY=10.121 EndZ=0
    g3: LineSegment [constr] StartX=-10.3 StartY=10.121 StartZ=0 EndX=-10.3 EndY=30.721 EndZ=0
    g4: LineSegment [constr] StartX=0 StartY=0 StartZ=0 EndX=0 EndY=10.121 EndZ=0
    g5: Circle CenterX=-10.3 CenterY=30.721 CenterZ=0 NormalX=0 NormalY=0 NormalZ=1 AngleXU=0 Radius=2
    g6: Circle CenterX=10.3 CenterY=30.721 CenterZ=0 NormalX=0 NormalY=0 NormalZ=1 AngleXU=0 Radius=2
    g7: Circle CenterX=-10.3 CenterY=10.121 CenterZ=0 NormalX=0 NormalY=0 NormalZ=1 AngleXU=0 Radius=2
    g8: Circle CenterX=10.3 CenterY=10.121 CenterZ=0 NormalX=0 NormalY=0 NormalZ=1 AngleXU=0 Radius=2
  constraints (22):
    c: Horizontal(g0)
    c: Coincident(g1,g0)
    c: Vertical(g1)
    c: Coincident(g2,g1)
    c: Horizontal(g2)
    c: Coincident(g3,g2)
    c: Coincident(g3,g0)
    c: Vertical(g3)
    c: DistanceX(g0,g0) = 20.6
    c: DistanceY(g3,g3) = 20.6
    c: Coincident(g4,g-1)
    c: PointOnObject(g4,g-2)
    c: DistanceY(g4,g4) = 10.121
    c: Symmetric(g2,g2,g4)
    c: Diameter(g5) = 4
    c: Diameter(g6) = 4
    c: Diameter(g7) = 4
    c: Diameter(g8) = 4
    c: Coincident(g5,g0)
    c: Coincident(g6,g0)
    c: Coincident(g7,g2)
    c: Coincident(g8,g1)
FEATURE [Part::Extrusion] Extrude021  label="Extrude fori per viti frontale"
  Base = -> Sketch024
  Dir = (1,0,0)
  DirMode = 2
  FaceMakerClass = Part::FaceMakerBullseye
  FaceMakerMode = 3
  LengthFwd = -2.4
  LengthRev = 0
  Solid = true
  Symmetric = false
FEATURE [Sketcher::SketchObject] Sketch025  label="foro per filo CAM"
  ArcFitTolerance = 1e-06
  AttachmentSupport = -> [XZ_Plane]
  ExternalGeometry = -> [Sketch]
  FullyConstrained = true
  MakeInternals = false
  MapMode = 5
  Placement = pos=(0,0,0) rot=(1,0,0;1.5708rad)
  sketch-geometry (4):
    g0: LineSegment StartX=-44.6 StartY=41.2 StartZ=0 EndX=-44.6 EndY=36.4 EndZ=0
    g1: LineSegment StartX=-44.6 StartY=36.4 StartZ=0 EndX=-54.6 EndY=36.4 EndZ=0
    g2: LineSegment StartX=-54.6 StartY=36.4 StartZ=0 EndX=-50.4 EndY=41.2 EndZ=0
    g3: LineSegment StartX=-50.4 StartY=41.2 StartZ=0 EndX=-44.6 EndY=41.2 EndZ=0
  constraints (11):
    c: Vertical(g0)
    c: Coincident(g1,g0)
    c: Horizontal(g1)
    c: Coincident(g2,g1)
    c: Coincident(g3,g2)
    c: Coincident(g3,g0)
    c: Horizontal(g3)
    c: Coincident(g0,g-3)
    c: DistanceY(g0,g-4) = 0
    c: DistanceX(g3,g3) = 5.8
    c: DistanceX(g1,g1) = 10
FEATURE [Part::Extrusion] Extrude022  label="Extrude foro per filo CAM dx"
  Base = -> Sketch025
  Dir = (0,-1,2e-16)
  DirMode = 2
  FaceMakerClass = Part::FaceMakerBullseye
  FaceMakerMode = 3
  LengthFwd = 4.9
  LengthRev = 0
  Placement = pos=(0,6.95,0) rot=(0,0,1;0rad)
  Solid = true
  Symmetric = true
FEATURE [Part::Extrusion] Extrude023  label="Extrude foro per filo CAM sx"
  Base = -> Sketch025
  Dir = (0,-1,2e-16)
  DirMode = 2
  FaceMakerClass = Part::FaceMakerBullseye
  FaceMakerMode = 3
  LengthFwd = 4.9
  LengthRev = 0
  Placement = pos=(0,-6.95,0) rot=(0,0,1;0rad)
  Solid = true
  Symmetric = true
FEATURE [Sketcher::SketchObject] Sketch026  label="foro sotto anteriore M3x5x6"
  ArcFitTolerance = 1e-06
  AttachmentSupport = -> [XY_Plane]
  FullyConstrained = true
  MakeInternals = false
  MapMode = 5
  sketch-geometry (2):
    g0: LineSegment [constr] StartX=0 StartY=0 StartZ=0 EndX=-16.5 EndY=0 EndZ=0
    g1: Circle CenterX=-16.5 CenterY=0 CenterZ=0 NormalX=0 NormalY=0 NormalZ=1 AngleXU=0 Radius=2.5
  constraints (5):
    c: Distance(g0) = 16.5
    c: Coincident(g0,g-1)
    c: PointOnObject(g0,g-1)
    c: Diameter(g1) = 5
    c: Coincident(g0,g1)
FEATURE [Sketcher::SketchObject] Sketch027  label="foro sotto posteriore M3x5x6"
  ArcFitTolerance = 1e-06
  AttachmentSupport = -> [XY_Plane]
  ExternalGeometry = -> [Sketch]
  FullyConstrained = true
  MakeInternals = false
  MapMode = 5
  sketch-geometry (2):
    g0: LineSegment [constr] StartX=-82.8 StartY=2e-16 StartZ=0 EndX=-71.3 EndY=2e-16 EndZ=0
    g1: Circle CenterX=-71.3 CenterY=2e-16 CenterZ=0 NormalX=0 NormalY=0 NormalZ=1 AngleXU=0 Radius=2.5
  constraints (5):
    c: Distance(g0) = 11.5
    c: Coincident(g0,g-3)
    c: PointOnObject(g0,g-3)
    c: Diameter(g1) = 5
    c: Coincident(g1,g0)
FEATURE [Sketcher::SketchObject] Sketch029  label="fori sotto impugnatura"
  ArcFitTolerance = 1e-06
  AttachmentSupport = -> [XY_Plane]
  ExternalGeometry = -> [Sketch]
  FullyConstrained = true
  MakeInternals = false
  MapMode = 5
  sketch-geometry (15):
    g0: LineSegment [constr] StartX=-175.232 StartY=-1.83e-14 StartZ=0 EndX=-191.232 EndY=0 EndZ=0
    g1: Circle CenterX=-191.232 CenterY=0 CenterZ=0 NormalX=0 NormalY=0 NormalZ=1 AngleXU=0 Radius=3.95
    g2: LineSegment [constr] StartX=-175.232 StartY=-1.83e-14 StartZ=0 EndX=-204.275 EndY=0 EndZ=0
    g3: LineSegment StartX=-204.275 StartY=3.525 StartZ=0 EndX=-204.275 EndY=-3.525 EndZ=0
    g4: LineSegment StartX=-205.4 StartY=-4.65 StartZ=0 EndX=-206.65 EndY=-4.65 EndZ=0
    g5: LineSegment StartX=-207.775 StartY=-3.525 StartZ=0 EndX=-207.775 EndY=3.525 EndZ=0
    g6: LineSegment StartX=-206.65 StartY=4.65 StartZ=0 EndX=-205.4 EndY=4.65 EndZ=0
    g7: ArcOfCircle CenterX=-206.65 CenterY=3.525 CenterZ=0 NormalX=0 NormalY=0 NormalZ=1 AngleXU=0 Radius=1.125 StartAngle=1.5708 EndAngle=3.14159
    g8: GeomPoint [constr] X=-207.775 Y=4.65 Z=0
    g9: ArcOfCircle CenterX=-205.4 CenterY=3.525 CenterZ=0 NormalX=0 NormalY=0 NormalZ=1 AngleXU=0 Radius=1.125 StartAngle=0 EndAngle=1.5708
    g10: GeomPoint [constr] X=-204.275 Y=4.65 Z=0
    g11: ArcOfCircle CenterX=-205.4 CenterY=-3.525 CenterZ=0 NormalX=0 NormalY=0 NormalZ=1 AngleXU=0 Radius=1.125 StartAngle=4.71239 EndAngle=6.28319
    g12: GeomPoint [constr] X=-204.275 Y=-4.65 Z=0
    g13: ArcOfCircle CenterX=-206.65 CenterY=-3.525 CenterZ=0 NormalX=0 NormalY=0 NormalZ=1 AngleXU=0 Radius=1.125 StartAngle=3.14159 EndAngle=4.71239
    g14: GeomPoint [constr] X=-207.775 Y=-4.65 Z=0
  constraints (35):
    c: Distance(g0) = 16
    c: Coincident(g0,g-3)
    c: PointOnObject(g0,g-1)
    c: Diameter(g1) = 7.9
    c: Coincident(g1,g0)
    c: Coincident(g2,g0)
    c: PointOnObject(g2,g-1)
    c: Vertical(g3)
    c: Horizontal(g4)
    c: Vertical(g5)
    c: Horizontal(g6)
    c: DistanceY(g12,g10) = 9.3
    c: DistanceX(g8,g10) = 3.5
    c: Symmetric(g10,g12,g2)
    c: PointOnObject(g8,g5)
    c: PointOnObject(g8,g6)
    c: Tangent(g5,g7) = 1.5708
    c: Tangent(g6,g7) = 1.5708
    c: PointOnObject(g10,g3)
    c: PointOnObject(g10,g6)
    c: Tangent(g3,g9) = 1.5708
    c: Tangent(g6,g9) = 1.5708
    c: PointOnObject(g12,g3)
    c: PointOnObject(g12,g4)
    c: Tangent(g3,g11) = 1.5708
    c: Tangent(g4,g11) = 1.5708
    c: PointOnObject(g14,g4)
    c: PointOnObject(g14,g5)
    c: Tangent(g4,g13) = 1.5708
    c: Tangent(g5,g13) = 1.5708
    c: Equal(g7,g9)
    c: Equal(g9,g11)
    c: Equal(g11,g13)
    c: DistanceX(g6,g6) = 1.25
    c: DistanceX(g-5,g5) = 6.8
FEATURE [Sketcher::SketchObject] Sketch030  label="fori superiori per solenoide e oled"
  ArcFitTolerance = 1e-06
  AttachmentSupport = -> [XY_Plane]
  ExternalGeometry = -> [Sketch]
  FullyConstrained = true
  MakeInternals = false
  MapMode = 5
  sketch-geometry (33):
    g0: LineSegment [constr] StartX=-181.6 StartY=1.12e-14 StartZ=0 EndX=-169.91 EndY=0 EndZ=0
    g1: LineSegment [constr] StartX=-169.91 StartY=0 StartZ=0 EndX=-169.91 EndY=-2.6 EndZ=0
    g2: LineSegment [constr] StartX=-169.91 StartY=0 StartZ=0 EndX=-169.91 EndY=2.6 EndZ=0
    g3: LineSegment StartX=-169.91 StartY=4.975 StartZ=0 EndX=-169.91 EndY=8.225 EndZ=0
    g4: LineSegment StartX=-167.535 StartY=10.6 StartZ=0 EndX=-167.285 EndY=10.6 EndZ=0
    g5: LineSegment StartX=-164.91 StartY=8.225 StartZ=0 EndX=-164.91 EndY=4.975 EndZ=0
    g6: LineSegment StartX=-167.285 StartY=2.6 StartZ=0 EndX=-167.535 EndY=2.6 EndZ=0
    g7: LineSegment StartX=-169.91 StartY=-4.975 StartZ=0 EndX=-169.91 EndY=-8.225 EndZ=0
    g8: LineSegment StartX=-167.535 StartY=-10.6 StartZ=0 EndX=-167.285 EndY=-10.6 EndZ=0
    g9: LineSegment StartX=-164.91 StartY=-8.225 StartZ=0 EndX=-164.91 EndY=-4.975 EndZ=0
    g10: LineSegment StartX=-167.285 StartY=-2.6 StartZ=0 EndX=-167.535 EndY=-2.6 EndZ=0
    g11: ArcOfCircle CenterX=-167.535 CenterY=8.225 CenterZ=0 NormalX=0 NormalY=0 NormalZ=1 AngleXU=0 Radius=2.375 StartAngle=1.5708 EndAngle=3.14159
    g12: GeomPoint [constr] X=-169.91 Y=10.6 Z=0
    g13: ArcOfCircle CenterX=-167.285 CenterY=8.225 CenterZ=0 NormalX=0 NormalY=0 NormalZ=1 AngleXU=0 Radius=2.375 StartAngle=0 EndAngle=1.5708
    g14: GeomPoint [constr] X=-164.91 Y=10.6 Z=0
    g15: ArcOfCircle CenterX=-167.285 CenterY=4.975 CenterZ=0 NormalX=0 NormalY=0 NormalZ=1 AngleXU=0 Radius=2.375 StartAngle=4.71239 EndAngle=6.28319
    g16: GeomPoint [constr] X=-164.91 Y=2.6 Z=0
    g17: ArcOfCircle CenterX=-167.535 CenterY=4.975 CenterZ=0 NormalX=0 NormalY=0 NormalZ=1 AngleXU=0 Radius=2.375 StartAngle=3.14159 EndAngle=4.71239
    g18: GeomPoint [constr] X=-169.91 Y=2.6 Z=0
    g19: ArcOfCircle CenterX=-167.535 CenterY=-4.975 CenterZ=0 NormalX=0 NormalY=0 NormalZ=1 AngleXU=0 Radius=2.375 StartAngle=1.5708 EndAngle=3.14159
    g20: GeomPoint [constr] X=-169.91 Y=-2.6 Z=0
    g21: ArcOfCircle CenterX=-167.285 CenterY=-4.975 CenterZ=0 NormalX=0 NormalY=0 NormalZ=1 AngleXU=0 Radius=2.375 StartAngle=0 EndAngle=1.5708
    g22: GeomPoint [constr] X=-164.91 Y=-2.6 Z=0
    g23: ArcOfCircle CenterX=-167.285 CenterY=-8.225 CenterZ=0 NormalX=0 NormalY=0 NormalZ=1 AngleXU=0 Radius=2.375 StartAngle=4.71239 EndAngle=6.28319
    g24: GeomPoint [constr] X=-164.91 Y=-10.6 Z=0
    g25: ArcOfCircle CenterX=-167.535 CenterY=-8.225 CenterZ=0 NormalX=0 NormalY=0 NormalZ=1 AngleXU=0 Radius=2.375 StartAngle=3.14159 EndAngle=4.71239
    g26: GeomPoint [constr] X=-169.91 Y=-10.6 Z=0
    g27: LineSegment [constr] StartX=-181.6 StartY=1.12e-14 StartZ=0 EndX=-152.209 EndY=0 EndZ=0
    g28: LineSegment [constr] StartX=-181.6 StartY=1.12e-14 StartZ=0 EndX=-130.41 EndY=0 EndZ=0
    g29: LineSegment [constr] StartX=-152.209 StartY=0 StartZ=0 EndX=-152.209 EndY=6.95 EndZ=0
    g30: LineSegment [constr] StartX=-130.41 StartY=0 StartZ=0 EndX=-130.41 EndY=-6.95 EndZ=0
    g31: Circle CenterX=-152.209 CenterY=6.95 CenterZ=0 NormalX=0 NormalY=0 NormalZ=1 AngleXU=0 Radius=2.1
    g32: Circle CenterX=-130.41 CenterY=-6.95 CenterZ=0 NormalX=0 NormalY=0 NormalZ=1 AngleXU=0 Radius=2.1
  constraints (79):
    c: Distance(g0) = 11.69
    c: PointOnObject(g0,g-1)
    c: Coincident(g-4,g0)
    c: Distance(g1) = 2.6
    c: Coincident(g1,g0)
    c: Vertical(g1)
    c: Distance(g2) = 2.6
    c: Coincident(g2,g0)
    c: Vertical(g2)
    c: Distance(g18,g12) = 8
    c: Coincident(g18,g2)
    c: Vertical(g3)
    c: Distance(g14,g12) = 5
    c: Horizontal(g4)
    c: Distance(g16,g14) = 8
    c: Vertical(g5)
    c: Distance(g26,g20) = 8
    c: Coincident(g20,g1)
    c: Vertical(g7)
    c: Distance(g26,g24) = 5
    c: Horizontal(g8)
    c: Distance(g24,g22) = 8
    c: Vertical(g9)
    c: PointOnObject(g12,g3)
    c: PointOnObject(g12,g4)
    c: Tangent(g3,g11) = 1.5708
    c: Tangent(g4,g11) = 1.5708
    c: PointOnObject(g14,g5)
    c: PointOnObject(g14,g4)
    c: Tangent(g5,g13) = 1.5708
    c: Tangent(g4,g13) = 1.5708
    c: PointOnObject(g16,g5)
    c: PointOnObject(g16,g6)
    c: Tangent(g5,g15) = 1.5708
    c: Tangent(g6,g15) = 1.5708
    c: PointOnObject(g18,g3)
    c: PointOnObject(g18,g6)
    c: Tangent(g3,g17) = 1.5708
    c: Tangent(g6,g17) = 1.5708
    c: Equal(g11,g13)
    c: Equal(g13,g15)
    c: Equal(g15,g17)
    c: DistanceX(g4,g4) = 0.25
    c: PointOnObject(g20,g7)
    c: PointOnObject(g20,g10)
    c: Tangent(g7,g19) = -1.5708
    c: Tangent(g10,g19) = -1.5708
    c: PointOnObject(g22,g9)
    c: PointOnObject(g22,g10)
    c: Tangent(g9,g21) = -1.5708
    c: Tangent(g10,g21) = -1.5708
    c: PointOnObject(g24,g9)
    c: PointOnObject(g24,g8)
    c: Tangent(g9,g23) = -1.5708
    c: Tangent(g8,g23) = -1.5708
    c: PointOnObject(g26,g8)
    c: PointOnObject(g26,g7)
    c: Tangent(g8,g25) = -1.5708
    c: Tangent(g7,g25) = -1.5708
    c: Equal(g19,g21)
    c: Equal(g21,g23)
    c: Equal(g23,g25)
    c: DistanceX(g10,g10) = 0.25
    c: Distance(g27) = 29.391
    c: Coincident(g27,g0)
    c: PointOnObject(g27,g-1)
    c: Distance(g28) = 51.19
    c: Coincident(g28,g0)
    c: PointOnObject(g28,g-1)
    c: Distance(g29) = 6.95
    c: Coincident(g29,g27)
    c: Vertical(g29)
    c: Distance(g30) = 6.95
    c: Coincident(g30,g28)
    c: Vertical(g30)
    c: Diameter(g31) = 4.2
    c: Diameter(g32) = 4.2
    c: Coincident(g32,g30)
    c: Coincident(g31,g29)
FEATURE [Sketcher::SketchObject] Sketch031  label="fori inferiori switch pompa"
  ArcFitTolerance = 1e-06
  AttachmentSupport = -> [XY_Plane]
  ExternalGeometry = -> [Sketch]
  FullyConstrained = true
  MakeInternals = false
  MapMode = 5
  sketch-geometry (4):
    g0: LineSegment [constr] StartX=-57.2 StartY=1.9e-15 StartZ=0 EndX=-62.45 EndY=1.9e-15 EndZ=0
    g1: LineSegment [constr] StartX=-62.45 StartY=3.25 StartZ=0 EndX=-62.45 EndY=-3.25 EndZ=0
    g2: Circle CenterX=-62.45 CenterY=3.25 CenterZ=0 NormalX=0 NormalY=0 NormalZ=1 AngleXU=0 Radius=1.6
    g3: Circle CenterX=-62.45 CenterY=-3.25 CenterZ=0 NormalX=0 NormalY=0 NormalZ=1 AngleXU=0 Radius=1.6
  constraints (10):
    c: Distance(g0) = 5.25
    c: Coincident(g0,g-3)
    c: PointOnObject(g0,g-3)
    c: Vertical(g1)
    c: DistanceY(g1,g1) = 6.5
    c: Symmetric(g1,g1,g0)
    c: Diameter(g2) = 3.2
    c: Diameter(g3) = 3.2
    c: Coincident(g2,g1)
    c: Coincident(g3,g1)
FEATURE [Sketcher::SketchObject] Sketch032  label="spazio per PILA 18650"
  ArcFitTolerance = 1e-06
  AttachmentSupport = -> [XY_Plane]
  ExternalGeometry = -> [Sketch]
  FullyConstrained = true
  MakeInternals = false
  MapMode = 5
  sketch-geometry (2):
    g0: LineSegment [constr] StartX=-178.142 StartY=-1.74e-14 StartZ=0 EndX=-191.142 EndY=-1.83e-14 EndZ=0
    g1: Circle CenterX=-191.142 CenterY=-1.83e-14 CenterZ=0 NormalX=0 NormalY=0 NormalZ=1 AngleXU=0 Radius=10.5
  constraints (5):
    c: Distance(g0) = 13
    c: Coincident(g0,g-3)
    c: PointOnObject(g0,g-4)
    c: Diameter(g1) = 21
    c: Coincident(g1,g0)
FEATURE [Part::Extrusion] Extrude030  label="Extrude spazio per PILA 18650"
  Base = -> Sketch032
  Dir = (0,0,1)
  DirLink = -> Sketch [Edge45]
  DirMode = 2
  FaceMakerClass = Part::FaceMakerBullseye
  FaceMakerMode = 3
  LengthFwd = 76
  LengthRev = 0
  Placement = pos=(6,0,-72) rot=(0,0,1;0rad)
  Solid = true
  Symmetric = false
FEATURE [Sketcher::SketchObject] Sketch033  label="fermo per scheda micro"
  ArcFitTolerance = 1e-06
  AttachmentSupport = -> [XZ_Plane]
  ExternalGeometry = -> [Sketch]
  FullyConstrained = true
  MakeInternals = false
  MapMode = 5
  Placement = pos=(0,0,0) rot=(1,0,0;1.5708rad)
  sketch-geometry (12):
    g0: LineSegment StartX=-11.6 StartY=6 StartZ=0 EndX=-4 EndY=6 EndZ=0
    g1: LineSegment StartX=-4 StartY=6 StartZ=0 EndX=-4 EndY=36.4 EndZ=0
    g2: LineSegment StartX=-4 StartY=36.4 StartZ=0 EndX=-11.6 EndY=36.4 EndZ=0
    g3: LineSegment StartX=-11.6 StartY=36.4 StartZ=0 EndX=-11.6 EndY=6 EndZ=0
    g4: LineSegment StartX=-80.11 StartY=11.6 StartZ=0 EndX=-70.51 EndY=11.6 EndZ=0
    g5: LineSegment StartX=-70.51 StartY=11.6 StartZ=0 EndX=-70.51 EndY=6 EndZ=0
    g6: LineSegment StartX=-70.51 StartY=6 StartZ=0 EndX=-80.11 EndY=6 EndZ=0
    g7: LineSegment StartX=-80.11 StartY=6 StartZ=0 EndX=-80.11 EndY=11.6 EndZ=0
    g8: LineSegment StartX=-78.51 StartY=36.4 StartZ=0 EndX=-70.51 EndY=36.4 EndZ=0
    g9: LineSegment StartX=-70.51 StartY=36.4 StartZ=0 EndX=-70.51 EndY=30.8 EndZ=0
    g10: LineSegment StartX=-70.51 StartY=30.8 StartZ=0 EndX=-78.51 EndY=30.8 EndZ=0
    g11: LineSegment StartX=-78.51 StartY=30.8 StartZ=0 EndX=-78.51 EndY=36.4 EndZ=0
  constraints (33):
    c: Horizontal(g0)
    c: Coincident(g1,g0)
    c: Coincident(g2,g1)
    c: Horizontal(g2)
    c: Coincident(g3,g2)
    c: Coincident(g3,g0)
    c: Vertical(g3)
    c: DistanceX(g2,g2) = 7.6
    c: Coincident(g1,g-3)
    c: Coincident(g0,g-3)
    c: Horizontal(g4)
    c: Coincident(g5,g4)
    c: Vertical(g5)
    c: Coincident(g6,g5)
    c: Horizontal(g6)
    c: Coincident(g7,g6)
    c: Coincident(g7,g4)
    c: Vertical(g7)
    c: DistanceY(g5,g5) = 5.6
    c: DistanceX(g4,g4) = 9.6
    c: Coincident(g9,g8)
    c: Vertical(g9)
    c: Coincident(g10,g9)
    c: Horizontal(g10)
    c: Coincident(g11,g10)
    c: Coincident(g11,g8)
    c: Vertical(g11)
    c: DistanceY(g9,g9) = 5.6
    c: DistanceX(g10,g10) = 8
    c: Coincident(g4,g-4)
    c: DistanceX(g4,g10) = 1.6
    c: Horizontal(g8)
    c: DistanceY(g8,g1) = 0
FEATURE [Sketcher::SketchObject] Sketch034  label="buchi guida rail"
  ArcFitTolerance = 1e-06
  AttachmentSupport = -> [XY_Plane]
  ExternalGeometry = -> [Sketch]
  FullyConstrained = true
  MakeInternals = false
  MapMode = 5
  sketch-geometry (6):
    g0: LineSegment [constr] StartX=-100.8 StartY=9.1e-15 StartZ=0 EndX=-93.3 EndY=0 EndZ=0
    g1: LineSegment [constr] StartX=-93.3 StartY=0 StartZ=0 EndX=-73.3 EndY=0 EndZ=0
    g2: LineSegment [constr] StartX=-73.3 StartY=0 StartZ=0 EndX=-53.3 EndY=0 EndZ=0
    g3: Circle CenterX=-93.3 CenterY=0 CenterZ=0 NormalX=0 NormalY=0 NormalZ=1 AngleXU=0 Radius=2.5
    g4: Circle CenterX=-73.3 CenterY=0 CenterZ=0 NormalX=0 NormalY=0 NormalZ=1 AngleXU=0 Radius=2.5
    g5: Circle CenterX=-53.3 CenterY=0 CenterZ=0 NormalX=0 NormalY=0 NormalZ=1 AngleXU=0 Radius=2.5
  constraints (15):
    c: Distance(g0) = 7.5
    c: Coincident(g0,g-3)
    c: PointOnObject(g0,g-1)
    c: Distance(g1) = 20
    c: Coincident(g1,g0)
    c: PointOnObject(g1,g-1)
    c: Distance(g2) = 20
    c: Coincident(g2,g1)
    c: PointOnObject(g2,g-1)
    c: Diameter(g3) = 5
    c: Diameter(g4) = 5
    c: Diameter(g5) = 5
    c: Coincident(g3,g0)
    c: Coincident(g4,g1)
    c: Coincident(g5,g2)
FEATURE [Part::Extrusion] Extrude032  label="Extrude buchi guida rail"
  Base = -> Sketch034
  Dir = (0,0,1)
  DirMode = 2
  FaceMakerClass = Part::FaceMakerBullseye
  FaceMakerMode = 3
  LengthFwd = -6.2
  LengthRev = 0
  Placement = pos=(0,0,43.2) rot=(0,0,1;0rad)
  Solid = true
  Symmetric = false
FEATURE [Part::Extrusion] Extrude033  label="Extrude fori superiori per solenoide e oled001"
  Base = -> Sketch030
  Dir = (0,0,1)
  DirMode = 2
  FaceMakerClass = Part::FaceMakerBullseye
  FaceMakerMode = 3
  LengthFwd = -4.8
  LengthRev = 0
  Placement = pos=(0,0,41.2) rot=(0,0,1;0rad)
  Solid = true
  Symmetric = false
FEATURE [Part::Extrusion] Extrude034  label="Extrude fori sotto impugnatura001"
  Base = -> Sketch029
  Dir = (0,0,1)
  DirMode = 2
  FaceMakerClass = Part::FaceMakerBullseye
  FaceMakerMode = 3
  LengthFwd = 5
  LengthRev = 0
  Placement = pos=(0,0,-83) rot=(0,0,1;0rad)
  Solid = true
  Symmetric = false
FEATURE [Part::Extrusion] Extrude035  label="Extrude fori inferiori switch pompa001"
  Base = -> Sketch031
  Dir = (0,0,1)
  DirMode = 2
  FaceMakerClass = Part::FaceMakerBullseye
  FaceMakerMode = 3
  LengthFwd = 4
  LengthRev = 0
  Placement = pos=(0,0,-1.7) rot=(0,0,1;0rad)
  Solid = true
  Symmetric = false
FEATURE [Part::Extrusion] Extrude036  label="Extrude foro sotto posteriore M3x5x007"
  Base = -> Sketch027
  Dir = (0,0,1)
  DirMode = 2
  FaceMakerClass = Part::FaceMakerBullseye
  FaceMakerMode = 3
  LengthFwd = 6.2
  LengthRev = 0
  Placement = pos=(0,0,-9.6) rot=(0,0,1;0rad)
  Solid = true
  Symmetric = false
FEATURE [Part::Extrusion] Extrude037  label="Extrude foro sotto anteriore M3x5x007"
  Base = -> Sketch026
  Dir = (0,0,1)
  DirMode = 2
  FaceMakerClass = Part::FaceMakerBullseye
  FaceMakerMode = 3
  LengthFwd = 6.2
  LengthRev = 0
  Solid = true
  Symmetric = false
FEATURE [Sketcher::SketchObject] Sketch035  label="foro per fissaggio micro"
  ArcFitTolerance = 1e-06
  AttachmentSupport = -> [XZ_Plane]
  ExternalGeometry = -> [Sketch,Sketch033]
  FullyConstrained = true
  MakeInternals = false
  MapMode = 5
  Placement = pos=(0,0,0) rot=(1,0,0;1.5708rad)
  sketch-geometry (3):
    g0: Circle CenterX=-7.8 CenterY=21.2 CenterZ=0 NormalX=0 NormalY=0 NormalZ=1 AngleXU=0 Radius=1.6
    g1: GeomPoint [constr] X=-4 Y=21.2 Z=0
    g2: LineSegment [constr] StartX=-4 StartY=21.2 StartZ=0 EndX=-11.6 EndY=21.2 EndZ=0
  constraints (6):
    c: Diameter(g0) = 3.2
    c: Symmetric(g-3,g-3,g1)
    c: Coincident(g2,g1)
    c: Horizontal(g2)
    c: DistanceX(g-4,g2) = 0
    c: Symmetric(g2,g1,g0)
FEATURE [Part::Extrusion] Extrude038  label="Extrude foro per fissaggio micro"
  Base = -> Sketch035
  Dir = (0,-1,2e-16)
  DirMode = 2
  FaceMakerClass = Part::FaceMakerBullseye
  FaceMakerMode = 3
  LengthFwd = 3
  LengthRev = 0
  Placement = pos=(0,8.6,0) rot=(0,0,1;0rad)
  Solid = true
  Symmetric = false
FEATURE [Sketcher::SketchObject] Sketch036  label="supporto per alimentatore"
  ArcFitTolerance = 1e-06
  AttachmentSupport = -> [XZ_Plane]
  ExternalGeometry = -> [Sketch,Sketch016,Sketch022]
  FullyConstrained = true
  MakeInternals = false
  MapMode = 5
  Placement = pos=(0,0,0) rot=(1,0,0;1.5708rad)
  sketch-geometry (5):
    g0: LineSegment StartX=-211.843 StartY=-50.0944 StartZ=0 EndX=-211.843 EndY=-80.4316 EndZ=0
    g1: LineSegment StartX=-211.843 StartY=-50.0944 StartZ=0 EndX=-207.775 EndY=-41.3701 EndZ=0
    g2: LineSegment [constr] StartX=-209.443 StartY=-50.0944 StartZ=0 EndX=-209.443 EndY=-80.4316 EndZ=0
    g3: LineSegment StartX=-207.775 StartY=-41.3701 StartZ=0 EndX=-207.775 EndY=-80.4316 EndZ=0
    g4: LineSegment StartX=-211.843 StartY=-80.4316 StartZ=0 EndX=-207.775 EndY=-80.4316 EndZ=0
  constraints (15):
    c: Vertical(g0)
    c: Coincident(g1,g0)
    c: Vertical(g2)
    c: Tangent(g2,g-5)
    c: Coincident(g3,g1)
    c: Vertical(g3)
    c: DistanceY(g-3,g3) = -2
    c: Tangent(g1,g-8)
    c: DistanceY(g-3,g0) = -2
    c: Coincident(g4,g0)
    c: Coincident(g4,g3)
    c: Tangent(g0,g-6)
    c: DistanceY(g-3,g2) = -2
    c: DistanceY(g2,g0) = 0
    c: DistanceX(g-3,g3) = 6.8
FEATURE [Part::Extrusion] Extrude039  label="Extrude039 supporto alimentatore"
  Base = -> Sketch036
  Dir = (0,-1,2e-16)
  DirMode = 2
  FaceMakerClass = Part::FaceMakerBullseye
  FaceMakerMode = 3
  LengthFwd = 25.2
  LengthRev = 0
  Solid = true
  Symmetric = true
FEATURE [Sketcher::SketchObject] Sketch037  label="scavo per alimentatore"
  ArcFitTolerance = 1e-06
  AttachmentSupport = -> [XZ_Plane]
  ExternalGeometry = -> [Sketch036]
  FullyConstrained = true
  MakeInternals = false
  MapMode = 5
  Placement = pos=(0,0,0) rot=(1,0,0;1.5708rad)
  sketch-geometry (4):
    g0: LineSegment StartX=-209.575 StartY=-50.4316 StartZ=0 EndX=-209.575 EndY=-80.4316 EndZ=0
    g1: LineSegment StartX=-209.575 StartY=-50.4316 StartZ=0 EndX=-207.775 EndY=-50.4316 EndZ=0
    g2: LineSegment StartX=-207.775 StartY=-50.4316 StartZ=0 EndX=-207.775 EndY=-80.4316 EndZ=0
    g3: LineSegment StartX=-207.775 StartY=-80.4316 StartZ=0 EndX=-209.575 EndY=-80.4316 EndZ=0
  constraints (11):
    c: Vertical(g0)
    c: Coincident(g1,g0)
    c: Horizontal(g1)
    c: Coincident(g2,g1)
    c: Vertical(g2)
    c: Coincident(g3,g2)
    c: Coincident(g3,g0)
    c: Horizontal(g3)
    c: DistanceX(g1,g1) = 1.8
    c: Coincident(g2,g-3)
    c: DistanceY(g2,g2) = 30
FEATURE [Part::Extrusion] Extrude040  label="Extrude040 scavo alimentatore"
  Base = -> Sketch037
  Dir = (0,-1,2e-16)
  DirMode = 2
  FaceMakerClass = Part::FaceMakerBullseye
  FaceMakerMode = 3
  LengthFwd = 19.5
  LengthRev = 0
  Solid = true
  Symmetric = true
FEATURE [Part::Extrusion] Extrude031  label="Extrude fermo per scheda micro"
  Base = -> Sketch033
  Dir = (0,-1,2e-16)
  DirMode = 2
  FaceMakerClass = Part::FaceMakerBullseye
  FaceMakerMode = 3
  LengthFwd = 3
  LengthRev = 0
  Placement = pos=(0,8.6,0) rot=(0,0,1;0rad)
  Solid = true
  Symmetric = false
FEATURE [Sketcher::SketchObject] Sketch038  label="scavo driver solenoide"
  ArcFitTolerance = 1e-06
  AttachmentSupport = -> [XZ_Plane]
  ExternalGeometry = -> [Sketch,Sketch036]
  FullyConstrained = true
  MakeInternals = false
  MapMode = 5
  Placement = pos=(0,0,0) rot=(1,0,0;1.5708rad)
  sketch-geometry (7):
    g0: LineSegment StartX=-192.222 StartY=-8.0175 StartZ=0 EndX=-194.941 EndY=-6.74965 EndZ=0
    g1: LineSegment StartX=-194.941 StartY=-6.74965 StartZ=0 EndX=-212.269 EndY=-43.9083 EndZ=0
    g2: LineSegment StartX=-192.222 StartY=-8.0175 StartZ=0 EndX=-188.779 EndY=-9.62345 EndZ=0
    g3: LineSegment StartX=-188.779 StartY=-9.62345 StartZ=0 EndX=-205.357 EndY=-45.1761 EndZ=0
    g4: LineSegment StartX=-205.357 StartY=-45.1761 StartZ=0 EndX=-209.55 EndY=-45.1761 EndZ=0
    g5: LineSegment [constr] StartX=-212.269 StartY=-43.9083 StartZ=0 EndX=-209.55 EndY=-45.1761 EndZ=0
    g6: LineSegment StartX=-212.269 StartY=-43.9083 StartZ=0 EndX=-209.55 EndY=-45.1761 EndZ=0
  constraints (20):
    c: Coincident(g1,g0)
    c: Coincident(g3,g2)
    c: Coincident(g4,g3)
    c: Distance(g2) = 3.8
    c: Distance(g1) = 41
    c: Coincident(g5,g1)
    c: Distance(g5) = 3
    c: Perpendicular(g5,g-3)
    c: Parallel(g1,g-3)
    c: Perpendicular(g1,g0)
    c: Distance(g0) = 3
    c: Coincident(g6,g1)
    c: Parallel(g3,g-3)
    c: Perpendicular(g2,g3)
    c: Coincident(g2,g0)
    c: Perpendicular(g-4,g4)
    c: PointOnObject(g5,g-3)
    c: Distance(g-3,g5) = 9.6
    c: Coincident(g4,g5)
    c: Coincident(g6,g4)
FEATURE [Part::Extrusion] Extrude041  label="Extrude scavo driver solenoide"
  Base = -> Sketch038
  Dir = (0,-1,2e-16)
  DirMode = 2
  FaceMakerClass = Part::FaceMakerBullseye
  FaceMakerMode = 3
  LengthFwd = 20.6
  LengthRev = 0
  Solid = true
  Symmetric = true
FEATURE [Sketcher::SketchObject] Sketch039  label="scavo per cavo usb per micro"
  ArcFitTolerance = 1e-06
  AttachmentSupport = -> [XZ_Plane]
  ExternalGeometry = -> [Sketch,Sketch016]
  FullyConstrained = true
  MakeInternals = false
  MapMode = 5
  Placement = pos=(0,0,0) rot=(1,0,0;1.5708rad)
  sketch-geometry (4):
    g0: LineSegment StartX=-82.51 StartY=36.4 StartZ=0 EndX=-74.51 EndY=36.4 EndZ=0
    g1: LineSegment StartX=-74.51 StartY=36.4 StartZ=0 EndX=-74.51 EndY=30.8 EndZ=0
    g2: LineSegment StartX=-74.51 StartY=30.8 StartZ=0 EndX=-82.51 EndY=30.8 EndZ=0
    g3: LineSegment StartX=-82.51 StartY=30.8 StartZ=0 EndX=-82.51 EndY=36.4 EndZ=0
  constraints (11):
    c: Coincident(g1,g0)
    c: Vertical(g1)
    c: Coincident(g2,g1)
    c: Horizontal(g2)
    c: Coincident(g3,g2)
    c: Coincident(g3,g0)
    c: Vertical(g3)
    c: Tangent(g0,g-3)
    c: Tangent(g2,g-4)
    c: Tangent(g3,g-4)
    c: Tangent(g1,g-4)
FEATURE [Part::Extrusion] Extrude042  label="Extrude scavo per cavo usb per micro"
  Base = -> Sketch039
  Dir = (0,-1,2e-16)
  DirMode = 2
  FaceMakerClass = Part::FaceMakerBullseye
  FaceMakerMode = 3
  LengthFwd = 11.2
  LengthRev = 0
  Solid = true
  Symmetric = true
FEATURE [Sketcher::SketchObject] Sketch040  label="scavo saldature alimentatore connettore 5v"
  ArcFitTolerance = 1e-06
  AttachmentSupport = -> [XZ_Plane]
  ExternalGeometry = -> [Sketch037]
  FullyConstrained = true
  MakeInternals = false
  MapMode = 5
  Placement = pos=(0,0,0) rot=(1,0,0;1.5708rad)
  sketch-geometry (4):
    g0: LineSegment StartX=-211.175 StartY=-52.4316 StartZ=0 EndX=-211.175 EndY=-56.4316 EndZ=0
    g1: LineSegment StartX=-211.175 StartY=-52.4316 StartZ=0 EndX=-209.575 EndY=-52.4316 EndZ=0
    g2: LineSegment StartX=-209.575 StartY=-52.4316 StartZ=0 EndX=-209.575 EndY=-56.4316 EndZ=0
    g3: LineSegment StartX=-209.575 StartY=-56.4316 StartZ=0 EndX=-211.175 EndY=-56.4316 EndZ=0
  constraints (11):
    c: Vertical(g0)
    c: Coincident(g1,g0)
    c: Horizontal(g1)
    c: Coincident(g2,g1)
    c: Coincident(g3,g2)
    c: Coincident(g3,g0)
    c: Horizontal(g3)
    c: DistanceX(g1,g1) = 1.6
    c: DistanceY(g2,g2) = 4
    c: Tangent(g2,g-3)
    c: DistanceY(g1,g-3) = 2
FEATURE [Part::Extrusion] Extrude043  label="Extrude scavo saldature alimentatore connettore 5v"
  Base = -> Sketch040
  Dir = (0,-1,2e-16)
  DirMode = 2
  FaceMakerClass = Part::FaceMakerBullseye
  FaceMakerMode = 3
  LengthFwd = 8
  LengthRev = 0
  Solid = true
  Symmetric = true
FEATURE [Sketcher::SketchObject] Sketch041  label="scavo saldature alimentatore connettore 5v verticali"
  ArcFitTolerance = 1e-06
  AttachmentSupport = -> [XZ_Plane]
  ExternalGeometry = -> [Sketch037]
  FullyConstrained = true
  MakeInternals = false
  MapMode = 5
  Placement = pos=(0,0,0) rot=(1,0,0;1.5708rad)
  sketch-geometry (4):
    g0: LineSegment StartX=-211.175 StartY=-53.6316 StartZ=0 EndX=-209.575 EndY=-53.6316 EndZ=0
    g1: LineSegment StartX=-209.575 StartY=-53.6316 StartZ=0 EndX=-209.575 EndY=-76.6316 EndZ=0
    g2: LineSegment StartX=-209.575 StartY=-76.6316 StartZ=0 EndX=-211.175 EndY=-76.6316 EndZ=0
    g3: LineSegment StartX=-211.175 StartY=-76.6316 StartZ=0 EndX=-211.175 EndY=-53.6316 EndZ=0
  constraints (11):
    c: Horizontal(g0)
    c: Coincident(g1,g0)
    c: Coincident(g2,g1)
    c: Horizontal(g2)
    c: Coincident(g3,g2)
    c: Coincident(g3,g0)
    c: Vertical(g3)
    c: DistanceY(g3,g3) = 23
    c: DistanceX(g0,g0) = 1.6
    c: Tangent(g1,g-3)
    c: DistanceY(g0,g-3) = 3.2
FEATURE [Part::Extrusion] Extrude044  label="Extrude scavo saldature alimentatore connettore 5v verticali"
  Base = -> Sketch041
  Dir = (0,-1,2e-16)
  DirMode = 2
  FaceMakerClass = Part::FaceMakerBullseye
  FaceMakerMode = 3
  LengthFwd = 3.2
  LengthRev = 0
  Placement = pos=(0,8.3,0) rot=(0,0,1;0rad)
  Solid = true
  Symmetric = false
FEATURE [Sketcher::SketchObject] Sketch042  label="fermi per driver solenoide e alimentatore"
  ArcFitTolerance = 1e-06
  AttachmentSupport = -> [XZ_Plane]
  ExternalGeometry = -> [Sketch036,Sketch037,Sketch,Sketch038]
  FullyConstrained = true
  MakeInternals = false
  MapMode = 5
  Placement = pos=(0,0,0) rot=(1,0,0;1.5708rad)
  sketch-geometry (27):
    g0: LineSegment StartX=-200.506 StartY=-25.7811 StartZ=0 EndX=-201.436 EndY=-27.775 EndZ=0
    g1: LineSegment StartX=-201.436 StartY=-27.775 StartZ=0 EndX=-199.442 EndY=-28.7048 EndZ=0
    g2: LineSegment StartX=-199.442 StartY=-28.7048 StartZ=0 EndX=-198.512 EndY=-26.7109 EndZ=0
    g3: LineSegment StartX=-198.512 StartY=-26.7109 StartZ=0 EndX=-200.506 EndY=-25.7811 EndZ=0
    g4: LineSegment StartX=-201.28 StartY=-23.6549 StartZ=0 EndX=-203.562 EndY=-28.5489 EndZ=0
    g5: LineSegment StartX=-203.562 StartY=-28.5489 StartZ=0 EndX=-200.118 EndY=-30.1549 EndZ=0
    g6: LineSegment StartX=-197.992 StartY=-29.381 StartZ=0 EndX=-197.062 EndY=-27.3871 EndZ=0
    g7: LineSegment StartX=-197.836 StartY=-25.2608 StartZ=0 EndX=-201.28 EndY=-23.6549 EndZ=0
    g8: LineSegment [constr] StartX=-198.668 StartY=-30.8311 StartZ=0 EndX=-197.992 EndY=-29.381 EndZ=0
    g9: LineSegment [constr] StartX=-198.668 StartY=-30.8311 StartZ=0 EndX=-200.118 EndY=-30.1549 EndZ=0
    g10: ArcOfCircle CenterX=-198.512 CenterY=-26.7109 CenterZ=0 NormalX=0 NormalY=0 NormalZ=1 AngleXU=0 Radius=1.6 StartAngle=5.84685 EndAngle=7.41765
    g11: GeomPoint [constr] X=-196.386 Y=-25.937 Z=0
    g12: ArcOfCircle CenterX=-199.442 CenterY=-28.7048 CenterZ=0 NormalX=0 NormalY=0 NormalZ=1 AngleXU=0 Radius=1.6 StartAngle=4.27606 EndAngle=5.84685
    g13: GeomPoint [constr] X=-198.668 Y=-30.8311 Z=0
    g14: LineSegment StartX=-207.775 StartY=-46.8316 StartZ=0 EndX=-207.775 EndY=-50.8316 EndZ=0
    g15: LineSegment StartX=-207.775 StartY=-46.8316 StartZ=0 EndX=-203.775 EndY=-46.8316 EndZ=0
    g16: LineSegment StartX=-203.775 StartY=-46.8316 StartZ=0 EndX=-203.775 EndY=-50.8316 EndZ=0
    g17: LineSegment StartX=-207.775 StartY=-50.8316 StartZ=0 EndX=-203.775 EndY=-50.8316 EndZ=0
    g18: LineSegment StartX=-209.375 StartY=-52.4316 StartZ=0 EndX=-203.775 EndY=-52.4316 EndZ=0
    g19: LineSegment StartX=-202.175 StartY=-50.8316 StartZ=0 EndX=-202.175 EndY=-46.8316 EndZ=0
    g20: LineSegment StartX=-203.775 StartY=-45.2316 StartZ=0 EndX=-209.375 EndY=-45.2316 EndZ=0
    g21: LineSegment StartX=-209.375 StartY=-45.2316 StartZ=0 EndX=-209.375 EndY=-52.4316 EndZ=0
    g22: ArcOfCircle CenterX=-203.775 CenterY=-46.8316 CenterZ=0 NormalX=0 NormalY=0 NormalZ=1 AngleXU=0 Radius=1.6 StartAngle=1.8e-15 EndAngle=1.5708
    g23: GeomPoint [constr] X=-202.175 Y=-45.2316 Z=0
    g24: ArcOfCircle CenterX=-203.775 CenterY=-50.8316 CenterZ=0 NormalX=0 NormalY=0 NormalZ=1 AngleXU=0 Radius=1.6 StartAngle=4.71239 EndAngle=6.28319
    g25: GeomPoint [constr] X=-202.175 Y=-52.4316 Z=0
    g26: LineSegment [constr] StartX=-207.775 StartY=-50.4316 StartZ=0 EndX=-207.775 EndY=-50.8316 EndZ=0
  constraints (69):
    c: Coincident(g1,g0)
    c: Coincident(g2,g1)
    c: Coincident(g3,g2)
    c: Coincident(g3,g0)
    c: Parallel(g0,g2)
    c: Perpendicular(g3,g0)
    c: Perpendicular(g1,g0)
    c: Coincident(g5,g4)
    c: Coincident(g7,g4)
    c: Distance(g3) = 2.2
    c: Distance(g2) = 2.2
    c: Parallel(g6,g2)
    c: Parallel(g6,g4)
    c: Perpendicular(g5,g6)
    c: Perpendicular(g7,g6)
    c: Distance(g13,g11) = 5.4
    c: Distance(g5,g13) = 5.4
    c: Coincident(g9,g8)
    c: Distance(g8) = 1.6
    c: Distance(g9) = 1.6
    c: Perpendicular(g9,g8)
    c: Parallel(g8,g6)
    c: Coincident(g8,g13)
    c: Distance(g8,g1) = 1.6
    c: Distance(g9,g1) = 1.6
    c: Tangent(g0,g-5)
    c: Distance(g0,g-6) = 19.2
    c: PointOnObject(g11,g7)
    c: PointOnObject(g11,g6)
    c: Tangent(g7,g10) = -1.5708
    c: Tangent(g6,g10) = -1.5708
    c: PointOnObject(g13,g5)
    c: Tangent(g5,g12) = -1.5708
    c: Tangent(g6,g12) = -1.5708
    c: Equal(g10,g12)
    c: Coincident(g10,g2)
    c: Vertical(g14)
    c: Coincident(g15,g14)
    c: Horizontal(g15)
    c: Coincident(g16,g15)
    c: Vertical(g16)
    c: Coincident(g17,g14)
    c: Coincident(g17,g16)
    c: Horizontal(g17)
    c: Distance(g16) = 4
    c: Distance(g15) = 4
    c: Horizontal(g18)
    c: Vertical(g19)
    c: Horizontal(g20)
    c: Coincident(g21,g20)
    c: Coincident(g21,g18)
    c: Vertical(g21)
    c: Distance(g20,g23) = 7.2
    c: Distance(g25,g23) = 7.2
    c: DistanceY(g18,g14) = 1.6
    c: DistanceX(g18,g14) = 1.6
    c: PointOnObject(g23,g20)
    c: PointOnObject(g23,g19)
    c: Tangent(g20,g22) = -1.5708
    c: Tangent(g19,g22) = -1.5708
    c: PointOnObject(g25,g19)
    c: Tangent(g18,g24) = -1.5708
    c: Tangent(g19,g24) = -1.5708
    c: Equal(g22,g24)
    c: Coincident(g22,g15)
    c: Vertical(g26)
    c: Distance(g26) = 0.4
    c: Coincident(g26,g-4)
    c: Coincident(g14,g26)
FEATURE [Part::Extrusion] Extrude045  label="Extrude fermi per driver solenoide e alimentatore"
  Base = -> Sketch042
  Dir = (0,-1,2e-16)
  DirMode = 2
  FaceMakerClass = Part::FaceMakerBullseye
  FaceMakerMode = 3
  LengthFwd = 25.2
  LengthRev = 0
  Solid = true
  Symmetric = true
FEATURE [Sketcher::SketchObject] Sketch043  label="scavo pulizia fermo alimentatore"
  ArcFitTolerance = 1e-06
  AttachmentSupport = -> [XZ_Plane]
  ExternalGeometry = -> [Sketch042,Sketch036,Sketch037]
  FullyConstrained = true
  MakeInternals = false
  MapMode = 5
  Placement = pos=(0,0,0) rot=(1,0,0;1.5708rad)
  sketch-geometry (6):
    g0: LineSegment StartX=-209.375 StartY=-52.4316 StartZ=0 EndX=-209.375 EndY=-50.4316 EndZ=0
    g1: LineSegment StartX=-209.375 StartY=-50.4316 StartZ=0 EndX=-207.775 EndY=-50.4316 EndZ=0
    g2: LineSegment StartX=-207.775 StartY=-50.4316 StartZ=0 EndX=-207.775 EndY=-45.2316 EndZ=0
    g3: LineSegment StartX=-207.775 StartY=-45.2316 StartZ=0 EndX=-202.175 EndY=-45.2316 EndZ=0
    g4: LineSegment StartX=-202.175 StartY=-45.2316 StartZ=0 EndX=-202.175 EndY=-52.4316 EndZ=0
    g5: LineSegment StartX=-202.175 StartY=-52.4316 StartZ=0 EndX=-209.375 EndY=-52.4316 EndZ=0
  constraints (13):
    c: Vertical(g0)
    c: Coincident(g1,g0)
    c: Coincident(g2,g1)
    c: Coincident(g3,g2)
    c: Coincident(g4,g3)
    c: Coincident(g5,g4)
    c: Coincident(g5,g0)
    c: Horizontal(g5)
    c: Coincident(g0,g-6)
    c: Tangent(g1,g-8)
    c: Tangent(g2,g-4)
    c: Tangent(g3,g-7)
    c: Tangent(g4,g-3)
FEATURE [Part::Extrusion] Extrude046  label="Extrude scavo pulizia fermo alimentatore"
  Base = -> Sketch043
  Dir = (0,-1,2e-16)
  DirMode = 2
  FaceMakerClass = Part::FaceMakerBullseye
  FaceMakerMode = 3
  LengthFwd = 19.5
  LengthRev = 0
  Solid = true
  Symmetric = true
FEATURE [Sketcher::SketchObject] Sketch044  label="buchini per fissaggio oled"
  ArcFitTolerance = 1e-06
  AttachmentSupport = -> [YZ_Plane]
  ExternalGeometry = -> [Sketch]
  FullyConstrained = true
  MakeInternals = false
  MapMode = 5
  Placement = pos=(0,0,0) rot=(0.57735,0.57735,0.57735;2.0944rad)
  sketch-geometry (5):
    g0: LineSegment [constr] StartX=1.5e-14 StartY=67.3588 StartZ=0 EndX=0 EndY=64.3588 EndZ=0
    g1: LineSegment [constr] StartX=0 StartY=64.3588 StartZ=0 EndX=10.4 EndY=64.3588 EndZ=0
    g2: LineSegment [constr] StartX=0 StartY=64.3588 StartZ=0 EndX=-10.4 EndY=64.3588 EndZ=0
    g3: Circle CenterX=10.4 CenterY=64.3588 CenterZ=0 NormalX=0 NormalY=0 NormalZ=1 AngleXU=0 Radius=1.5
    g4: Circle CenterX=-10.4 CenterY=64.3588 CenterZ=0 NormalX=0 NormalY=0 NormalZ=1 AngleXU=0 Radius=1.5
  constraints (13):
    c: Distance(g0) = 3
    c: PointOnObject(g0,g-2)
    c: Coincident(g1,g0)
    c: Horizontal(g1)
    c: Coincident(g2,g0)
    c: Horizontal(g2)
    c: DistanceX(g1,g1) = 10.4
    c: Coincident(g3,g1)
    c: Diameter(g4) = 3
    c: Coincident(g4,g2)
    c: Coincident(g0,g-7)
    c: Equal(g1,g2)
    c: Equal(g4,g3)
FEATURE [Part::Extrusion] Extrude047  label="Extrude buchini per fissaggio oled"
  Base = -> Sketch044
  Dir = (1,0,0)
  DirMode = 2
  FaceMakerClass = Part::FaceMakerBullseye
  FaceMakerMode = 3
  LengthFwd = 10
  LengthRev = 0
  Placement = pos=(-186,0,0) rot=(0,0,1;0rad)
  Solid = true
  Symmetric = false
FEATURE [Sketcher::SketchObject] Sketch046  label="scavo 5x5 neopixel"
  ArcFitTolerance = 1e-06
  AttachmentSupport = -> [YZ_Plane002]
  FullyConstrained = true
  MakeInternals = false
  MapMode = 5
  Placement = pos=(0,0,0) rot=(0.57735,0.57735,0.57735;2.0944rad)
  sketch-geometry (4):
    g0: LineSegment StartX=-2.7 StartY=2.7 StartZ=0 EndX=2.7 EndY=2.7 EndZ=0
    g1: LineSegment StartX=2.7 StartY=2.7 StartZ=0 EndX=2.7 EndY=-2.7 EndZ=0
    g2: LineSegment StartX=2.7 StartY=-2.7 StartZ=0 EndX=-2.7 EndY=-2.7 EndZ=0
    g3: LineSegment StartX=-2.7 StartY=-2.7 StartZ=0 EndX=-2.7 EndY=2.7 EndZ=0
  constraints (11):
    c: Horizontal(g0)
    c: Coincident(g1,g0)
    c: Vertical(g1)
    c: Coincident(g2,g1)
    c: Horizontal(g2)
    c: Coincident(g3,g2)
    c: Coincident(g3,g0)
    c: Vertical(g3)
    c: DistanceX(g0,g0) = 5.4
    c: DistanceY(g1,g1) = 5.4
    c: Symmetric(g0,g1,g-1)
FEATURE [Sketcher::SketchObject] Sketch047  label="scavo 10x10 neopixel corpo"
  ArcFitTolerance = 1e-06
  AttachmentOffset = pos=(0,0,1) rot=(0,0,1;0rad)
  AttachmentSupport = -> [YZ_Plane002]
  FullyConstrained = true
  MakeInternals = false
  MapMode = 5
  Placement = pos=(1,0,0) rot=(0.57735,0.57735,0.57735;2.0944rad)
  sketch-geometry (4):
    g0: LineSegment StartX=-5 StartY=5.1 StartZ=0 EndX=5 EndY=5.1 EndZ=0
    g1: LineSegment StartX=5 StartY=5.1 StartZ=0 EndX=5 EndY=-5.1 EndZ=0
    g2: LineSegment StartX=5 StartY=-5.1 StartZ=0 EndX=-5 EndY=-5.1 EndZ=0
    g3: LineSegment StartX=-5 StartY=-5.1 StartZ=0 EndX=-5 EndY=5.1 EndZ=0
  constraints (11):
    c: Horizontal(g0)
    c: Coincident(g1,g0)
    c: Vertical(g1)
    c: Coincident(g2,g1)
    c: Horizontal(g2)
    c: Coincident(g3,g2)
    c: Coincident(g3,g0)
    c: Vertical(g3)
    c: DistanceX(g0,g0) = 10
    c: DistanceY(g1,g1) = 10.2
    c: Symmetric(g0,g2,g-1)
FEATURE [Sketcher::SketchObject] Sketch048  label="buco per perno blocco neopixel"
  ArcFitTolerance = 1e-06
  AttachmentSupport = -> [XZ_Plane002]
  FullyConstrained = true
  MakeInternals = false
  MapMode = 5
  Placement = pos=(0,0,0) rot=(1,0,0;1.5708rad)
  sketch-geometry (4):
    g0: LineSegment StartX=3 StartY=1.2 StartZ=0 EndX=3 EndY=-1.2 EndZ=0
    g1: LineSegment StartX=3 StartY=-1.2 StartZ=0 EndX=5.4 EndY=-1.2 EndZ=0
    g2: LineSegment StartX=5.4 StartY=-1.2 StartZ=0 EndX=5.4 EndY=1.2 EndZ=0
    g3: LineSegment StartX=5.4 StartY=1.2 StartZ=0 EndX=3 EndY=1.2 EndZ=0
  constraints (11):
    c: Coincident(g1,g0)
    c: Horizontal(g1)
    c: Coincident(g2,g1)
    c: Vertical(g2)
    c: Coincident(g3,g2)
    c: Coincident(g3,g0)
    c: Horizontal(g3)
    c: DistanceX(g1,g1) = 2.4
    c: DistanceY(g2,g2) = 2.4
    c: Symmetric(g0,g0,g-1)
    c: DistanceX(g-1,g0) = 3
FEATURE [Sketcher::SketchObject] Sketch045  label="blocco principale per neopixel"
  ArcFitTolerance = 1e-06
  AttachmentSupport = -> [XZ_Plane002]
  ExternalGeometry = -> [Sketch048]
  FullyConstrained = true
  MakeInternals = false
  MapMode = 5
  Placement = pos=(0,0,0) rot=(1,0,0;1.5708rad)
  sketch-geometry (6):
    g0: LineSegment StartX=0 StartY=5.1 StartZ=0 EndX=0 EndY=-5.1 EndZ=0
    g1: LineSegment StartX=0 StartY=-5.1 StartZ=0 EndX=3 EndY=-5.1 EndZ=0
    g2: LineSegment StartX=7 StartY=-1.1 StartZ=0 EndX=7 EndY=5.1 EndZ=0
    g3: LineSegment StartX=7 StartY=5.1 StartZ=0 EndX=0 EndY=5.1 EndZ=0
    g4: ArcOfCircle CenterX=3 CenterY=-1.1 CenterZ=0 NormalX=0 NormalY=0 NormalZ=1 AngleXU=0 Radius=4 StartAngle=4.71239 EndAngle=6.28319
    g5: GeomPoint [constr] X=7 Y=-5.1 Z=0
  constraints (15):
    c: Vertical(g0)
    c: Coincident(g1,g0)
    c: Horizontal(g1)
    c: Vertical(g2)
    c: Coincident(g3,g2)
    c: Coincident(g3,g0)
    c: Horizontal(g3)
    c: DistanceY(g0,g0) = 10.2
    c: Symmetric(g0,g0,g-1)
    c: DistanceX(g3,g3) = 7
    c: PointOnObject(g5,g2)
    c: PointOnObject(g5,g1)
    c: Tangent(g2,g4) = -1.5708
    c: Tangent(g1,g4) = -1.5708
    c: DistanceX(g-3,g1) = 0
FEATURE [Sketcher::SketchObject] Sketch049  label="rinforzi esterni per corpo neopoixel"
  ArcFitTolerance = 1e-06
  AttachmentSupport = -> [XZ_Plane002]
  ExternalGeometry = -> [Sketch045]
  FullyConstrained = true
  MakeInternals = false
  MapMode = 5
  Placement = pos=(0,0,0) rot=(1,0,0;1.5708rad)
  sketch-geometry (8):
    g0: LineSegment StartX=1 StartY=-4.1 StartZ=0 EndX=2 EndY=-4.1 EndZ=0
    g1: LineSegment StartX=2 StartY=-4.1 StartZ=0 EndX=2 EndY=-5.1 EndZ=0
    g2: LineSegment StartX=2 StartY=-5.1 StartZ=0 EndX=1 EndY=-5.1 EndZ=0
    g3: LineSegment StartX=1 StartY=-5.1 StartZ=0 EndX=1 EndY=-4.1 EndZ=0
    g4: LineSegment StartX=1 StartY=5.1 StartZ=0 EndX=2 EndY=5.1 EndZ=0
    g5: LineSegment StartX=2 StartY=5.1 StartZ=0 EndX=2 EndY=4.1 EndZ=0
    g6: LineSegment StartX=2 StartY=4.1 StartZ=0 EndX=1 EndY=4.1 EndZ=0
    g7: LineSegment StartX=1 StartY=4.1 StartZ=0 EndX=1 EndY=5.1 EndZ=0
  constraints (24):
    c: Horizontal(g0)
    c: Coincident(g1,g0)
    c: Vertical(g1)
    c: Coincident(g2,g1)
    c: Horizontal(g2)
    c: Coincident(g3,g2)
    c: Coincident(g3,g0)
    c: Vertical(g3)
    c: Horizontal(g4)
    c: Coincident(g5,g4)
    c: Vertical(g5)
    c: Coincident(g6,g5)
    c: Horizontal(g6)
    c: Coincident(g7,g6)
    c: Coincident(g7,g4)
    c: Vertical(g7)
    c: DistanceX(g4,g4) = 1
    c: DistanceY(g5,g5) = 1
    c: DistanceX(g0,g0) = 1
    c: DistanceY(g1,g1) = 1
    c: DistanceX(g-3,g4) = 1
    c: DistanceY(g-3,g4) = 0
    c: DistanceX(g-4,g2) = 1
    c: DistanceY(g2,g-4) = 0
FEATURE [Sketcher::SketchObject] Sketch052  label="scavo saldature driver solenoide"
  ArcFitTolerance = 1e-06
  AttachmentSupport = -> [XZ_Plane]
  ExternalGeometry = -> [Sketch038]
  FullyConstrained = true
  MakeInternals = false
  MapMode = 5
  Placement = pos=(0,0,0) rot=(1,0,0;1.5708rad)
  sketch-geometry (4):
    g0: LineSegment StartX=-195.304 StartY=-6.5806 StartZ=0 EndX=-196.994 EndY=-10.2058 EndZ=0
    g1: LineSegment StartX=-196.994 StartY=-10.2058 StartZ=0 EndX=-196.632 EndY=-10.3749 EndZ=0
    g2: LineSegment StartX=-196.632 StartY=-10.3749 StartZ=0 EndX=-194.941 EndY=-6.74965 EndZ=0
    g3: LineSegment StartX=-194.941 StartY=-6.74965 StartZ=0 EndX=-195.304 EndY=-6.5806 EndZ=0
  constraints (11):
    c: Coincident(g1,g0)
    c: Coincident(g2,g1)
    c: Coincident(g3,g2)
    c: Coincident(g3,g0)
    c: Parallel(g2,g0)
    c: Perpendicular(g2,g3)
    c: Perpendicular(g1,g2,g1) = 1.5708
    c: Parallel(g2,g-3)
    c: Distance(g2) = 4
    c: Distance(g3) = 0.4
    c: Coincident(g2,g-3)
FEATURE [Part::Extrusion] Extrude055  label="Extrude scavo saldature driver solenoide"
  Base = -> Sketch052
  Dir = (0,-1,2e-16)
  DirMode = 2
  FaceMakerClass = Part::FaceMakerBullseye
  FaceMakerMode = 3
  LengthFwd = 6
  LengthRev = 0
  Solid = true
  Symmetric = true
FEATURE [Sketcher::SketchObject] Sketch053  label="scavo saldature rumble"
  ArcFitTolerance = 1e-06
  AttachmentSupport = -> [XZ_Plane]
  ExternalGeometry = -> [Sketch019]
  FullyConstrained = true
  MakeInternals = false
  MapMode = 5
  Placement = pos=(0,0,0) rot=(1,0,0;1.5708rad)
  sketch-geometry (4):
    g0: LineSegment StartX=-164.507 StartY=-41.6446 StartZ=0 EndX=-165.743 EndY=-45.4488 EndZ=0
    g1: LineSegment StartX=-165.743 StartY=-45.4488 StartZ=0 EndX=-164.602 EndY=-45.8196 EndZ=0
    g2: LineSegment StartX=-164.602 StartY=-45.8196 StartZ=0 EndX=-163.366 EndY=-42.0154 EndZ=0
    g3: LineSegment StartX=-163.366 StartY=-42.0154 StartZ=0 EndX=-164.507 EndY=-41.6446 EndZ=0
  constraints (11):
    c: Coincident(g1,g0)
    c: Coincident(g2,g1)
    c: Coincident(g3,g2)
    c: Coincident(g3,g0)
    c: Parallel(g0,g2)
    c: Perpendicular(g3,g0)
    c: Perpendicular(g1,g0)
    c: Parallel(g0,g-3)
    c: Distance(g0) = 4
    c: Distance(g1) = 1.2
    c: Coincident(g0,g-3)
FEATURE [Part::Extrusion] Extrude056  label="Extrude scavo saldature rumble"
  Base = -> Sketch053
  Dir = (0,-1,2e-16)
  DirMode = 2
  FaceMakerClass = Part::FaceMakerBullseye
  FaceMakerMode = 3
  LengthFwd = 8.4
  LengthRev = 0
  Solid = true
  Symmetric = true
FEATURE [Sketcher::SketchObject] Sketch054  label="scavo saldature alimentatore connettore USB"
  ArcFitTolerance = 1e-06
  AttachmentSupport = -> [XZ_Plane]
  ExternalGeometry = -> [Sketch037]
  FullyConstrained = true
  MakeInternals = false
  MapMode = 5
  Placement = pos=(0,0,0) rot=(1,0,0;1.5708rad)
  sketch-geometry (4):
    g0: LineSegment StartX=-209.575 StartY=-80.4316 StartZ=0 EndX=-210.375 EndY=-80.4316 EndZ=0
    g1: LineSegment StartX=-210.375 StartY=-80.4316 StartZ=0 EndX=-210.375 EndY=-72.4316 EndZ=0
    g2: LineSegment StartX=-210.375 StartY=-72.4316 StartZ=0 EndX=-209.575 EndY=-72.4316 EndZ=0
    g3: LineSegment StartX=-209.575 StartY=-72.4316 StartZ=0 EndX=-209.575 EndY=-80.4316 EndZ=0
  constraints (11):
    c: Horizontal(g0)
    c: Coincident(g1,g0)
    c: Vertical(g1)
    c: Coincident(g2,g1)
    c: Horizontal(g2)
    c: Coincident(g3,g2)
    c: Coincident(g3,g0)
    c: Vertical(g3)
    c: DistanceX(g0,g0) = 0.8
    c: DistanceY(g3,g3) = 8
    c: Coincident(g0,g-4)
FEATURE [Part::Extrusion] Extrude057  label="Extrude scavo saldature alimentatore connettore USB"
  Base = -> Sketch054
  Dir = (0,-1,2e-16)
  DirMode = 2
  FaceMakerClass = Part::FaceMakerBullseye
  FaceMakerMode = 3
  LengthFwd = 11
  LengthRev = 0
  Solid = true
  Symmetric = true
FEATURE [Sketcher::SketchObject] Sketch055  label="buco interno per micro switch"
  ArcFitTolerance = 1e-06
  AttachmentSupport = -> [XZ_Plane]
  ExternalGeometry = -> [Sketch]
  FullyConstrained = true
  MakeInternals = false
  MapMode = 5
  Placement = pos=(0,0,0) rot=(1,0,0;1.5708rad)
  sketch-geometry (11):
    g0: LineSegment [constr] StartX=-194.483 StartY=34.2854 StartZ=0 EndX=-196.022 EndY=30.0568 EndZ=0
    g1: LineSegment [constr] StartX=-196.022 StartY=30.0568 StartZ=0 EndX=-197.561 EndY=25.8282 EndZ=0
    g2: LineSegment [constr] StartX=-196.022 StartY=30.0568 StartZ=0 EndX=-194.143 EndY=29.3727 EndZ=0
    g3: LineSegment [constr] StartX=-196.022 StartY=30.0568 StartZ=0 EndX=-197.902 EndY=30.7408 EndZ=0
    g4: LineSegment StartX=-196.362 StartY=34.9694 StartZ=0 EndX=-192.604 EndY=33.6014 EndZ=0
    g5: LineSegment StartX=-199.441 StartY=26.5122 StartZ=0 EndX=-195.682 EndY=25.1441 EndZ=0
    g6: LineSegment StartX=-192.604 StartY=33.6014 StartZ=0 EndX=-195.682 EndY=25.1441 EndZ=0
    g7: LineSegment StartX=-196.362 StartY=34.9694 StartZ=0 EndX=-199.441 EndY=26.5122 EndZ=0
    g8: GeomPoint [constr] X=-187.821 Y=29.2 Z=0
    g9: LineSegment [constr] StartX=-188.505 StartY=27.3206 StartZ=0 EndX=-196.022 EndY=30.0568 EndZ=0
    g10: LineSegment [constr] StartX=-187.821 StartY=29.2 StartZ=0 EndX=-188.505 EndY=27.3206 EndZ=0
  constraints (27):
    c: Coincident(g2,g0)
    c: Parallel(g0,g-3)
    c: Tangent(g1,g0) = -1.5708
    c: Perpendicular(g0,g2)
    c: Tangent(g2,g3)
    c: Distance(g0,g1) = 9
    c: Equal(g0,g1)
    c: Distance(g3,g2) = 4
    c: Equal(g2,g3)
    c: Parallel(g3,g4)
    c: Symmetric(g4,g4,g0)
    c: Parallel(g6,g1)
    c: Parallel(g7,g1)
    c: Symmetric(g6,g6,g2)
    c: Symmetric(g5,g5,g1)
    c: Symmetric(g7,g7,g3)
    c: Coincident(g7,g4)
    c: Coincident(g6,g4)
    c: Coincident(g5,g6)
    c: Symmetric(g-3,g-3,g8)
    c: Perpendicular(g-3,g9)
    c: Distance(g9) = 8
    c: Coincident(g3,g9)
    c: Coincident(g10,g8)
    c: Parallel(g10,g-3)
    c: Distance(g10) = 2
    c: Coincident(g10,g9)
FEATURE [Sketcher::SketchObject] Sketch056  label="buco esterno per micro switch"
  ArcFitTolerance = 1e-06
  AttachmentSupport = -> [XZ_Plane]
  ExternalGeometry = -> [Sketch055]
  FullyConstrained = true
  MakeInternals = false
  MapMode = 5
  Placement = pos=(0,0,0) rot=(1,0,0;1.5708rad)
  sketch-geometry (17):
    g0: GeomPoint [constr] X=-194.143 Y=29.3727 Z=0
    g1: GeomPoint [constr] X=-194.483 Y=34.2854 Z=0
    g2: GeomPoint [constr] X=-197.902 Y=30.7408 Z=0
    g3: GeomPoint [constr] X=-197.561 Y=25.8282 Z=0
    g4: GeomPoint [constr] X=-196.022 Y=30.0568 Z=0
    g5: LineSegment [constr] StartX=-194.483 StartY=34.2854 StartZ=0 EndX=-196.022 EndY=30.0568 EndZ=0
    g6: LineSegment [constr] StartX=-196.022 StartY=30.0568 StartZ=0 EndX=-197.561 EndY=25.8282 EndZ=0
    g7: LineSegment [constr] StartX=-197.902 StartY=30.7408 StartZ=0 EndX=-196.022 EndY=30.0568 EndZ=0
    g8: LineSegment [constr] StartX=-196.022 StartY=30.0568 StartZ=0 EndX=-194.143 EndY=29.3727 EndZ=0
    g9: LineSegment [constr] StartX=-195.338 StartY=31.9362 StartZ=0 EndX=-196.022 EndY=30.0568 EndZ=0
    g10: LineSegment [constr] StartX=-196.022 StartY=30.0568 StartZ=0 EndX=-196.706 EndY=28.1774 EndZ=0
    g11: LineSegment [constr] StartX=-196.022 StartY=30.0568 StartZ=0 EndX=-196.821 EndY=30.3475 EndZ=0
    g12: LineSegment [constr] StartX=-196.022 StartY=30.0568 StartZ=0 EndX=-195.223 EndY=29.7661 EndZ=0
    g13: LineSegment StartX=-194.539 StartY=31.6454 StartZ=0 EndX=-195.907 EndY=27.8867 EndZ=0
    g14: LineSegment StartX=-196.137 StartY=32.2269 StartZ=0 EndX=-197.505 EndY=28.4681 EndZ=0
    g15: LineSegment StartX=-196.137 StartY=32.2269 StartZ=0 EndX=-194.539 EndY=31.6454 EndZ=0
    g16: LineSegment StartX=-197.505 StartY=28.4681 StartZ=0 EndX=-195.907 EndY=27.8867 EndZ=0
  constraints (34):
    c: Symmetric(g-5,g-5,g1)
    c: Symmetric(g-5,g-6,g0)
    c: Symmetric(g-6,g-6,g3)
    c: Symmetric(g-5,g-6,g2)
    c: Coincident(g5,g1)
    c: Coincident(g5,g4)
    c: Coincident(g6,g4)
    c: Coincident(g6,g3)
    c: Equal(g5,g6)
    c: Coincident(g7,g2)
    c: Coincident(g7,g4)
    c: Coincident(g8,g4)
    c: Coincident(g8,g0)
    c: Equal(g7,g8)
    c: Coincident(g11,g9)
    c: Coincident(g12,g9)
    c: Tangent(g10,g9) = -1.5708
    c: Perpendicular(g11,g9)
    c: Parallel(g9,g-4)
    c: Equal(g9,g10)
    c: Parallel(g12,g11)
    c: Equal(g11,g12)
    c: Distance(g11,g12) = 1.7
    c: Distance(g9,g10) = 4
    c: Symmetric(g13,g13,g12)
    c: Parallel(g13,g9)
    c: Symmetric(g14,g14,g11)
    c: Symmetric(g15,g15,g9)
    c: Parallel(g15,g11)
    c: Symmetric(g16,g16,g10)
    c: Coincident(g16,g14)
    c: Coincident(g15,g14)
    c: Coincident(g13,g15)
    c: Coincident(g9,g4)
FEATURE [Sketcher::SketchObject] Sketch057  label="buco interno per SWITCH"
  ArcFitTolerance = 1e-06
  AttachmentSupport = -> [XZ_Plane]
  ExternalGeometry = -> [Sketch]
  FullyConstrained = true
  MakeInternals = false
  MapMode = 5
  Placement = pos=(0,0,0) rot=(1,0,0;1.5708rad)
  sketch-geometry (10):
    g0: GeomPoint [constr] X=-187.821 Y=29.2 Z=0
    g1: LineSegment [constr] StartX=-188.505 StartY=27.3206 StartZ=0 EndX=-193.203 EndY=29.0307 EndZ=0
    g2: LineSegment [constr] StartX=-190.809 StartY=35.6086 StartZ=0 EndX=-195.597 EndY=22.4529 EndZ=0
    g3: GeomPoint [constr] X=-193.203 Y=29.0307 Z=0
    g4: LineSegment [constr] StartX=-196.492 StartY=30.2278 StartZ=0 EndX=-189.914 EndY=27.8336 EndZ=0
    g5: LineSegment StartX=-194.098 StartY=36.8056 StartZ=0 EndX=-187.52 EndY=34.4115 EndZ=0
    g6: LineSegment StartX=-194.098 StartY=36.8056 StartZ=0 EndX=-198.886 EndY=23.6499 EndZ=0
    g7: LineSegment StartX=-187.52 StartY=34.4115 StartZ=0 EndX=-192.308 EndY=21.2558 EndZ=0
    g8: LineSegment StartX=-198.886 StartY=23.6499 StartZ=0 EndX=-192.308 EndY=21.2558 EndZ=0
    g9: LineSegment [constr] StartX=-187.821 StartY=29.2 StartZ=0 EndX=-188.505 EndY=27.3206 EndZ=0
  constraints (23):
    c: Symmetric(g-3,g-3,g0)
    c: Perpendicular(g1,g-3)
    c: Parallel(g2,g-3)
    c: Symmetric(g2,g2,g3)
    c: Perpendicular(g2,g4)
    c: Symmetric(g4,g4,g3)
    c: Distance(g2) = 14
    c: Distance(g4) = 7
    c: Distance(g1) = 5
    c: Parallel(g5,g4)
    c: Parallel(g7,g2)
    c: Symmetric(g5,g5,g2)
    c: Symmetric(g6,g6,g4)
    c: Symmetric(g7,g7,g4)
    c: Symmetric(g8,g8,g2)
    c: Coincident(g6,g5)
    c: Coincident(g7,g5)
    c: Coincident(g8,g7)
    c: Coincident(g3,g1)
    c: Coincident(g9,g0)
    c: Parallel(g9,g-3)
    c: Distance(g9) = 2
    c: Coincident(g1,g9)
FEATURE [Sketcher::SketchObject] Sketch058  label="buco esterno per SWITCH"
  ArcFitTolerance = 1e-06
  AttachmentSupport = -> [XZ_Plane]
  ExternalGeometry = -> [Sketch057]
  FullyConstrained = true
  MakeInternals = false
  MapMode = 5
  Placement = pos=(0,0,0) rot=(1,0,0;1.5708rad)
  sketch-geometry (12):
    g0: GeomPoint [constr] X=-190.809 Y=35.6086 Z=0
    g1: GeomPoint [constr] X=-196.492 Y=30.2278 Z=0
    g2: GeomPoint [constr] X=-189.914 Y=27.8336 Z=0
    g3: GeomPoint [constr] X=-195.597 Y=22.4529 Z=0
    g4: GeomPoint [constr] X=-193.203 Y=29.0307 Z=0
    g5: LineSegment [constr] StartX=-192.006 StartY=32.3196 StartZ=0 EndX=-194.4 EndY=25.7418 EndZ=0
    g6: GeomPoint [constr] X=-193.203 Y=29.0307 Z=0
    g7: LineSegment [constr] StartX=-195.082 StartY=29.7148 StartZ=0 EndX=-191.324 EndY=28.3467 EndZ=0
    g8: LineSegment StartX=-193.885 StartY=33.0037 StartZ=0 EndX=-190.127 EndY=31.6356 EndZ=0
    g9: LineSegment StartX=-190.127 StartY=31.6356 StartZ=0 EndX=-192.521 EndY=25.0578 EndZ=0
    g10: LineSegment StartX=-196.28 StartY=26.4258 StartZ=0 EndX=-192.521 EndY=25.0578 EndZ=0
    g11: LineSegment StartX=-193.885 StartY=33.0037 StartZ=0 EndX=-196.28 EndY=26.4258 EndZ=0
  constraints (21):
    c: Symmetric(g-6,g-6,g3)
    c: Symmetric(g-4,g-6,g2)
    c: Symmetric(g-5,g-4,g0)
    c: Symmetric(g-5,g-6,g1)
    c: Symmetric(g1,g2,g4)
    c: Parallel(g5,g-4)
    c: Symmetric(g5,g5,g6)
    c: Perpendicular(g7,g5)
    c: Symmetric(g7,g7,g6)
    c: Distance(g5) = 7
    c: Distance(g7) = 4
    c: Parallel(g8,g7)
    c: Parallel(g11,g5)
    c: Symmetric(g8,g8,g5)
    c: Symmetric(g9,g9,g7)
    c: Symmetric(g10,g10,g5)
    c: Symmetric(g11,g11,g7)
    c: Coincident(g11,g8)
    c: Coincident(g9,g8)
    c: Coincident(g9,g10)
    c: Coincident(g6,g4)
FEATURE [Part::Extrusion] Extrude060  label="Extrude buco interno per SWITCH destro"
  Base = -> Sketch057
  Dir = (0,-1,2e-16)
  DirMode = 2
  FaceMakerClass = Part::FaceMakerBullseye
  FaceMakerMode = 3
  LengthFwd = 13.2
  LengthRev = 0
  Placement = pos=(0,2.6,0) rot=(0,0,1;0rad)
  Solid = true
  Symmetric = false
FEATURE [Part::Extrusion] Extrude061  label="Extrude buco esterno per SWITCH destro"
  Base = -> Sketch058
  Dir = (0,-1,2e-16)
  DirMode = 2
  FaceMakerClass = Part::FaceMakerBullseye
  FaceMakerMode = 3
  LengthFwd = 2
  LengthRev = 0
  Placement = pos=(0,-10.6,0) rot=(0,0,1;0rad)
  Solid = true
  Symmetric = false
FEATURE [Sketcher::SketchObject] Sketch059  label="buco per spazio introduzione SWITCH"
  ArcFitTolerance = 1e-06
  AttachmentSupport = -> [XZ_Plane]
  ExternalGeometry = -> [Sketch057,Sketch010]
  FullyConstrained = true
  MakeInternals = false
  MapMode = 5
  Placement = pos=(0,0,0) rot=(1,0,0;1.5708rad)
  sketch-geometry (8):
    g0: LineSegment [constr] StartX=-201.368 StartY=36.3521 StartZ=0 EndX=-195.094 EndY=34.0687 EndZ=0
    g1: LineSegment [constr] StartX=-194.098 StartY=36.8056 StartZ=0 EndX=-195.094 EndY=34.0687 EndZ=0
    g2: LineSegment StartX=-198.658 StartY=24.2771 StartZ=0 EndX=-199.654 EndY=21.5401 EndZ=0
    g3: LineSegment StartX=-199.654 StartY=21.5401 StartZ=0 EndX=-181.196 EndY=14.822 EndZ=0
    g4: LineSegment StartX=-181.196 StartY=14.822 StartZ=0 EndX=-180.2 EndY=17.559 EndZ=0
    g5: LineSegment StartX=-180.2 StartY=17.559 StartZ=0 EndX=-198.658 EndY=24.2771 EndZ=0
    g6: LineSegment [constr] StartX=-204.932 StartY=26.5605 StartZ=0 EndX=-198.658 EndY=24.2771 EndZ=0
    g7: LineSegment [constr] StartX=-198.658 StartY=24.2771 StartZ=0 EndX=-199.654 EndY=21.5401 EndZ=0
  constraints (20):
    c: Parallel(g1,g-3)
    c: Parallel(g0,g-4)
    c: Coincident(g0,g-4)
    c: Coincident(g1,g-3)
    c: Coincident(g0,g1)
    c: Coincident(g3,g2)
    c: Coincident(g4,g3)
    c: Coincident(g5,g4)
    c: Coincident(g5,g2)
    c: Parallel(g5,g-5)
    c: Parallel(g3,g-5)
    c: Parallel(g4,g-6)
    c: DistanceX(g-6,g4) = 0
    c: Coincident(g6,g-5)
    c: Equal(g6,g0)
    c: Coincident(g7,g6)
    c: Equal(g7,g1)
    c: Tangent(g7,g-3)
    c: Coincident(g2,g6)
    c: Coincident(g2,g7)
FEATURE [Part::Extrusion] Extrude062  label="Extrude buco per spazio introduzione SWITCH"
  Base = -> Sketch059
  Dir = (0,-1,2e-16)
  DirMode = 2
  FaceMakerClass = Part::FaceMakerBullseye
  FaceMakerMode = 3
  LengthFwd = 13.2
  LengthRev = 0
  Solid = true
  Symmetric = true
FEATURE [Part::Extrusion] Extrude063  label="Extrude buco interno per SWITCH sinistro"
  Base = -> Sketch057
  Dir = (0,-1,2e-16)
  DirMode = 2
  FaceMakerClass = Part::FaceMakerBullseye
  FaceMakerMode = 3
  LengthFwd = 13.2
  LengthRev = 0
  Placement = pos=(0,10.6,0) rot=(0,0,1;0rad)
  Solid = true
  Symmetric = false
FEATURE [Part::Extrusion] Extrude064  label="Extrude buco esterno per SWITCH sinistro"
  Base = -> Sketch058
  Dir = (0,-1,2e-16)
  DirMode = 2
  FaceMakerClass = Part::FaceMakerBullseye
  FaceMakerMode = 3
  LengthFwd = 2
  LengthRev = 0
  Placement = pos=(0,12.6,0) rot=(0,0,1;0rad)
  Solid = true
  Symmetric = false
FEATURE [Sketcher::SketchObject] Sketch061  label="struttura esterna blocco switch"
  ArcFitTolerance = 1e-06
  AttachmentSupport = -> [XZ_Plane003]
  FullyConstrained = true
  MakeInternals = false
  MapMode = 5
  Placement = pos=(0,0,0) rot=(1,0,0;1.5708rad)
  sketch-geometry (5):
    g0: LineSegment StartX=-1 StartY=-5.1 StartZ=0 EndX=1 EndY=-5.1 EndZ=0
    g1: LineSegment StartX=1 StartY=-5.1 StartZ=0 EndX=1 EndY=5.1 EndZ=0
    g2: LineSegment StartX=1 StartY=5.1 StartZ=0 EndX=-1 EndY=5.1 EndZ=0
    g3: LineSegment StartX=-1 StartY=5.1 StartZ=0 EndX=-1 EndY=-5.1 EndZ=0
    g4: GeomPoint [constr] X=0 Y=0 Z=0
  constraints (12):
    c: Coincident(g0,g1)
    c: Coincident(g1,g2)
    c: Coincident(g2,g3)
    c: Coincident(g3,g0)
    c: Horizontal(g0)
    c: Horizontal(g2)
    c: Vertical(g1)
    c: Vertical(g3)
    c: Symmetric(g2,g0,g4)
    c: Distance(g1,g3) = 2
    c: Distance(g0,g2) = 10.2
    c: Coincident(g4,g-1)
FEATURE [Sketcher::SketchObject] Sketch062  label="struttura interna blocco switch"
  ArcFitTolerance = 1e-06
  AttachmentSupport = -> [XZ_Plane003]
  ExternalGeometry = -> [Sketch061]
  FullyConstrained = true
  MakeInternals = false
  MapMode = 5
  Placement = pos=(0,0,0) rot=(1,0,0;1.5708rad)
  sketch-geometry (5):
    g0: LineSegment StartX=-1 StartY=3.1 StartZ=0 EndX=-1 EndY=-3.1 EndZ=0
    g1: LineSegment StartX=-1 StartY=-3.1 StartZ=0 EndX=1 EndY=-3.1 EndZ=0
    g2: LineSegment StartX=1 StartY=-3.1 StartZ=0 EndX=1 EndY=3.1 EndZ=0
    g3: LineSegment StartX=1 StartY=3.1 StartZ=0 EndX=-1 EndY=3.1 EndZ=0
    g4: GeomPoint [constr] X=0 Y=0 Z=0
  constraints (12):
    c: Coincident(g0,g1)
    c: Coincident(g1,g2)
    c: Coincident(g2,g3)
    c: Coincident(g3,g0)
    c: Vertical(g0)
    c: Vertical(g2)
    c: Horizontal(g1)
    c: Horizontal(g3)
    c: Symmetric(g2,g0,g4)
    c: Coincident(g4,g-1)
    c: Distance(g0) = 6.2
    c: Equal(g3,g-3)
FEATURE [Sketcher::SketchObject] Sketch063  label="blocchi tra switch"
  ArcFitTolerance = 1e-06
  AttachmentSupport = -> [XZ_Plane003]
  ExternalGeometry = -> [Sketch061,Sketch062]
  FullyConstrained = true
  MakeInternals = false
  MapMode = 5
  Placement = pos=(0,0,0) rot=(1,0,0;1.5708rad)
  sketch-geometry (8):
    g0: LineSegment StartX=-3 StartY=5.1 StartZ=0 EndX=-1 EndY=5.1 EndZ=0
    g1: LineSegment StartX=-1 StartY=5.1 StartZ=0 EndX=-1 EndY=3.1 EndZ=0
    g2: LineSegment StartX=-1 StartY=3.1 StartZ=0 EndX=-3 EndY=3.1 EndZ=0
    g3: LineSegment StartX=-3 StartY=3.1 StartZ=0 EndX=-3 EndY=5.1 EndZ=0
    g4: LineSegment StartX=-3 StartY=-3.1 StartZ=0 EndX=-1 EndY=-3.1 EndZ=0
    g5: LineSegment StartX=-1 StartY=-3.1 StartZ=0 EndX=-1 EndY=-5.1 EndZ=0
    g6: LineSegment StartX=-1 StartY=-5.1 StartZ=0 EndX=-3 EndY=-5.1 EndZ=0
    g7: LineSegment StartX=-3 StartY=-5.1 StartZ=0 EndX=-3 EndY=-3.1 EndZ=0
  constraints (20):
    c: Horizontal(g0)
    c: Coincident(g1,g0)
    c: Coincident(g2,g1)
    c: Horizontal(g2)
    c: Coincident(g3,g2)
    c: Coincident(g3,g0)
    c: Vertical(g3)
    c: Horizontal(g4)
    c: Coincident(g5,g4)
    c: Coincident(g6,g5)
    c: Horizontal(g6)
    c: Coincident(g7,g6)
    c: Coincident(g7,g4)
    c: Vertical(g7)
    c: Coincident(g0,g-4)
    c: Coincident(g1,g-5)
    c: Coincident(g4,g-6)
    c: Coincident(g5,g-7)
    c: Distance(g0) = 2
    c: Distance(g4) = 2
FEATURE [Sketcher::SketchObject] Sketch066  label="piano per rampino"
  ArcFitTolerance = 1e-06
  AttachmentSupport = -> [XZ_Plane002]
  ExternalGeometry = -> [Sketch045]
  FullyConstrained = true
  MakeInternals = false
  MapMode = 5
  Placement = pos=(0,0,0) rot=(1,0,0;1.5708rad)
  sketch-geometry (4):
    g0: LineSegment StartX=5.4 StartY=5.1 StartZ=0 EndX=5.4 EndY=3.9 EndZ=0
    g1: LineSegment StartX=5.4 StartY=3.9 StartZ=0 EndX=7 EndY=3.9 EndZ=0
    g2: LineSegment StartX=7 StartY=3.9 StartZ=0 EndX=7 EndY=5.1 EndZ=0
    g3: LineSegment StartX=7 StartY=5.1 StartZ=0 EndX=5.4 EndY=5.1 EndZ=0
  constraints (11):
    c: Coincident(g0,g1)
    c: Coincident(g1,g2)
    c: Coincident(g2,g3)
    c: Coincident(g3,g0)
    c: Vertical(g0)
    c: Vertical(g2)
    c: Horizontal(g1)
    c: Horizontal(g3)
    c: Distance(g0,g2) = 1.6
    c: Distance(g1,g3) = 1.2
    c: Coincident(g2,g-3)
FEATURE [Sketcher::SketchObject] Sketch064  label="rampini_per_serraggio_struttura"
  ArcFitTolerance = 1e-06
  AttachmentSupport = -> [XZ_Plane002]
  ExternalGeometry = -> [Sketch066,Sketch045]
  FullyConstrained = true
  MakeInternals = false
  MapMode = 5
  Placement = pos=(0,0,0) rot=(1,0,0;1.5708rad)
  sketch-geometry (7):
    g0: LineSegment StartX=7 StartY=5.1 StartZ=0 EndX=7 EndY=3.9 EndZ=0
    g1: LineSegment StartX=7 StartY=3.9 StartZ=0 EndX=9 EndY=3.9 EndZ=0
    g2: LineSegment StartX=7 StartY=5.1 StartZ=0 EndX=7 EndY=5.1 EndZ=0
    g3: LineSegment StartX=7 StartY=5.1 StartZ=0 EndX=7 EndY=7.5 EndZ=0
    g4: LineSegment StartX=9 StartY=5.1 StartZ=0 EndX=9 EndY=3.9 EndZ=0
    g5: LineSegment StartX=7 StartY=7.5 StartZ=0 EndX=9 EndY=7.5 EndZ=0
    g6: LineSegment StartX=9 StartY=7.5 StartZ=0 EndX=9 EndY=5.1 EndZ=0
  constraints (20):
    c: Vertical(g0)
    c: Coincident(g1,g0)
    c: Horizontal(g1)
    c: Coincident(g2,g0)
    c: Horizontal(g2)
    c: Coincident(g3,g2)
    c: Vertical(g3)
    c: Coincident(g5,g3)
    c: Coincident(g4,g6)
    c: Coincident(g4,g1)
    c: Vertical(g4)
    c: Coincident(g0,g-3)
    c: DistanceY(g-4,g3) = 2.4
    c: DistanceX(g1,g1) = 2
    c: DistanceY(g2,g6) = 0
    c: DistanceX(g2,g2) = 0
    c: DistanceY(g0,g0) = 1.2
    c: Coincident(g5,g6)
    c: Horizontal(g5)
    c: Vertical(g6)
FEATURE [Sketcher::SketchObject] Sketch067  label="perno per blocco switch"
  ArcFitTolerance = 1e-06
  AttachmentSupport = -> [XZ_Plane]
  ExternalGeometry = -> [Sketch,Sketch010]
  FullyConstrained = true
  MakeInternals = false
  MapMode = 5
  Placement = pos=(0,0,0) rot=(1,0,0;1.5708rad)
  sketch-geometry (14):
    g0: LineSegment StartX=-191.073 StartY=24.9429 StartZ=0 EndX=-185.81 EndY=23.0276 EndZ=0
    g1: LineSegment StartX=-183.76 StartY=23.9839 StartZ=0 EndX=-182.392 EndY=27.7427 EndZ=0
    g2: LineSegment StartX=-183.348 StartY=29.7934 StartZ=0 EndX=-188.61 EndY=31.7087 EndZ=0
    g3: LineSegment StartX=-188.61 StartY=31.7087 StartZ=0 EndX=-191.073 EndY=24.9429 EndZ=0
    g4: GeomPoint [constr] X=-186.459 Y=27.0946 Z=0
    g5: LineSegment StartX=-189.022 StartY=25.8992 StartZ=0 EndX=-185.263 EndY=24.5311 EndZ=0
    g6: LineSegment StartX=-185.263 StartY=24.5311 StartZ=0 EndX=-183.895 EndY=28.2899 EndZ=0
    g7: LineSegment StartX=-183.895 StartY=28.2899 StartZ=0 EndX=-187.654 EndY=29.658 EndZ=0
    g8: LineSegment StartX=-187.654 StartY=29.658 StartZ=0 EndX=-189.022 EndY=25.8992 EndZ=0
    g9: GeomPoint [constr] X=-186.459 Y=27.0946 Z=0
    g10: ArcOfCircle CenterX=-185.263 CenterY=24.5311 CenterZ=0 NormalX=0 NormalY=0 NormalZ=1 AngleXU=0 Radius=1.6 StartAngle=4.36332 EndAngle=5.93412
    g11: GeomPoint [constr] X=-184.307 Y=22.4804 Z=0
    g12: ArcOfCircle CenterX=-183.895 CenterY=28.2899 CenterZ=0 NormalX=0 NormalY=0 NormalZ=1 AngleXU=0 Radius=1.6 StartAngle=5.93412 EndAngle=7.50492
    g13: GeomPoint [constr] X=-181.844 Y=29.2462 Z=0
  constraints (30):
    c: Coincident(g2,g3)
    c: Coincident(g3,g0)
    c: Symmetric(g13,g0,g4)
    c: Distance(g11,g3) = 7.2
    c: Distance(g0,g2) = 7.2
    c: Parallel(g3,g1)
    c: Parallel(g2,g0)
    c: Perpendicular(g2,g3)
    c: Coincident(g5,g6)
    c: Coincident(g6,g7)
    c: Coincident(g7,g8)
    c: Coincident(g8,g5)
    c: Symmetric(g7,g5,g9)
    c: Distance(g6,g8) = 4
    c: Distance(g5,g7) = 4
    c: Coincident(g9,g4)
    c: Parallel(g8,g6)
    c: Parallel(g7,g5)
    c: Perpendicular(g7,g8)
    c: Tangent(g8,g-3)
    c: Tangent(g2,g-4)
    c: PointOnObject(g11,g1)
    c: PointOnObject(g11,g0)
    c: Tangent(g1,g10) = -1.5708
    c: Tangent(g0,g10) = -1.5708
    c: PointOnObject(g13,g1)
    c: Tangent(g1,g12) = -1.5708
    c: Tangent(g2,g12) = -1.5708
    c: Equal(g10,g12)
    c: Coincident(g10,g5)
FEATURE [Part::Extrusion] Extrude072  label="Extrude perno per blocco switch"
  Base = -> Sketch067
  Dir = (0,-1,2e-16)
  DirMode = 2
  FaceMakerClass = Part::FaceMakerBullseye
  FaceMakerMode = 3
  LengthFwd = 25.2
  LengthRev = 0
  Solid = true
  Symmetric = true
FEATURE [Part::MultiFuse] Fusion
  Refine = true
  Shapes = -> [Extrude,Sweep,Extrude007,Extrude011,Extrude005,Extrude012,Extrude013,Extrude016,Extrude031,Extrude039,Extrude045,Extrude072]
FEATURE [Part::Cut] Cut
  Base = -> Fusion
  Refine = true
  Tool = -> Extrude001
FEATURE [Part::Cut] Cut001
  Base = -> Cut
  Refine = true
  Tool = -> Extrude004
FEATURE [Part::Cut] Cut002
  Base = -> Cut001
  Refine = true
  Tool = -> Extrude006
FEATURE [Part::Cut] Cut003
  Base = -> Cut002
  Refine = true
  Tool = -> Extrude008
FEATURE [Part::Cut] Cut004
  Base = -> Cut003
  Refine = true
  Tool = -> Extrude009
FEATURE [Part::Cut] Cut005
  Base = -> Cut004
  Refine = true
  Tool = -> Extrude010
FEATURE [Part::Cut] Cut006
  Base = -> Cut005
  Refine = true
  Tool = -> Extrude014
FEATURE [Part::Cut] Cut007
  Base = -> Cut006
  Refine = true
  Tool = -> Extrude015
FEATURE [Part::Cut] Cut008
  Base = -> Cut007
  Refine = true
  Tool = -> Extrude018
FEATURE [Part::Cut] Cut009
  Base = -> Cut008
  Refine = true
  Tool = -> Extrude019
FEATURE [Part::Cut] Cut010
  Base = -> Cut009
  Refine = true
  Tool = -> Extrude020
FEATURE [Part::Cut] Cut011
  Base = -> Cut010
  Refine = true
  Tool = -> Extrude021
FEATURE [Part::Cut] Cut012
  Base = -> Cut011
  Refine = true
  Tool = -> Extrude022
FEATURE [Part::Cut] Cut013
  Base = -> Cut012
  Refine = true
  Tool = -> Extrude023
FEATURE [Part::Cut] Cut014
  Base = -> Cut013
  Refine = true
  Tool = -> Extrude032
FEATURE [Part::Cut] Cut015
  Base = -> Cut014
  Refine = true
  Tool = -> Extrude033
FEATURE [Part::Cut] Cut016
  Base = -> Cut015
  Refine = true
  Tool = -> Extrude034
FEATURE [Part::Cut] Cut017
  Base = -> Cut016
  Refine = true
  Tool = -> Extrude035
FEATURE [Part::Cut] Cut018
  Base = -> Cut017
  Refine = true
  Tool = -> Extrude036
FEATURE [Part::Cut] Cut019
  Base = -> Cut018
  Refine = true
  Tool = -> Extrude037
FEATURE [Part::Cut] Cut020
  Base = -> Cut019
  Refine = true
  Tool = -> Extrude030
FEATURE [Part::Cut] Cut022
  Base = -> Cut020
  Refine = true
  Tool = -> Extrude038
FEATURE [Part::Cut] Cut023
  Base = -> Cut022
  Refine = true
  Tool = -> Extrude041
FEATURE [Part::Cut] Cut024
  Base = -> Cut023
  Refine = true
  Tool = -> Extrude040
FEATURE [Part::Cut] Cut025
  Base = -> Cut024
  Refine = true
  Tool = -> Extrude042
FEATURE [Part::Cut] Cut026
  Base = -> Cut025
  Refine = true
  Tool = -> Extrude043
FEATURE [Part::Cut] Cut027
  Base = -> Cut026
  Refine = true
  Tool = -> Extrude044
FEATURE [Part::Cut] Cut028
  Base = -> Cut027
  Refine = true
  Tool = -> Extrude046
FEATURE [Part::Cut] Cut029
  Base = -> Cut028
  Refine = true
  Tool = -> Extrude047
FEATURE [Part::Cut] Cut033
  Base = -> Cut029
  Refine = true
  Tool = -> Extrude055
FEATURE [Part::Cut] Cut034
  Base = -> Cut033
  Refine = true
  Tool = -> Extrude056
FEATURE [Part::Cut] Cut035
  Base = -> Cut034
  Refine = true
  Tool = -> Extrude057
FEATURE [Part::Cut] Cut037
  Base = -> Cut035
  Refine = true
  Tool = -> Extrude060
FEATURE [Part::Cut] Cut038
  Base = -> Cut037
  Refine = true
  Tool = -> Extrude061
FEATURE [Part::Cut] Cut039
  Base = -> Cut038
  Refine = true
  Tool = -> Extrude063
FEATURE [Part::Cut] Cut040
  Base = -> Cut039
  Refine = true
  Tool = -> Extrude064
FEATURE [Part::Cut] Cut041
  Base = -> Cut040
  Refine = true
  Tool = -> Extrude062
FEATURE [Sketcher::SketchObject] Sketch068  label="base con smusso sopra neopixel"
  ArcFitTolerance = 1e-06
  AttachmentSupport = -> [YZ_Plane002]
  FullyConstrained = true
  MakeInternals = false
  MapMode = 5
  Placement = pos=(0,0,0) rot=(0.57735,0.57735,0.57735;2.0944rad)
  sketch-geometry (5):
    g0: LineSegment StartX=-9.5 StartY=-6.1 StartZ=0 EndX=9.5 EndY=-6.1 EndZ=0
    g1: LineSegment StartX=9.5 StartY=-6.1 StartZ=0 EndX=9.5 EndY=6.1 EndZ=0
    g2: LineSegment StartX=9.5 StartY=6.1 StartZ=0 EndX=-9.5 EndY=6.1 EndZ=0
    g3: LineSegment StartX=-9.5 StartY=6.1 StartZ=0 EndX=-9.5 EndY=-6.1 EndZ=0
    g4: GeomPoint [constr] X=0 Y=0 Z=0
  constraints (12):
    c: Coincident(g0,g1)
    c: Coincident(g1,g2)
    c: Coincident(g2,g3)
    c: Coincident(g3,g0)
    c: Horizontal(g0)
    c: Horizontal(g2)
    c: Vertical(g1)
    c: Vertical(g3)
    c: Symmetric(g2,g0,g4)
    c: Distance(g1,g3) = 19
    c: Distance(g0,g2) = 12.2
    c: Coincident(g4,g-1)
FEATURE [Sketcher::SketchObject] Sketch069  label="cilindro minore"
  ArcFitTolerance = 1e-06
  AttachmentSupport = -> [XZ_Plane004]
  FullyConstrained = true
  MakeInternals = false
  MapMode = 5
  Placement = pos=(0,0,0) rot=(1,0,0;1.5708rad)
  sketch-geometry (1):
    g0: Circle CenterX=0 CenterY=0 CenterZ=0 NormalX=0 NormalY=0 NormalZ=1 AngleXU=0 Radius=5.8
  constraints (2):
    c: Diameter(g0) = 11.6
    c: Coincident(g0,g-1)
FEATURE [Sketcher::SketchObject] Sketch070  label="cilindro maggiore"
  ArcFitTolerance = 1e-06
  AttachmentSupport = -> [XZ_Plane004]
  ExternalGeometry = -> [Sketch069]
  FullyConstrained = true
  MakeInternals = false
  MapMode = 5
  Placement = pos=(0,0,0) rot=(1,0,0;1.5708rad)
  sketch-geometry (1):
    g0: Circle CenterX=0 CenterY=0 CenterZ=0 NormalX=0 NormalY=0 NormalZ=1 AngleXU=0 Radius=6.5
  constraints (2):
    c: Coincident(g0,g-1)
    c: Diameter(g0) = 13
FEATURE [Sketcher::SketchObject] Sketch071  label="buco interno"
  ArcFitTolerance = 1e-06
  AttachmentSupport = -> [XZ_Plane004]
  ExternalGeometry = -> [Sketch069]
  FullyConstrained = true
  MakeInternals = false
  MapMode = 5
  Placement = pos=(0,0,0) rot=(1,0,0;1.5708rad)
  sketch-geometry (1):
    g0: Circle CenterX=0 CenterY=0 CenterZ=0 NormalX=0 NormalY=0 NormalZ=1 AngleXU=0 Radius=5
  constraints (2):
    c: Coincident(g0,g-1)
    c: Diameter(g0) = 10
FEATURE [PartDesign::Pad] Pad
  Direction = (0,-1,2e-16)
  Length = 1.2
  Length2 = 10
  Placement = pos=(0,0,0) rot=(1,0,0;1.5708rad)
  Profile = -> Sketch070
  ReferenceAxis = -> Sketch070 [N_Axis]
  Refine = true
  Suppressed = false
  Type = 0
FEATURE [PartDesign::Pad] Pad001
  BaseFeature = -> Pad
  Direction = (0,-1,2e-16)
  Length = 5.6
  Length2 = 10
  Placement = pos=(0,0,0) rot=(1,0,0;1.5708rad)
  Profile = -> Sketch069
  ReferenceAxis = -> Sketch069 [N_Axis]
  Refine = true
  Suppressed = false
  Type = 0
FEATURE [PartDesign::Pocket] Pocket
  BaseFeature = -> Pad001
  Direction = (0,1,-2e-16)
  Length = 7
  Length2 = 5
  Midplane = true
  Placement = pos=(0,0,0) rot=(1,0,0;1.5708rad)
  Profile = -> Sketch071
  ReferenceAxis = -> Sketch071 [N_Axis]
  Refine = true
  Suppressed = false
  Type = 0
FEATURE [PartDesign::Fillet] Fillet
  Base = -> Pocket [Face7]
  BaseFeature = -> Pocket
  Placement = pos=(0,0,0) rot=(1,0,0;1.5708rad)
  Radius = 1
  Refine = true
  SupportTransform = false
  Suppressed = false
  UseAllEdges = false
FEATURE [PartDesign::Body] Body004  label="pulsanti lato sinistro"
  AllowCompound = false
  Group = -> [Sketch069,Sketch070,Sketch071,Pad,Pad001,Pocket,Fillet]
  Origin = -> Origin004
  Tip = -> Fillet
FEATURE [Sketcher::SketchObject] Sketch072  label="buco per saldature e diodo driver solenoide"
  ArcFitTolerance = 1e-06
  AttachmentSupport = -> [XZ_Plane]
  ExternalGeometry = -> [Sketch038]
  FullyConstrained = true
  MakeInternals = false
  MapMode = 5
  Placement = pos=(0,0,0) rot=(1,0,0;1.5708rad)
  sketch-geometry (4):
    g0: LineSegment StartX=-212.269 StartY=-43.9083 StartZ=0 EndX=-207.197 EndY=-33.0326 EndZ=0
    g1: LineSegment StartX=-207.197 StartY=-33.0326 StartZ=0 EndX=-207.56 EndY=-32.8635 EndZ=0
    g2: LineSegment StartX=-207.56 StartY=-32.8635 StartZ=0 EndX=-212.631 EndY=-43.7392 EndZ=0
    g3: LineSegment StartX=-212.631 StartY=-43.7392 StartZ=0 EndX=-212.269 EndY=-43.9083 EndZ=0
  constraints (11):
    c: Coincident(g1,g0)
    c: Coincident(g2,g1)
    c: Coincident(g3,g2)
    c: Coincident(g3,g0)
    c: Parallel(g-3,g0)
    c: Parallel(g0,g2)
    c: Perpendicular(g0,g3)
    c: Perpendicular(g1,g0)
    c: Distance(g3) = 0.4
    c: Distance(g2) = 12
    c: Coincident(g0,g-3)
FEATURE [Part::Extrusion] Extrude074  label="Extrude buco per saldature e diodo driver solenoide"
  Base = -> Sketch072
  Dir = (0,-1,2e-16)
  DirMode = 2
  FaceMakerClass = Part::FaceMakerBullseye
  FaceMakerMode = 3
  LengthFwd = 14.6
  LengthRev = 0
  Solid = true
  Symmetric = true
FEATURE [Part::Cut] Cut042
  Base = -> Cut041
  Refine = true
  Tool = -> Extrude074
FEATURE [Sketcher::SketchObject] Sketch073  label="fori slargati blocco solenoide"
  ArcFitTolerance = 1e-06
  AttachmentSupport = -> [XY_Plane]
  ExternalGeometry = -> [Sketch030]
  FullyConstrained = true
  MakeInternals = false
  MapMode = 5
  sketch-geometry (2):
    g0: Circle CenterX=-152.209 CenterY=6.95 CenterZ=0 NormalX=0 NormalY=0 NormalZ=1 AngleXU=0 Radius=3.7
    g1: Circle CenterX=-130.41 CenterY=-6.95 CenterZ=0 NormalX=0 NormalY=0 NormalZ=1 AngleXU=0 Radius=3.7
  constraints (4):
    c: Diameter(g0) = 7.4
    c: Coincident(g0,g-3)
    c: Diameter(g1) = 7.4
    c: Coincident(g1,g-4)
FEATURE [Part::Extrusion] Extrude075  label="Extrude fori slargati blocco solenoide"
  Base = -> Sketch073
  Dir = (0,0,1)
  DirMode = 2
  FaceMakerClass = Part::FaceMakerBullseye
  FaceMakerMode = 3
  LengthFwd = 1.5
  LengthRev = 0
  Placement = pos=(0,0,36.4) rot=(0,0,1;0rad)
  Solid = true
  Symmetric = false
FEATURE [Part::Cut] Cut043
  Base = -> Cut042
  Refine = true
  Tool = -> Extrude075
FEATURE [Sketcher::SketchObject] Sketch074  label="lato sx pistola"
  ArcFitTolerance = 1e-06
  AttachmentSupport = -> [XZ_Plane]
  ExternalGeometry = -> [Sketch016,Sketch,Sketch058]
  FullyConstrained = true
  MakeInternals = false
  MapMode = 5
  Placement = pos=(0,0,0) rot=(1,0,0;1.5708rad)
  sketch-geometry (37):
    g0: LineSegment StartX=-82.8 StartY=3.2 StartZ=0 EndX=0 EndY=3.2 EndZ=0
    g1: LineSegment StartX=-82.8 StartY=3.2 StartZ=0 EndX=-82.8 EndY=6.2 EndZ=0
    g2: LineSegment [constr] StartX=-107.6 StartY=18 StartZ=0 EndX=-107.6 EndY=20 EndZ=0
    g3: LineSegment [constr] StartX=-132.428 StartY=18 StartZ=0 EndX=-132.428 EndY=20 EndZ=0
    g4: LineSegment StartX=-132.428 StartY=20 StartZ=0 EndX=-107.6 EndY=20 EndZ=0
    g5: ArcOfCircle CenterX=-107.6 CenterY=4 CenterZ=0 NormalX=0 NormalY=0 NormalZ=1 AngleXU=0 Radius=16 StartAngle=0.137937 EndAngle=1.5708
    g6: LineSegment StartX=-82.8 StartY=6.2 StartZ=0 EndX=-91.752 EndY=6.2 EndZ=0
    g7: LineSegment [constr] StartX=-145.743 StartY=8.32624 StartZ=0 EndX=-147.645 EndY=8.94427 EndZ=0
    g8: ArcOfCircle CenterX=-132.428 CenterY=4 CenterZ=0 NormalX=0 NormalY=0 NormalZ=1 AngleXU=0 Radius=16 StartAngle=1.5708 EndAngle=2.82743
    g9: LineSegment StartX=-215.932 StartY=-80.4316 StartZ=0 EndX=-176.685 EndY=-80.4316 EndZ=0
    g10: LineSegment StartX=-147.645 StartY=8.94427 StartZ=0 EndX=-176.685 EndY=-80.4316 EndZ=0
    g11: LineSegment [constr] StartX=-193.988 StartY=-2.33927 StartZ=0 EndX=-192.176 EndY=-3.18451 EndZ=0
    g12: LineSegment [constr] StartX=-217.232 StartY=-52.1862 StartZ=0 EndX=-215.42 EndY=-53.0314 EndZ=0
    g13: LineSegment StartX=-192.176 StartY=-3.18451 StartZ=0 EndX=-215.42 EndY=-53.0314 EndZ=0
    g14: ArcOfCircle CenterX=-184.801 CenterY=-67.3089 CenterZ=0 NormalX=0 NormalY=0 NormalZ=1 AngleXU=0 Radius=33.7833 StartAngle=2.70526 EndAngle=3.54053
    g15: ArcOfCircle CenterX=-207.583 CenterY=4 CenterZ=0 NormalX=0 NormalY=0 NormalZ=1 AngleXU=0 Radius=17 StartAngle=5.84685 EndAngle=7.56663
    g16: LineSegment StartX=-202.765 StartY=20.303 StartZ=0 EndX=-195.887 EndY=39.2 EndZ=0
    g17: LineSegment [constr] StartX=-193.885 StartY=33.0037 StartZ=0 EndX=-197.644 EndY=34.3718 EndZ=0
    g18: LineSegment StartX=-195.887 StartY=39.2 StartZ=0 EndX=0 EndY=39.2 EndZ=0
    g19: LineSegment StartX=0 StartY=3.2 StartZ=0 EndX=0 EndY=39.2 EndZ=0
    g20: LineSegment StartX=-189.939 StartY=31.5672 StartZ=0 EndX=-192.333 EndY=24.9893 EndZ=0
    g21: LineSegment StartX=-196.467 StartY=26.4942 StartZ=0 EndX=-194.073 EndY=33.0721 EndZ=0
    g22: Circle CenterX=-213.443 CenterY=-76.8316 CenterZ=0 NormalX=0 NormalY=0 NormalZ=1 AngleXU=0 Radius=1.8
    g23: Circle CenterX=-179.305 CenterY=-76.8316 CenterZ=0 NormalX=0 NormalY=0 NormalZ=1 AngleXU=0 Radius=1.8
    g24: Circle CenterX=-184.08 CenterY=34.8 CenterZ=0 NormalX=0 NormalY=0 NormalZ=1 AngleXU=0 Radius=1.8
    g25: Circle CenterX=-78.51 CenterY=34.8 CenterZ=0 NormalX=0 NormalY=0 NormalZ=1 AngleXU=0 Radius=1.8
    g26: Circle CenterX=-78.51 CenterY=7.6 CenterZ=0 NormalX=0 NormalY=0 NormalZ=1 AngleXU=0 Radius=1.8
    g27: Circle CenterX=-5.6 CenterY=34.8 CenterZ=0 NormalX=0 NormalY=0 NormalZ=1 AngleXU=0 Radius=1.8
    g28: Circle CenterX=-5.6 CenterY=7.6 CenterZ=0 NormalX=0 NormalY=0 NormalZ=1 AngleXU=0 Radius=1.8
    g29: LineSegment StartX=-190.127 StartY=31.6356 StartZ=0 EndX=-189.939 EndY=31.5672 EndZ=0
    g30: LineSegment StartX=-194.073 StartY=33.0721 StartZ=0 EndX=-193.885 EndY=33.0037 EndZ=0
    g31: LineSegment StartX=-193.885 StartY=33.0037 StartZ=0 EndX=-190.127 EndY=31.6356 EndZ=0
    g32: LineSegment StartX=-196.467 StartY=26.4942 StartZ=0 EndX=-192.333 EndY=24.9893 EndZ=0
    g33: Circle CenterX=-19 CenterY=21.2 CenterZ=0 NormalX=0 NormalY=0 NormalZ=1 AngleXU=0 Radius=6.3
    g34: Circle CenterX=-42 CenterY=21.2 CenterZ=0 NormalX=0 NormalY=0 NormalZ=1 AngleXU=0 Radius=6.3
    g35: Circle CenterX=-65 CenterY=21.2 CenterZ=0 NormalX=0 NormalY=0 NormalZ=1 AngleXU=0 Radius=6.3
    g36: LineSegment [constr] StartX=-4 StartY=21.2 StartZ=0 EndX=-65 EndY=21.2 EndZ=0
  constraints (96):
    c: Coincident(g0,g-41)
    c: Horizontal(g0)
    c: PointOnObject(g0,g-39)
    c: Coincident(g1,g0)
    c: Vertical(g1)
    c: DistanceY(g1,g1) = 3
    c: Coincident(g2,g-17)
    c: Vertical(g2)
    c: Coincident(g3,g-16)
    c: Vertical(g3)
    c: DistanceY(g2,g2) = 2
    c: DistanceY(g3,g3) = 2
    c: Coincident(g4,g3)
    c: Coincident(g4,g2)
    c: Coincident(g5,g-17)
    c: Coincident(g5,g2)
    c: Coincident(g6,g1)
    c: Horizontal(g6)
    c: Coincident(g6,g5)
    c: Coincident(g7,g-15)
    c: Coincident(g8,g7)
    c: Coincident(g8,g3)
    c: Coincident(g8,g-15)
    c: Horizontal(g9)
    c: DistanceY(g-13,g9) = 2
    c: Coincident(g10,g7)
    c: Parallel(g10,g-14)
    c: Coincident(g9,g10)
    c: Distance(g11) = 2
    c: Coincident(g11,g-11)
    c: Perpendicular(g-11,g11)
    c: Distance(g12) = 2
    c: Coincident(g12,g-12)
    c: Perpendicular(g-11,g12)
    c: Coincident(g13,g11)
    c: Coincident(g13,g12)
    c: Coincident(g14,g-32)
    c: Coincident(g14,g12)
    c: Coincident(g14,g9)
    c: Coincident(g15,g-10)
    c: Coincident(g15,g11)
    c: Parallel(g16,g-22)
    c: Distance(g17) = 4
    c: PointOnObject(g17,g16)
    c: Coincident(g15,g16)
    c: Horizontal(g18)
    c: Coincident(g18,g16)
    c: Coincident(g19,g0)
    c: PointOnObject(g19,g-39)
    c: DistanceY(g19,g-36) = 2
    c: Coincident(g18,g19)
    c: Diameter(g22) = 3.6
    c: Coincident(g22,g-9)
    c: Diameter(g23) = 3.6
    c: Coincident(g23,g-8)
    c: Diameter(g24) = 3.6
    c: Diameter(g25) = 3.6
    c: Diameter(g26) = 3.6
    c: Diameter(g27) = 3.6
    c: Diameter(g28) = 3.6
    c: Coincident(g27,g-4)
    c: Coincident(g28,g-3)
    c: Coincident(g25,g-6)
    c: Coincident(g26,g-5)
    c: Coincident(g24,g-7)
    c: Parallel(g20,g-21)
    c: Equal(g20,g-21)
    c: Parallel(g21,g-19)
    c: Equal(g21,g-19)
    c: Distance(g29) = 0.2
    c: Distance(g30) = 0.2
    c: Parallel(g29,g-20)
    c: Parallel(g31,g-20)
    c: Equal(g31,g-20)
    c: Coincident(g30,g31)
    c: Coincident(g31,g29)
    c: Coincident(g29,g-21)
    c: Parallel(g30,g31)
    c: Coincident(g17,g30)
    c: Coincident(g20,g29)
    c: Coincident(g21,g30)
    c: Perpendicular(g16,g17)
    c: Coincident(g32,g21)
    c: Coincident(g32,g20)
    c: Perpendicular(g10,g7)
    c: Diameter(g33) = 12.6
    c: Diameter(g34) = 12.6
    c: Diameter(g35) = 12.6
    c: Horizontal(g36)
    c: PointOnObject(g33,g36)
    c: PointOnObject(g34,g36)
    c: DistanceX(g34,g33) = 23
    c: DistanceX(g35,g34) = 23
    c: DistanceX(g33,g36) = 15
    c: Symmetric(g-24,g-24,g36)
    c: Coincident(g36,g35)
FEATURE [Sketcher::SketchObject] Sketch075  label="lato dx pistola"
  ArcFitTolerance = 1e-06
  AttachmentSupport = -> [XZ_Plane]
  ExternalGeometry = -> [Sketch016,Sketch,Sketch058,Sketch074]
  FullyConstrained = true
  MakeInternals = false
  MapMode = 5
  Placement = pos=(0,0,0) rot=(1,0,0;1.5708rad)
  sketch-geometry (61):
    g0: LineSegment StartX=-82.8 StartY=3.2 StartZ=0 EndX=0 EndY=3.2 EndZ=0
    g1: LineSegment StartX=-82.8 StartY=3.2 StartZ=0 EndX=-82.8 EndY=6.2 EndZ=0
    g2: LineSegment [constr] StartX=-107.6 StartY=18 StartZ=0 EndX=-107.6 EndY=20 EndZ=0
    g3: LineSegment [constr] StartX=-132.428 StartY=18 StartZ=0 EndX=-132.428 EndY=20 EndZ=0
    g4: LineSegment StartX=-132.428 StartY=20 StartZ=0 EndX=-107.6 EndY=20 EndZ=0
    g5: ArcOfCircle CenterX=-107.6 CenterY=4 CenterZ=0 NormalX=0 NormalY=0 NormalZ=1 AngleXU=0 Radius=16 StartAngle=0.137937 EndAngle=1.5708
    g6: LineSegment StartX=-82.8 StartY=6.2 StartZ=0 EndX=-91.752 EndY=6.2 EndZ=0
    g7: LineSegment [constr] StartX=-145.743 StartY=8.32624 StartZ=0 EndX=-147.645 EndY=8.94427 EndZ=0
    g8: ArcOfCircle CenterX=-132.428 CenterY=4 CenterZ=0 NormalX=0 NormalY=0 NormalZ=1 AngleXU=0 Radius=16 StartAngle=1.5708 EndAngle=2.82743
    g9: LineSegment StartX=-215.932 StartY=-80.4316 StartZ=0 EndX=-176.685 EndY=-80.4316 EndZ=0
    g10: LineSegment StartX=-147.645 StartY=8.94427 StartZ=0 EndX=-176.685 EndY=-80.4316 EndZ=0
    g11: LineSegment [constr] StartX=-193.988 StartY=-2.33927 StartZ=0 EndX=-192.176 EndY=-3.18451 EndZ=0
    g12: LineSegment [constr] StartX=-217.232 StartY=-52.1862 StartZ=0 EndX=-215.42 EndY=-53.0314 EndZ=0
    g13: LineSegment StartX=-192.176 StartY=-3.18451 StartZ=0 EndX=-215.42 EndY=-53.0314 EndZ=0
    g14: ArcOfCircle CenterX=-184.801 CenterY=-67.3089 CenterZ=0 NormalX=0 NormalY=0 NormalZ=1 AngleXU=0 Radius=33.7833 StartAngle=2.70526 EndAngle=3.54053
    g15: ArcOfCircle CenterX=-207.583 CenterY=4 CenterZ=0 NormalX=0 NormalY=0 NormalZ=1 AngleXU=0 Radius=17 StartAngle=5.84685 EndAngle=7.56663
    g16: LineSegment StartX=-202.765 StartY=20.303 StartZ=0 EndX=-195.887 EndY=39.2 EndZ=0
    g17: LineSegment [constr] StartX=-193.885 StartY=33.0037 StartZ=0 EndX=-197.644 EndY=34.3718 EndZ=0
    g18: LineSegment StartX=-195.887 StartY=39.2 StartZ=0 EndX=0 EndY=39.2 EndZ=0
    g19: LineSegment StartX=0 StartY=3.2 StartZ=0 EndX=0 EndY=39.2 EndZ=0
    g20: LineSegment StartX=-189.939 StartY=31.5672 StartZ=0 EndX=-192.333 EndY=24.9893 EndZ=0
    g21: LineSegment StartX=-196.467 StartY=26.4942 StartZ=0 EndX=-194.073 EndY=33.0721 EndZ=0
    g22: Circle CenterX=-213.443 CenterY=-76.8316 CenterZ=0 NormalX=0 NormalY=0 NormalZ=1 AngleXU=0 Radius=1.8
    g23: Circle CenterX=-179.305 CenterY=-76.8316 CenterZ=0 NormalX=0 NormalY=0 NormalZ=1 AngleXU=0 Radius=1.8
    g24: Circle CenterX=-184.08 CenterY=34.8 CenterZ=0 NormalX=0 NormalY=0 NormalZ=1 AngleXU=0 Radius=1.8
    g25: Circle CenterX=-78.51 CenterY=34.8 CenterZ=0 NormalX=0 NormalY=0 NormalZ=1 AngleXU=0 Radius=1.8
    g26: Circle CenterX=-78.51 CenterY=7.6 CenterZ=0 NormalX=0 NormalY=0 NormalZ=1 AngleXU=0 Radius=1.8
    g27: Circle CenterX=-5.6 CenterY=34.8 CenterZ=0 NormalX=0 NormalY=0 NormalZ=1 AngleXU=0 Radius=1.8
    g28: Circle CenterX=-5.6 CenterY=7.6 CenterZ=0 NormalX=0 NormalY=0 NormalZ=1 AngleXU=0 Radius=1.8
    g29: LineSegment StartX=-190.127 StartY=31.6356 StartZ=0 EndX=-189.939 EndY=31.5672 EndZ=0
    g30: LineSegment StartX=-194.073 StartY=33.0721 StartZ=0 EndX=-193.885 EndY=33.0037 EndZ=0
    g31: LineSegment StartX=-193.885 StartY=33.0037 StartZ=0 EndX=-190.127 EndY=31.6356 EndZ=0
    g32: LineSegment StartX=-196.467 StartY=26.4942 StartZ=0 EndX=-192.333 EndY=24.9893 EndZ=0
    g33: LineSegment [constr] StartX=-4 StartY=21.2 StartZ=0 EndX=-87.91 EndY=21.2 EndZ=0
    g34: GeomPoint [constr] X=-4 Y=21.2 Z=0
    g35: LineSegment [constr] StartX=-15.2 StartY=33.7 StartZ=0 EndX=-15.2 EndY=8.7 EndZ=0
    g36: LineSegment [constr] StartX=-15.2 StartY=33.7 StartZ=0 EndX=-56.2 EndY=33.7 EndZ=0
    g37: LineSegment [constr] StartX=-15.2 StartY=8.7 StartZ=0 EndX=-56.2 EndY=8.7 EndZ=0
    g38: LineSegment [constr] StartX=-56.2 StartY=33.7 StartZ=0 EndX=-56.2 EndY=8.7 EndZ=0
    g39: Circle CenterX=-18.6 CenterY=30.3 CenterZ=0 NormalX=0 NormalY=0 NormalZ=1 AngleXU=0 Radius=3.4
    g40: Circle CenterX=-18.6 CenterY=12.1 CenterZ=0 NormalX=0 NormalY=0 NormalZ=1 AngleXU=0 Radius=3.4
    g41: Circle CenterX=-43.2 CenterY=30.3 CenterZ=0 NormalX=0 NormalY=0 NormalZ=1 AngleXU=0 Radius=3.4
    g42: Circle CenterX=-43.2 CenterY=12.1 CenterZ=0 NormalX=0 NormalY=0 NormalZ=1 AngleXU=0 Radius=3.4
    g43: LineSegment [constr] StartX=-4 StartY=21.2 StartZ=0 EndX=-15.2 EndY=21.2 EndZ=0
    g44: LineSegment [constr] StartX=-15.2 StartY=21.2 StartZ=0 EndX=-36.2 EndY=21.2 EndZ=0
    g45: LineSegment [constr] StartX=-41.5 StartY=16.2 StartZ=0 EndX=-30.9 EndY=16.2 EndZ=0
    g46: LineSegment [constr] StartX=-30.9 StartY=16.2 StartZ=0 EndX=-30.9 EndY=26.2 EndZ=0
    g47: LineSegment [constr] StartX=-30.9 StartY=26.2 StartZ=0 EndX=-41.5 EndY=26.2 EndZ=0
    g48: LineSegment [constr] StartX=-41.5 StartY=26.2 StartZ=0 EndX=-41.5 EndY=16.2 EndZ=0
    g49: GeomPoint [constr] X=-36.2 Y=21.2 Z=0
    g50: Circle CenterX=-36.2 CenterY=21.2 CenterZ=0 NormalX=0 NormalY=0 NormalZ=1 AngleXU=0 Radius=2.8
    g51: LineSegment [constr] StartX=-24.2 StartY=26.7 StartZ=0 EndX=-24.2 EndY=15.7 EndZ=0
    g52: Circle CenterX=-24.2 CenterY=26.7 CenterZ=0 NormalX=0 NormalY=0 NormalZ=1 AngleXU=0 Radius=3
    g53: Circle CenterX=-24.2 CenterY=15.7 CenterZ=0 NormalX=0 NormalY=0 NormalZ=1 AngleXU=0 Radius=3
    g54: GeomPoint X=-18.6 Y=30.3 Z=0
    g55: GeomPoint X=-18.6 Y=12.1 Z=0
    g56: GeomPoint X=-43.2 Y=12.1 Z=0
    g57: GeomPoint X=-43.2 Y=30.3 Z=0
    g58: Circle CenterX=-65 CenterY=21.2 CenterZ=0 NormalX=0 NormalY=0 NormalZ=1 AngleXU=0 Radius=1.5
    g59: Circle CenterX=-42 CenterY=21.2 CenterZ=0 NormalX=0 NormalY=0 NormalZ=1 AngleXU=0 Radius=1.5
    g60: Circle CenterX=-19 CenterY=21.2 CenterZ=0 NormalX=0 NormalY=0 NormalZ=1 AngleXU=0 Radius=1.5
  constraints (149):
    c: Coincident(g0,g-41)
    c: Horizontal(g0)
    c: PointOnObject(g0,g-39)
    c: Coincident(g1,g0)
    c: Vertical(g1)
    c: DistanceY(g1,g1) = 3
    c: Coincident(g2,g-17)
    c: Vertical(g2)
    c: Coincident(g3,g-16)
    c: Vertical(g3)
    c: DistanceY(g2,g2) = 2
    c: DistanceY(g3,g3) = 2
    c: Coincident(g4,g3)
    c: Coincident(g4,g2)
    c: Coincident(g5,g-17)
    c: Coincident(g5,g2)
    c: Coincident(g6,g1)
    c: Horizontal(g6)
    c: Coincident(g6,g5)
    c: Coincident(g7,g-15)
    c: Coincident(g8,g7)
    c: Coincident(g8,g3)
    c: Coincident(g8,g-15)
    c: Horizontal(g9)
    c: DistanceY(g-13,g9) = 2
    c: Coincident(g10,g7)
    c: Parallel(g10,g-14)
    c: Coincident(g9,g10)
    c: Distance(g11) = 2
    c: Coincident(g11,g-11)
    c: Perpendicular(g-11,g11)
    c: Distance(g12) = 2
    c: Coincident(g12,g-12)
    c: Perpendicular(g-11,g12)
    c: Coincident(g13,g11)
    c: Coincident(g13,g12)
    c: Coincident(g14,g-32)
    c: Coincident(g14,g12)
    c: Coincident(g14,g9)
    c: Coincident(g15,g-10)
    c: Coincident(g15,g11)
    c: Parallel(g16,g-22)
    c: Distance(g17) = 4
    c: PointOnObject(g17,g16)
    c: Coincident(g15,g16)
    c: Horizontal(g18)
    c: Coincident(g18,g16)
    c: Coincident(g19,g0)
    c: PointOnObject(g19,g-39)
    c: DistanceY(g19,g-36) = 2
    c: Coincident(g18,g19)
    c: Diameter(g22) = 3.6
    c: Coincident(g22,g-9)
    c: Diameter(g23) = 3.6
    c: Coincident(g23,g-8)
    c: Diameter(g24) = 3.6
    c: Diameter(g25) = 3.6
    c: Diameter(g26) = 3.6
    c: Diameter(g27) = 3.6
    c: Diameter(g28) = 3.6
    c: Coincident(g27,g-4)
    c: Coincident(g28,g-3)
    c: Coincident(g25,g-6)
    c: Coincident(g26,g-5)
    c: Coincident(g24,g-7)
    c: Parallel(g20,g-21)
    c: Equal(g20,g-21)
    c: Parallel(g21,g-19)
    c: Equal(g21,g-19)
    c: Distance(g29) = 0.2
    c: Distance(g30) = 0.2
    c: Parallel(g29,g-20)
    c: Parallel(g31,g-20)
    c: Equal(g31,g-20)
    c: Coincident(g30,g31)
    c: Coincident(g31,g29)
    c: Coincident(g29,g-21)
    c: Parallel(g30,g31)
    c: Coincident(g17,g30)
    c: Coincident(g20,g29)
    c: Coincident(g21,g30)
    c: Perpendicular(g16,g17)
    c: Coincident(g32,g21)
    c: Coincident(g32,g20)
    c: Perpendicular(g10,g7)
    c: Horizontal(g33)
    c: Symmetric(g-24,g-24,g33)
    c: PointOnObject(g33,g-28)
    c: Symmetric(g-24,g-24,g34)
    c: DistanceY(g35,g35) = 25
    c: Symmetric(g35,g35,g33)
    c: Distance(g36) = 41
    c: Coincident(g36,g35)
    c: Horizontal(g36)
    c: Coincident(g37,g35)
    c: Horizontal(g37)
    c: Coincident(g38,g36)
    c: Vertical(g38)
    c: Coincident(g37,g38)
    c: Diameter(g39) = 6.8
    c: Diameter(g40) = 6.8
    c: Tangent(g39,g36)
    c: Tangent(g40,g37)
    c: Tangent(g39,g35)
    c: Tangent(g40,g35)
    c: Diameter(g41) = 6.8
    c: Diameter(g42) = 6.8
    c: Tangent(g41,g36)
    c: Tangent(g42,g37)
    c: DistanceX(g41,g39) = 24.6
    c: DistanceX(g42,g40) = 24.6
    c: Distance(g43) = 11.2
    c: Coincident(g43,g33)
    c: PointOnObject(g43,g33)
    c: PointOnObject(g43,g35)
    c: Distance(g44) = 21
    c: Coincident(g44,g43)
    c: PointOnObject(g44,g33)
    c: Coincident(g45,g46)
    c: Coincident(g46,g47)
    c: Coincident(g47,g48)
    c: Coincident(g48,g45)
    c: Horizontal(g45)
    c: Horizontal(g47)
    c: Vertical(g46)
    c: Vertical(g48)
    c: Symmetric(g47,g45,g49)
    c: Distance(g46,g48) = 10.6
    c: Distance(g45,g47) = 10
    c: Coincident(g49,g44)
    c: Diameter(g50) = 5.6
    c: Coincident(g50,g44)
    c: Distance(g51) = 11
    c: Symmetric(g51,g51,g33)
    c: DistanceX(g51,g43) = 9
    c: Diameter(g52) = 6
    c: Coincident(g52,g51)
    c: Diameter(g53) = 6
    c: Coincident(g53,g51)
    c: Coincident(g40,g55)
    c: Coincident(g39,g54)
    c: Coincident(g41,g57)
    c: Coincident(g42,g56)
    c: Diameter(g58) = 3
    c: Diameter(g59) = 3
    c: Diameter(g60) = 3
    c: Coincident(g58,g-44)
    c: Coincident(g59,g-46)
    c: Coincident(g60,g-45)
FEATURE [Sketcher::SketchObject] Sketch078
  ArcFitTolerance = 1e-06
  AttachmentSupport = -> [XZ_Plane005]
  FullyConstrained = true
  MakeInternals = false
  MapMode = 5
  Placement = pos=(0,0,0) rot=(1,0,0;1.5708rad)
  sketch-geometry (5):
    g0: LineSegment [constr] StartX=0 StartY=5.5 StartZ=0 EndX=0 EndY=-5.5 EndZ=0
    g1: ArcOfCircle CenterX=0 CenterY=5.5 CenterZ=0 NormalX=0 NormalY=0 NormalZ=1 AngleXU=0 Radius=2.7 StartAngle=0 EndAngle=3.14159
    g2: ArcOfCircle CenterX=0 CenterY=-5.5 CenterZ=0 NormalX=0 NormalY=0 NormalZ=1 AngleXU=0 Radius=2.7 StartAngle=3.1416 EndAngle=6.28318
    g3: LineSegment StartX=-2.7 StartY=5.5 StartZ=0 EndX=-2.7 EndY=-5.50001 EndZ=0
    g4: LineSegment StartX=2.7 StartY=5.5 StartZ=0 EndX=2.7 EndY=-5.50001 EndZ=0
  constraints (13):
    c: Distance(g0) = 11
    c: Vertical(g0)
    c: Symmetric(g0,g0,g-1)
    c: Radius(g1) = 2.7
    c: Coincident(g1,g0)
    c: Radius(g2) = 2.7
    c: Coincident(g2,g0)
    c: Vertical(g3)
    c: Vertical(g4)
    c: Coincident(g2,g4)
    c: Coincident(g2,g3)
    c: Tangent(g3,g1) = -1.5708
    c: Tangent(g4,g1) = 1.5708
FEATURE [PartDesign::Pad] Pad002
  Direction = (0,-1,2e-16)
  Length = 0.8
  Length2 = 10
  Placement = pos=(0,0,0) rot=(1,0,0;1.5708rad)
  Profile = -> Sketch078
  ReferenceAxis = -> Sketch078 [N_Axis]
  Refine = true
  Suppressed = false
  Type = 0
FEATURE [Sketcher::SketchObject] Sketch079
  ArcFitTolerance = 1e-06
  AttachmentSupport = -> [XZ_Plane005]
  ExternalGeometry = -> [Sketch078]
  FullyConstrained = true
  MakeInternals = false
  MapMode = 5
  Placement = pos=(0,0,0) rot=(1,0,0;1.5708rad)
  sketch-geometry (2):
    g0: Circle CenterX=-1e-16 CenterY=5.5 CenterZ=0 NormalX=0 NormalY=0 NormalZ=1 AngleXU=0 Radius=2.7
    g1: Circle CenterX=0 CenterY=-5.5 CenterZ=0 NormalX=0 NormalY=0 NormalZ=1 AngleXU=0 Radius=2.7
  constraints (4):
    c: Coincident(g0,g-3)
    c: PointOnObject(g-3,g0)
    c: Coincident(g1,g-4)
    c: Equal(g1,g-4)
FEATURE [PartDesign::Pad] Pad003
  BaseFeature = -> Pad002
  Direction = (0,-1,2e-16)
  Length = 5
  Length2 = 10
  Placement = pos=(0,0,0) rot=(1,0,0;1.5708rad)
  Profile = -> Sketch079
  ReferenceAxis = -> Sketch079 [N_Axis]
  Refine = true
  Suppressed = false
  Type = 0
FEATURE [PartDesign::Fillet] Fillet001
  Base = -> Pad003 [Edge16,Edge14]
  BaseFeature = -> Pad003
  Placement = pos=(0,0,0) rot=(1,0,0;1.5708rad)
  Radius = 0.4
  Refine = true
  SupportTransform = false
  Suppressed = false
  UseAllEdges = false
FEATURE [PartDesign::Body] Body005  label="pulsanti lato destro"
  AllowCompound = false
  Group = -> [Sketch078,Pad002,Sketch079,Pad003,Fillet001]
  Origin = -> Origin005
  Tip = -> Fillet001
FEATURE [PartDesign::SubShapeBinder] Binder
  BindCopyOnChange = 0
  BindMode = 0
  ClaimChildren = false
  Context = -> Body006 [Binder.]
  Fuse = false
  MakeFace = true
  OffsetFill = false
  OffsetIntersection = false
  OffsetJoinType = 0
  OffsetOpenResult = false
  PartialLoad = false
  Refine = true
  Relative = true
  Support = -> [Body[Sketch074.]]
  _Version = 2
FEATURE [PartDesign::SubShapeBinder] Binder001
  BindCopyOnChange = 0
  BindMode = 0
  ClaimChildren = false
  Context = -> Body007 [Binder001.]
  Fuse = false
  MakeFace = true
  OffsetFill = false
  OffsetIntersection = false
  OffsetJoinType = 0
  OffsetOpenResult = false
  PartialLoad = false
  Refine = true
  Relative = true
  Support = -> [Body[Sketch075.]]
  _Version = 2
FEATURE [Mesh::Feature] logo_per_PCB_definitivo_positivo
  Placement = pos=(-191,17,-66) rot=(0,1,1;0rad)
FEATURE [Sketcher::SketchObject] Sketch114  label="Sketch114 - base lato DX"
  ArcFitTolerance = 1e-06
  AttachmentSupport = -> [Binder001]
  ExternalGeometry = -> [Binder001]
  FullyConstrained = true
  MakeInternals = false
  MapMode = 5
  Placement = pos=(0,1e-15,0) rot=(0,0.707107,0.707107;3.14159rad)
  sketch-geometry (30):
    g0: Circle CenterX=5.6 CenterY=34.8 CenterZ=0 NormalX=0 NormalY=0 NormalZ=1 AngleXU=0 Radius=1.8
    g1: Circle CenterX=5.6 CenterY=7.6 CenterZ=0 NormalX=0 NormalY=0 NormalZ=1 AngleXU=0 Radius=1.8
    g2: Circle CenterX=24.2 CenterY=26.7 CenterZ=0 NormalX=0 NormalY=0 NormalZ=1 AngleXU=0 Radius=3
    g3: Circle CenterX=24.2 CenterY=15.7 CenterZ=0 NormalX=0 NormalY=0 NormalZ=1 AngleXU=0 Radius=3
    g4: Circle CenterX=36.2 CenterY=21.2 CenterZ=0 NormalX=0 NormalY=0 NormalZ=1 AngleXU=0 Radius=2.8
    g5: Circle CenterX=78.51 CenterY=34.8 CenterZ=0 NormalX=0 NormalY=0 NormalZ=1 AngleXU=0 Radius=1.8
    g6: Circle CenterX=78.51 CenterY=7.6 CenterZ=0 NormalX=0 NormalY=0 NormalZ=1 AngleXU=0 Radius=1.8
    g7: Circle CenterX=184.08 CenterY=34.8 CenterZ=0 NormalX=0 NormalY=0 NormalZ=1 AngleXU=0 Radius=1.8
    g8: Circle CenterX=213.443 CenterY=-76.8316 CenterZ=0 NormalX=0 NormalY=0 NormalZ=1 AngleXU=0 Radius=1.8
    g9: Circle CenterX=179.305 CenterY=-76.8316 CenterZ=0 NormalX=0 NormalY=0 NormalZ=1 AngleXU=0 Radius=1.8
    g10: ArcOfCircle [constr] CenterX=132.428 CenterY=4 CenterZ=0 NormalX=0 NormalY=0 NormalZ=1 AngleXU=0 Radius=16 StartAngle=0.314159 EndAngle=1.5708
    g11: ArcOfCircle CenterX=107.6 CenterY=4 CenterZ=0 NormalX=0 NormalY=0 NormalZ=1 AngleXU=0 Radius=16 StartAngle=1.5708 EndAngle=3.00366
    g12: ArcOfCircle CenterX=207.583 CenterY=4 CenterZ=0 NormalX=0 NormalY=0 NormalZ=1 AngleXU=0 Radius=17 StartAngle=1.85815 EndAngle=3.57792
    g13: ArcOfCircle CenterX=184.801 CenterY=-67.3089 CenterZ=0 NormalX=0 NormalY=0 NormalZ=1 AngleXU=0 Radius=33.7833 StartAngle=5.88425 EndAngle=6.71952
    g14: LineSegment StartX=0 StartY=39.2 StartZ=0 EndX=0 EndY=3.2 EndZ=0
    g15: LineSegment StartX=0 StartY=3.2 StartZ=0 EndX=82.8 EndY=3.2 EndZ=0
    g16: LineSegment StartX=82.8 StartY=3.2 StartZ=0 EndX=82.8 EndY=6.2 EndZ=0
    g17: LineSegment StartX=82.8 StartY=6.2 StartZ=0 EndX=91.752 EndY=6.2 EndZ=0
    g18: LineSegment StartX=107.6 StartY=20 StartZ=0 EndX=132.428 EndY=20 EndZ=0
    g19: LineSegment StartX=147.645 StartY=8.94427 StartZ=0 EndX=176.685 EndY=-80.4316 EndZ=0
    g20: LineSegment StartX=176.685 StartY=-80.4316 StartZ=0 EndX=215.932 EndY=-80.4316 EndZ=0
    g21: LineSegment StartX=215.42 StartY=-53.0314 StartZ=0 EndX=192.176 EndY=-3.18451 EndZ=0
    g22: LineSegment StartX=202.765 StartY=20.303 StartZ=0 EndX=195.887 EndY=39.2 EndZ=0
    g23: LineSegment StartX=195.887 StartY=39.2 StartZ=0 EndX=0 EndY=39.2 EndZ=0
    g24: LineSegment StartX=196.467 StartY=26.4942 StartZ=0 EndX=194.073 EndY=33.0721 EndZ=0
    g25: LineSegment StartX=194.073 StartY=33.0721 StartZ=0 EndX=189.939 EndY=31.5672 EndZ=0
    g26: LineSegment StartX=189.939 StartY=31.5672 StartZ=0 EndX=192.333 EndY=24.9893 EndZ=0
    g27: LineSegment StartX=192.333 StartY=24.9893 StartZ=0 EndX=196.467 EndY=26.4942 EndZ=0
    g28: LineSegment StartX=132.428 StartY=20 StartZ=0 EndX=144.053 EndY=20 EndZ=0
    g29: LineSegment StartX=144.053 StartY=20 StartZ=0 EndX=147.645 EndY=8.94427 EndZ=0
  constraints (65):
    c: Equal(g0,g-25)
    c: Equal(g2,g-29)
    c: Equal(g3,g-30)
    c: Equal(g4,g-28)
    c: Equal(g1,g-26)
    c: Coincident(g0,g-25)
    c: Coincident(g1,g-26)
    c: Coincident(g2,g-29)
    c: Coincident(g3,g-30)
    c: Coincident(g4,g-28)
    c: Equal(g5,g-23)
    c: Equal(g6,g-24)
    c: Coincident(g5,g-23)
    c: Coincident(g6,g-24)
    c: Equal(g7,g-20)
    c: Coincident(g7,g-20)
    c: Equal(g9,g-22)
    c: Coincident(g9,g-22)
    c: Equal(g8,g-21)
    c: Coincident(g8,g-21)
    c: Equal(g13,g-12)
    c: Equal(g12,g-14)
    c: Equal(g10,g-9)
    c: Equal(g11,g-7)
    c: Coincident(g14,g-27)
    c: Coincident(g14,g-27)
    c: Coincident(g15,g14)
    c: Coincident(g15,g-5)
    c: Coincident(g16,g15)
    c: Coincident(g16,g-6)
    c: Coincident(g17,g16)
    c: Coincident(g17,g-7)
    c: Coincident(g11,g17)
    c: Coincident(g11,g-8)
    c: Coincident(g18,g11)
    c: Coincident(g18,g-9)
    c: Coincident(g10,g18)
    c: Coincident(g10,g-10)
    c: Coincident(g19,g10)
    c: Coincident(g19,g-11)
    c: Coincident(g20,g19)
    c: Coincident(g20,g-12)
    c: Coincident(g13,g20)
    c: Coincident(g13,g-13)
    c: Coincident(g21,g13)
    c: Coincident(g21,g-14)
    c: Coincident(g12,g21)
    c: Coincident(g12,g-15)
    c: Coincident(g22,g12)
    c: Coincident(g22,g-15)
    c: Coincident(g23,g22)
    c: Coincident(g23,g14)
    c: Coincident(g24,g-18)
    c: Coincident(g24,g-16)
    c: Coincident(g25,g24)
    c: Coincident(g25,g-19)
    c: Coincident(g26,g25)
    c: Coincident(g26,g-19)
    c: Coincident(g27,g26)
    c: Coincident(g27,g24)
    c: Coincident(g29,g10)
    c: Coincident(g28,g10)
    c: Coincident(g29,g28)
    c: Parallel(g28,g18)
    c: Parallel(g29,g19)
FEATURE [PartDesign::Pad] Pad011
  Direction = (0,1,-2e-16)
  Length = 2
  Length2 = 10
  Profile = -> Sketch114
  ReferenceAxis = -> Sketch114 [N_Axis]
  Refine = true
  Reversed = true
  Suppressed = false
  Type = 0
FEATURE [Sketcher::SketchObject] Sketch115
  ArcFitTolerance = 1e-06
  AttachmentSupport = -> [Pad011]
  ExternalGeometry = -> [Binder001]
  FullyConstrained = true
  MakeInternals = false
  MapMode = 5
  Placement = pos=(0,1.7e-15,0) rot=(0,0.707107,0.707107;3.14159rad)
  sketch-geometry (4):
    g0: ArcOfCircle CenterX=24.2 CenterY=26.7 CenterZ=0 NormalX=0 NormalY=0 NormalZ=1 AngleXU=0 Radius=3 StartAngle=4.48384e-08 EndAngle=3.14159
    g1: ArcOfCircle CenterX=24.2 CenterY=15.7 CenterZ=0 NormalX=0 NormalY=0 NormalZ=1 AngleXU=0 Radius=3 StartAngle=3.14159 EndAngle=6.28318
    g2: LineSegment StartX=21.2 StartY=26.7 StartZ=0 EndX=21.2 EndY=15.7 EndZ=0
    g3: LineSegment StartX=27.2 StartY=26.7 StartZ=0 EndX=27.2 EndY=15.7 EndZ=0
  constraints (12):
    c: Equal(g1,g-4)
    c: Equal(g0,g-3)
    c: Coincident(g0,g-3)
    c: Coincident(g1,g-4)
    c: Vertical(g2)
    c: Vertical(g3)
    c: Tangent(g3,g-3)
    c: Tangent(g2,g-3)
    c: Coincident(g0,g2)
    c: Coincident(g0,g3)
    c: Coincident(g1,g2)
    c: Coincident(g3,g1)
FEATURE [Sketcher::SketchObject] Sketch117  label="Sketch117 - fori per inserto M3 x 3 x 4.5"
  ArcFitTolerance = 1e-06
  AttachmentSupport = -> [Pad011]
  ExternalGeometry = -> [Binder001]
  FullyConstrained = true
  MakeInternals = false
  MapMode = 5
  Placement = pos=(0,1.7e-15,0) rot=(0,0.707107,0.707107;3.14159rad)
  sketch-geometry (4):
    g0: Circle CenterX=43.2 CenterY=30.3 CenterZ=0 NormalX=0 NormalY=0 NormalZ=1 AngleXU=0 Radius=2.25
    g1: Circle CenterX=43.2 CenterY=12.1 CenterZ=0 NormalX=0 NormalY=0 NormalZ=1 AngleXU=0 Radius=2.25
    g2: Circle CenterX=18.6 CenterY=30.3 CenterZ=0 NormalX=0 NormalY=0 NormalZ=1 AngleXU=0 Radius=2.25
    g3: Circle CenterX=18.6 CenterY=12.1 CenterZ=0 NormalX=0 NormalY=0 NormalZ=1 AngleXU=0 Radius=2.25
  constraints (8):
    c: Diameter(g0) = 4.5
    c: Diameter(g1) = 4.5
    c: Diameter(g2) = 4.5
    c: Diameter(g3) = 4.5
    c: Coincident(g2,g-3)
    c: Coincident(g3,g-6)
    c: Coincident(g0,g-4)
    c: Coincident(g1,g-5)
FEATURE [Sketcher::SketchObject] Sketch118
  ArcFitTolerance = 1e-06
  AttachmentSupport = -> [Pad011]
  ExternalGeometry = -> [Binder001]
  FullyConstrained = true
  MakeInternals = false
  MapMode = 5
  Placement = pos=(0,-2,0) rot=(1,0,0;1.5708rad)
  sketch-geometry (12):
    g0: Circle CenterX=-78.51 CenterY=34.8 CenterZ=0 NormalX=0 NormalY=0 NormalZ=1 AngleXU=0 Radius=1.8
    g1: Circle CenterX=-78.51 CenterY=7.6 CenterZ=0 NormalX=0 NormalY=0 NormalZ=1 AngleXU=0 Radius=1.8
    g2: Circle CenterX=-5.6 CenterY=34.8 CenterZ=0 NormalX=0 NormalY=0 NormalZ=1 AngleXU=0 Radius=1.8
    g3: Circle CenterX=-5.6 CenterY=7.6 CenterZ=0 NormalX=0 NormalY=0 NormalZ=1 AngleXU=0 Radius=1.8
    g4: LineSegment StartX=0 StartY=39.2 StartZ=0 EndX=0 EndY=3.2 EndZ=0
    g5: LineSegment StartX=0 StartY=3.2 StartZ=0 EndX=-82.8 EndY=3.2 EndZ=0
    g6: LineSegment StartX=-82.8 StartY=3.2 StartZ=0 EndX=-82.8 EndY=39.2 EndZ=0
    g7: LineSegment StartX=-82.8 StartY=39.2 StartZ=0 EndX=0 EndY=39.2 EndZ=0
    g8: ArcOfCircle CenterX=-65 CenterY=21.2 CenterZ=0 NormalX=0 NormalY=0 NormalZ=1 AngleXU=0 Radius=10 StartAngle=1.5708 EndAngle=4.71239
    g9: ArcOfCircle CenterX=-19 CenterY=21.2 CenterZ=0 NormalX=0 NormalY=0 NormalZ=1 AngleXU=0 Radius=10 StartAngle=4.71239 EndAngle=7.85398
    g10: LineSegment StartX=-65 StartY=31.2 StartZ=0 EndX=-19 EndY=31.2 EndZ=0
    g11: LineSegment StartX=-65 StartY=11.2 StartZ=0 EndX=-19 EndY=11.2 EndZ=0
  constraints (25):
    c: Equal(g2,g-5)
    c: Equal(g3,g-7)
    c: Equal(g1,g-6)
    c: Equal(g0,g-4)
    c: Coincident(g0,g-4)
    c: Coincident(g1,g-6)
    c: Coincident(g3,g-7)
    c: Coincident(g2,g-5)
    c: Coincident(g4,g-8)
    c: Coincident(g4,g-9)
    c: Coincident(g5,g4)
    c: Coincident(g5,g-10)
    c: Coincident(g6,g5)
    c: PointOnObject(g6,g-3)
    c: Vertical(g6)
    c: Coincident(g7,g6)
    c: Coincident(g7,g4)
    c: Tangent(g8,g10) = 1.5708
    c: Tangent(g8,g11) = -1.5708
    c: Tangent(g9,g10) = 1.5708
    c: Tangent(g9,g11) = -1.5708
    c: Equal(g8,g9)
    c: Radius(g8) = 10
    c: Coincident(g8,g-11)
    c: Coincident(g9,g-12)
FEATURE [Sketcher::SketchObject] Sketch120
  ArcFitTolerance = 1e-06
  AttachmentSupport = -> [Pad011]
  ExternalGeometry = -> [Binder001]
  FullyConstrained = true
  MakeInternals = false
  MapMode = 5
  Placement = pos=(0,-2,0) rot=(1,0,0;1.5708rad)
  sketch-geometry (4):
    g0: LineSegment StartX=-137.815 StartY=39.2 StartZ=0 EndX=-142.655 EndY=24.303 EndZ=0
    g1: LineSegment StartX=-137.815 StartY=39.2 StartZ=0 EndX=-110.815 EndY=39.2 EndZ=0
    g2: LineSegment StartX=-142.655 StartY=24.303 StartZ=0 EndX=-110.815 EndY=24.303 EndZ=0
    g3: ArcOfCircle CenterX=-92.2534 CenterY=31.7515 CenterZ=0 NormalX=0 NormalY=0 NormalZ=1 AngleXU=0 Radius=20 StartAngle=2.75997 EndAngle=3.52321
  constraints (12):
    c: PointOnObject(g0,g-3)
    c: Coincident(g1,g0)
    c: PointOnObject(g1,g-3)
    c: Coincident(g2,g0)
    c: Horizontal(g2)
    c: Tangent(g0,g-4)
    c: Vertical(g2,g1)
    c: DistanceX(g1,g1) = 27
    c: DistanceY(g-6,g0) = 4
    c: Radius(g3) = 20
    c: Coincident(g3,g1)
    c: Coincident(g3,g2)
FEATURE [Sketcher::SketchObject] Sketch121
  ArcFitTolerance = 1e-06
  AttachmentSupport = -> [Pad011]
  ExternalGeometry = -> [Binder001]
  FullyConstrained = true
  MakeInternals = false
  MapMode = 5
  Placement = pos=(0,-2,0) rot=(1,0,0;1.5708rad)
  sketch-geometry (15):
    g0: LineSegment StartX=-137.815 StartY=39.2 StartZ=0 EndX=-143.955 EndY=20.303 EndZ=0
    g1: LineSegment StartX=-143.955 StartY=20.303 StartZ=0 EndX=-190.141 EndY=20.303 EndZ=0
    g2: LineSegment StartX=-190.141 StartY=20.303 StartZ=0 EndX=-186.139 EndY=31.3 EndZ=0
    g3: LineSegment StartX=-178.754 StartY=39.2 StartZ=0 EndX=-180.791 EndY=33.6029 EndZ=0
    g4: ArcOfCircle CenterX=-184.08 CenterY=34.8 CenterZ=0 NormalX=0 NormalY=0 NormalZ=1 AngleXU=0 Radius=3.5 StartAngle=4.71239 EndAngle=5.93412
    g5: LineSegment StartX=-184.08 StartY=31.3 StartZ=0 EndX=-186.139 EndY=31.3 EndZ=0
    g6: LineSegment StartX=-137.815 StartY=39.2 StartZ=0 EndX=-156.815 EndY=39.2 EndZ=0
    g7: LineSegment StartX=-168.815 StartY=39.2 StartZ=0 EndX=-178.754 EndY=39.2 EndZ=0
    g8: LineSegment StartX=-157.815 StartY=39.2 StartZ=0 EndX=-167.815 EndY=39.2 EndZ=0
    g9: LineSegment StartX=-168.815 StartY=31.2 StartZ=0 EndX=-156.815 EndY=31.2 EndZ=0
    g10: LineSegment StartX=-167.436 StartY=36.2 StartZ=0 EndX=-157.436 EndY=36.2 EndZ=0
    g11: ArcOfCircle CenterX=-176.411 CenterY=35.2 CenterZ=0 NormalX=0 NormalY=0 NormalZ=1 AngleXU=0 Radius=20 StartAngle=6.08183 EndAngle=6.48454
    g12: ArcOfCircle CenterX=-188.411 CenterY=35.2 CenterZ=0 NormalX=0 NormalY=0 NormalZ=1 AngleXU=0 Radius=20 StartAngle=6.08183 EndAngle=6.48454
    g13: ArcOfCircle CenterX=-177.411 CenterY=35.2 CenterZ=0 NormalX=0 NormalY=0 NormalZ=1 AngleXU=0 Radius=20 StartAngle=0.0500209 EndAngle=0.201358
    g14: ArcOfCircle CenterX=-187.411 CenterY=35.2 CenterZ=0 NormalX=0 NormalY=0 NormalZ=1 AngleXU=0 Radius=20 StartAngle=0.0500209 EndAngle=0.201358
  constraints (46):
    c: PointOnObject(g0,g-3)
    c: Tangent(g0,g-5)
    c: Coincident(g1,g0)
    c: Horizontal(g1)
    c: Coincident(g2,g1)
    c: PointOnObject(g3,g-3)
    c: Parallel(g3,g-6)
    c: Parallel(g2,g-6)
    c: Radius(g4) = 3.5
    c: Coincident(g4,g-7)
    c: Tangent(g3,g4) = 1.5708
    c: Horizontal(g5)
    c: Tangent(g5,g4) = 1.5708
    c: DistanceX(g-8,g5) = 3.8
    c: Coincident(g2,g5)
    c: Coincident(g6,g0)
    c: PointOnObject(g6,g-3)
    c: DistanceX(g6,g6) = 19
    c: PointOnObject(g7,g-3)
    c: DistanceX(g7,g6) = 12
    c: Coincident(g7,g3)
    c: PointOnObject(g8,g-3)
    c: PointOnObject(g8,g-3)
    c: DistanceX(g8,g8) = 10
    c: DistanceX(g8,g6) = 1
    c: Horizontal(g9)
    c: Vertical(g7,g9)
    c: Vertical(g6,g9)
    c: DistanceY(g9,g7) = 8
    c: Horizontal(g10)
    c: Equal(g8,g10)
    c: DistanceY(g10,g8) = 3
    c: Radius(g11) = 20
    c: Coincident(g11,g6)
    c: Coincident(g11,g9)
    c: Radius(g12) = 20
    c: Coincident(g12,g7)
    c: Coincident(g12,g9)
    c: Equal(g13,g11)
    c: Coincident(g13,g8)
    c: Coincident(g13,g10)
    c: Horizontal(g13,g11)
    c: Equal(g14,g12)
    c: Coincident(g14,g8)
    c: Coincident(g14,g10)
    c: Horizontal(g1,g-6)
FEATURE [Sketcher::SketchObject] Sketch122
  ArcFitTolerance = 1e-06
  AttachmentSupport = -> [Pad011]
  ExternalGeometry = -> [Binder001]
  FullyConstrained = true
  MakeInternals = false
  MapMode = 5
  Placement = pos=(0,-2,0) rot=(1,0,0;1.5708rad)
  sketch-geometry (8):
    g0: LineSegment StartX=-202.765 StartY=20.303 StartZ=0 EndX=-143.955 EndY=20.303 EndZ=0
    g1: ArcOfCircle CenterX=-184.801 CenterY=-67.3089 CenterZ=0 NormalX=0 NormalY=0 NormalZ=1 AngleXU=0 Radius=33.7833 StartAngle=2.70526 EndAngle=3.54053
    g2: LineSegment StartX=-176.685 StartY=-80.4316 StartZ=0 EndX=-215.932 EndY=-80.4316 EndZ=0
    g3: LineSegment StartX=-215.42 StartY=-53.0315 StartZ=0 EndX=-192.176 EndY=-3.18454 EndZ=0
    g4: ArcOfCircle CenterX=-207.583 CenterY=4 CenterZ=0 NormalX=0 NormalY=0 NormalZ=1 AngleXU=0 Radius=17 StartAngle=5.84685 EndAngle=7.56663
    g5: Circle CenterX=-213.443 CenterY=-76.8316 CenterZ=0 NormalX=0 NormalY=0 NormalZ=1 AngleXU=0 Radius=3
    g6: Circle CenterX=-179.305 CenterY=-76.8316 CenterZ=0 NormalX=0 NormalY=0 NormalZ=1 AngleXU=0 Radius=3
    g7: LineSegment StartX=-143.955 StartY=20.303 StartZ=0 EndX=-176.685 EndY=-80.4316 EndZ=0
  constraints (18):
    c: Coincident(g0,g-6)
    c: Coincident(g1,g-7)
    c: Coincident(g1,g-8)
    c: Coincident(g2,g1)
    c: Tangent(g3,g-5)
    c: Coincident(g4,g-6)
    c: Coincident(g4,g0)
    c: Coincident(g3,g4)
    c: Coincident(g1,g3)
    c: Diameter(g5) = 6
    c: Diameter(g6) = 6
    c: Coincident(g5,g-9)
    c: Coincident(g6,g-10)
    c: Horizontal(g0)
    c: Horizontal(g2)
    c: Coincident(g7,g0)
    c: Coincident(g7,g2)
    c: Tangent(g7,g-4)
FEATURE [Sketcher::SketchObject] Sketch123
  ArcFitTolerance = 1e-06
  AttachmentSupport = -> [Pad011]
  ExternalGeometry = -> [Binder001]
  FullyConstrained = true
  MakeInternals = false
  MapMode = 5
  Placement = pos=(0,-2,0) rot=(1,0,0;1.5708rad)
  sketch-geometry (4):
    g0: LineSegment StartX=-108 StartY=36.8 StartZ=0 EndX=-90 EndY=36.8 EndZ=0
    g1: LineSegment StartX=-108 StartY=36.8 StartZ=0 EndX=-108 EndY=26.8 EndZ=0
    g2: LineSegment StartX=-108 StartY=26.8 StartZ=0 EndX=-90 EndY=26.8 EndZ=0
    g3: ArcOfCircle CenterX=-94 CenterY=31.8 CenterZ=0 NormalX=0 NormalY=0 NormalZ=1 AngleXU=0 Radius=6.40312 StartAngle=5.38713 EndAngle=7.17924
  constraints (13):
    c: Horizontal(g0)
    c: Coincident(g1,g0)
    c: Vertical(g1)
    c: Coincident(g2,g1)
    c: Horizontal(g2)
    c: DistanceX(g0,g0) = 18
    c: DistanceY(g1,g1) = 10
    c: Equal(g0,g2)
    c: DistanceX(g0,g-3) = 90
    c: DistanceY(g0,g-3) = 2.4
    c: Coincident(g3,g0)
    c: Coincident(g3,g2)
    c: DistanceX(g3,g0) = 4
FEATURE [PartDesign::Chamfer] Chamfer014
  Angle = 45
  Base = -> Pad011 [Edge80,Edge4,Edge7]
  BaseFeature = -> Pad011
  ChamferType = 0
  FlipDirection = false
  Refine = true
  Size = 1.9
  Size2 = 1
  SupportTransform = false
  Suppressed = false
  UseAllEdges = false
FEATURE [PartDesign::Pocket] Pocket006
  BaseFeature = -> Chamfer014
  Direction = (0,-1,2e-16)
  Length = 1.2
  Length2 = 5
  Profile = -> Sketch115
  ReferenceAxis = -> Sketch115 [N_Axis]
  Refine = true
  Suppressed = false
  Type = 0
FEATURE [Sketcher::SketchObject] Sketch116  label="Sketch116 - pieno per inserto M3 x 3 x 4,5"
  ArcFitTolerance = 1e-06
  AttachmentSupport = -> [Pocket006]
  ExternalGeometry = -> [Binder001]
  FullyConstrained = true
  MakeInternals = false
  MapMode = 5
  Placement = pos=(0,1.7e-15,0) rot=(0,0.707107,0.707107;3.14159rad)
  sketch-geometry (4):
    g0: Circle CenterX=43.2 CenterY=30.3 CenterZ=0 NormalX=0 NormalY=0 NormalZ=1 AngleXU=0 Radius=3.4
    g1: Circle CenterX=43.2 CenterY=12.1 CenterZ=0 NormalX=0 NormalY=0 NormalZ=1 AngleXU=0 Radius=3.4
    g2: Circle CenterX=18.6 CenterY=30.3 CenterZ=0 NormalX=0 NormalY=0 NormalZ=1 AngleXU=0 Radius=3.4
    g3: Circle CenterX=18.6 CenterY=12.1 CenterZ=0 NormalX=0 NormalY=0 NormalZ=1 AngleXU=0 Radius=3.4
  constraints (8):
    c: Diameter(g0) = 6.8
    c: Diameter(g1) = 6.8
    c: Diameter(g2) = 6.8
    c: Diameter(g3) = 6.8
    c: Coincident(g2,g-3)
    c: Coincident(g0,g-4)
    c: Coincident(g3,g-6)
    c: Coincident(g1,g-5)
FEATURE [PartDesign::Pad] Pad012
  BaseFeature = -> Pocket006
  Direction = (0,1,-2e-16)
  Length = 2.4
  Length2 = 10
  Profile = -> Sketch116
  ReferenceAxis = -> Sketch116 [N_Axis]
  Refine = true
  Suppressed = false
  Type = 0
FEATURE [PartDesign::Pocket] Pocket007
  BaseFeature = -> Pad012
  Direction = (0,-1,2e-16)
  Length = 0.6
  Length2 = 2.4
  Profile = -> Sketch117
  ReferenceAxis = -> Sketch117 [N_Axis]
  Refine = true
  Suppressed = false
  Type = 4
FEATURE [PartDesign::Pad] Pad013
  BaseFeature = -> Pocket007
  Direction = (0,-1,2e-16)
  Length = 1.6
  Length2 = 10
  Profile = -> Sketch118
  ReferenceAxis = -> Sketch118 [N_Axis]
  Refine = true
  Suppressed = false
  Type = 0
FEATURE [Sketcher::SketchObject] Sketch119
  ArcFitTolerance = 1e-06
  AttachmentSupport = -> [Pad013]
  ExternalGeometry = -> [Binder001]
  FullyConstrained = true
  MakeInternals = false
  MapMode = 5
  Placement = pos=(0,-3.6,0) rot=(1,0,0;1.5708rad)
  sketch-geometry (21):
    g0: LineSegment [constr] StartX=-82.8 StartY=3.2 StartZ=0 EndX=-82.8 EndY=39.2 EndZ=0
    g1: ArcOfCircle CenterX=-78.51 CenterY=34.8 CenterZ=0 NormalX=0 NormalY=0 NormalZ=1 AngleXU=0 Radius=3.5 StartAngle=4.71239 EndAngle=6.28319
    g2: ArcOfCircle CenterX=-78.51 CenterY=7.6 CenterZ=0 NormalX=0 NormalY=0 NormalZ=1 AngleXU=0 Radius=3.5 StartAngle=0 EndAngle=1.5708
    g3: ArcOfCircle CenterX=-5.6 CenterY=34.8 CenterZ=0 NormalX=0 NormalY=0 NormalZ=1 AngleXU=0 Radius=3.5 StartAngle=3.14159 EndAngle=4.71239
    g4: ArcOfCircle CenterX=-5.6 CenterY=7.6 CenterZ=0 NormalX=0 NormalY=0 NormalZ=1 AngleXU=0 Radius=3.5 StartAngle=1.5708 EndAngle=3.14159
    g5: LineSegment StartX=0 StartY=39.2 StartZ=0 EndX=0 EndY=31.3 EndZ=0
    g6: LineSegment StartX=0 StartY=39.2 StartZ=0 EndX=-9.1 EndY=39.2 EndZ=0
    g7: LineSegment StartX=0 StartY=3.2 StartZ=0 EndX=0 EndY=11.1 EndZ=0
    g8: LineSegment StartX=0 StartY=3.2 StartZ=0 EndX=-9.1 EndY=3.2 EndZ=0
    g9: LineSegment StartX=-82.8 StartY=3.2 StartZ=0 EndX=-75.01 EndY=3.2 EndZ=0
    g10: LineSegment StartX=-82.8 StartY=3.2 StartZ=0 EndX=-82.8 EndY=11.1 EndZ=0
    g11: LineSegment StartX=-82.8 StartY=39.2 StartZ=0 EndX=-82.8 EndY=31.3 EndZ=0
    g12: LineSegment StartX=-82.8 StartY=39.2 StartZ=0 EndX=-75.01 EndY=39.2 EndZ=0
    g13: LineSegment StartX=-82.8 StartY=31.3 StartZ=0 EndX=-78.51 EndY=31.3 EndZ=0
    g14: LineSegment StartX=-75.01 StartY=39.2 StartZ=0 EndX=-75.01 EndY=34.8 EndZ=0
    g15: LineSegment StartX=-82.8 StartY=11.1 StartZ=0 EndX=-78.51 EndY=11.1 EndZ=0
    g16: LineSegment StartX=-75.01 StartY=3.2 StartZ=0 EndX=-75.01 EndY=7.6 EndZ=0
    g17: LineSegment StartX=-9.1 StartY=39.2 StartZ=0 EndX=-9.1 EndY=34.8 EndZ=0
    g18: LineSegment StartX=0 StartY=31.3 StartZ=0 EndX=-5.6 EndY=31.3 EndZ=0
    g19: LineSegment StartX=0 StartY=11.1 StartZ=0 EndX=-5.6 EndY=11.1 EndZ=0
    g20: LineSegment StartX=-9.1 StartY=3.2 StartZ=0 EndX=-9.1 EndY=7.6 EndZ=0
  constraints (51):
    c: Coincident(g0,g-10)
    c: PointOnObject(g0,g-8)
    c: Vertical(g0)
    c: Coincident(g1,g-3)
    c: Coincident(g2,g-4)
    c: Coincident(g3,g-5)
    c: Coincident(g4,g-6)
    c: Radius(g4) = 3.5
    c: Radius(g3) = 3.5
    c: Radius(g1) = 3.5
    c: Radius(g2) = 3.5
    c: Coincident(g5,g-9)
    c: PointOnObject(g5,g-9)
    c: Coincident(g6,g5)
    c: PointOnObject(g6,g-8)
    c: Coincident(g7,g-9)
    c: PointOnObject(g7,g-9)
    c: Coincident(g8,g7)
    c: PointOnObject(g8,g-7)
    c: Coincident(g9,g0)
    c: PointOnObject(g9,g-7)
    c: Coincident(g10,g0)
    c: PointOnObject(g10,g0)
    c: Coincident(g11,g0)
    c: PointOnObject(g11,g0)
    c: Coincident(g12,g0)
    c: PointOnObject(g12,g-8)
    c: Coincident(g13,g11)
    c: Horizontal(g13)
    c: Coincident(g14,g12)
    c: Vertical(g14)
    c: Coincident(g15,g10)
    c: Horizontal(g15)
    c: Coincident(g16,g9)
    c: Vertical(g16)
    c: Coincident(g17,g6)
    c: Vertical(g17)
    c: Coincident(g18,g5)
    c: Horizontal(g18)
    c: Coincident(g19,g7)
    c: Horizontal(g19)
    c: Coincident(g20,g8)
    c: Vertical(g20)
    c: Tangent(g20,g4) = 1.5708
    c: Tangent(g4,g19) = -1.5708
    c: Tangent(g18,g3) = 1.5708
    c: Tangent(g3,g17) = -1.5708
    c: Tangent(g13,g1) = -1.5708
    c: Tangent(g1,g14) = 1.5708
    c: Tangent(g16,g2) = -1.5708
    c: Tangent(g2,g15) = 1.5708
FEATURE [PartDesign::Pocket] Pocket008
  BaseFeature = -> Pad013
  Direction = (0,1,-2e-16)
  Length = 1.6
  Length2 = 5
  Profile = -> Sketch119
  ReferenceAxis = -> Sketch119 [N_Axis]
  Refine = true
  Suppressed = false
  Type = 0
FEATURE [PartDesign::Pad] Pad017
  BaseFeature = -> Pocket008
  Direction = (0,-1,2e-16)
  Length = 1.6
  Length2 = 10
  Profile = -> Sketch123
  ReferenceAxis = -> Sketch123 [N_Axis]
  Refine = true
  Suppressed = false
  Type = 0
FEATURE [Sketcher::SketchObject] Sketch125
  ArcFitTolerance = 1e-06
  AttachmentSupport = -> [Pad017]
  ExternalGeometry = -> [Pad017]
  FullyConstrained = true
  MakeInternals = false
  MapMode = 5
  Placement = pos=(0,-3.6,8e-16) rot=(1,0,0;1.5708rad)
  sketch-geometry (20):
    g0: LineSegment StartX=-108 StartY=35.8 StartZ=0 EndX=-108 EndY=35 EndZ=0
    g1: LineSegment StartX=-108 StartY=35 StartZ=0 EndX=-97 EndY=35 EndZ=0
    g2: LineSegment StartX=-97 StartY=35 StartZ=0 EndX=-97 EndY=35.8 EndZ=0
    g3: LineSegment StartX=-97 StartY=35.8 StartZ=0 EndX=-108 EndY=35.8 EndZ=0
    g4: LineSegment StartX=-108 StartY=28.6 StartZ=0 EndX=-108 EndY=27.8 EndZ=0
    g5: LineSegment StartX=-108 StartY=27.8 StartZ=0 EndX=-97 EndY=27.8 EndZ=0
    g6: LineSegment StartX=-97 StartY=27.8 StartZ=0 EndX=-97 EndY=28.6 EndZ=0
    g7: LineSegment StartX=-97 StartY=28.6 StartZ=0 EndX=-108 EndY=28.6 EndZ=0
    g8: LineSegment StartX=-108 StartY=30.4 StartZ=0 EndX=-108 EndY=29.6 EndZ=0
    g9: LineSegment StartX=-108 StartY=29.6 StartZ=0 EndX=-97 EndY=29.6 EndZ=0
    g10: LineSegment StartX=-97 StartY=29.6 StartZ=0 EndX=-97 EndY=30.4 EndZ=0
    g11: LineSegment StartX=-97 StartY=30.4 StartZ=0 EndX=-108 EndY=30.4 EndZ=0
    g12: LineSegment StartX=-108 StartY=32.2 StartZ=0 EndX=-108 EndY=31.4 EndZ=0
    g13: LineSegment StartX=-108 StartY=31.4 StartZ=0 EndX=-97 EndY=31.4 EndZ=0
    g14: LineSegment StartX=-97 StartY=31.4 StartZ=0 EndX=-97 EndY=32.2 EndZ=0
    g15: LineSegment StartX=-97 StartY=32.2 StartZ=0 EndX=-108 EndY=32.2 EndZ=0
    g16: LineSegment StartX=-108 StartY=34 StartZ=0 EndX=-108 EndY=33.2 EndZ=0
    g17: LineSegment StartX=-108 StartY=33.2 StartZ=0 EndX=-97 EndY=33.2 EndZ=0
    g18: LineSegment StartX=-97 StartY=33.2 StartZ=0 EndX=-97 EndY=34 EndZ=0
    g19: LineSegment StartX=-97 StartY=34 StartZ=0 EndX=-108 EndY=34 EndZ=0
  constraints (55):
    c: Coincident(g1,g0)
    c: Horizontal(g1)
    c: Coincident(g2,g1)
    c: Vertical(g2)
    c: Coincident(g3,g2)
    c: Horizontal(g3)
    c: Coincident(g3,g0)
    c: DistanceX(g1,g1) = 11
    c: DistanceY(g2,g2) = 0.8
    c: Coincident(g5,g4)
    c: Horizontal(g5)
    c: Coincident(g6,g5)
    c: Vertical(g6)
    c: Coincident(g7,g6)
    c: Horizontal(g7)
    c: Coincident(g7,g4)
    c: Coincident(g9,g8)
    c: Horizontal(g9)
    c: Coincident(g10,g9)
    c: Vertical(g10)
    c: Coincident(g11,g10)
    c: Horizontal(g11)
    c: Coincident(g11,g8)
    c: Coincident(g13,g12)
    c: Horizontal(g13)
    c: Coincident(g14,g13)
    c: Vertical(g14)
    c: Coincident(g15,g14)
    c: Horizontal(g15)
    c: Coincident(g15,g12)
    c: Coincident(g17,g16)
    c: Horizontal(g17)
    c: Coincident(g18,g17)
    c: Vertical(g18)
    c: Coincident(g19,g18)
    c: Horizontal(g19)
    c: Coincident(g19,g16)
    c: Equal(g3,g19)
    c: Equal(g3,g15)
    c: Equal(g3,g11)
    c: Equal(g3,g7)
    c: Equal(g2,g18)
    c: Equal(g2,g14)
    c: Equal(g2,g10)
    c: Equal(g2,g6)
    c: DistanceY(g-4,g4) = 1
    c: DistanceY(g4,g8) = 1
    c: DistanceY(g8,g12) = 1
    c: DistanceY(g12,g16) = 1
    c: DistanceY(g16,g0) = 1
    c: Tangent(g0,g-5)
    c: Tangent(g16,g-5)
    c: Tangent(g12,g-5)
    c: Tangent(g8,g-5)
    c: Tangent(g4,g-5)
FEATURE [PartDesign::Chamfer] Chamfer009
  Angle = 45
  Base = -> Pad017 [Edge151,Edge154]
  BaseFeature = -> Pad017
  ChamferType = 1
  FlipDirection = false
  Refine = true
  Size = 1.5
  Size2 = 2.8
  SupportTransform = false
  Suppressed = false
  UseAllEdges = false
FEATURE [PartDesign::Pocket] Pocket009
  BaseFeature = -> Chamfer009
  Direction = (0,1,-2e-16)
  Length = 1
  Length2 = 5
  Profile = -> Sketch125
  ReferenceAxis = -> Sketch125 [N_Axis]
  Refine = true
  Suppressed = false
  Type = 0
FEATURE [PartDesign::Pad] Pad014
  BaseFeature = -> Pocket009
  Direction = (0,-1,2e-16)
  Length = 0.8
  Length2 = 10
  Profile = -> Sketch120
  ReferenceAxis = -> Sketch120 [N_Axis]
  Refine = true
  Suppressed = false
  Type = 0
FEATURE [Sketcher::SketchObject] Sketch124
  ArcFitTolerance = 1e-06
  AttachmentSupport = -> [Pad014]
  ExternalGeometry = -> [Binder001]
  FullyConstrained = true
  MakeInternals = false
  MapMode = 5
  Placement = pos=(0,-2.8,6e-16) rot=(1,0,0;1.5708rad)
  sketch-geometry (4):
    g0: LineSegment StartX=-129 StartY=39.2 StartZ=0 EndX=-131.599 EndY=31.2 EndZ=0
    g1: LineSegment StartX=-118 StartY=39.2 StartZ=0 EndX=-120.599 EndY=31.2 EndZ=0
    g2: LineSegment StartX=-129 StartY=39.2 StartZ=0 EndX=-118 EndY=39.2 EndZ=0
    g3: LineSegment StartX=-120.599 StartY=31.2 StartZ=0 EndX=-131.599 EndY=31.2 EndZ=0
  constraints (12):
    c: PointOnObject(g0,g-3)
    c: PointOnObject(g1,g-3)
    c: Parallel(g-4,g0)
    c: Parallel(g-4,g1)
    c: Coincident(g2,g0)
    c: Coincident(g2,g1)
    c: DistanceX(g2,g2) = 11
    c: DistanceY(g1,g1) = 8
    c: Coincident(g3,g1)
    c: Horizontal(g3)
    c: Coincident(g3,g0)
    c: DistanceX(g1,g-3) = 118
FEATURE [PartDesign::Pad] Pad018
  BaseFeature = -> Pad014
  Direction = (0,-1,2e-16)
  Length = 1.2
  Length2 = 10
  Profile = -> Sketch124
  ReferenceAxis = -> Sketch124 [N_Axis]
  Refine = true
  Suppressed = false
  Type = 0
FEATURE [Sketcher::SketchObject] Sketch126
  ArcFitTolerance = 1e-06
  AttachmentSupport = -> [Pad018]
  ExternalGeometry = -> [Pad018]
  FullyConstrained = true
  MakeInternals = false
  MapMode = 5
  Placement = pos=(0,-4,0) rot=(1,0,0;1.5708rad)
  sketch-geometry (8):
    g0: LineSegment StartX=-129.877 StartY=36.5 StartZ=0 EndX=-130.137 EndY=35.7 EndZ=0
    g1: LineSegment StartX=-130.69 StartY=34 StartZ=0 EndX=-130.95 EndY=33.2 EndZ=0
    g2: LineSegment StartX=-129.877 StartY=36.5 StartZ=0 EndX=-118.877 EndY=36.5 EndZ=0
    g3: LineSegment StartX=-130.137 StartY=35.7 StartZ=0 EndX=-119.137 EndY=35.7 EndZ=0
    g4: LineSegment StartX=-130.69 StartY=34 StartZ=0 EndX=-119.69 EndY=34 EndZ=0
    g5: LineSegment StartX=-130.95 StartY=33.2 StartZ=0 EndX=-119.95 EndY=33.2 EndZ=0
    g6: LineSegment StartX=-118.877 StartY=36.5 StartZ=0 EndX=-119.137 EndY=35.7 EndZ=0
    g7: LineSegment StartX=-119.69 StartY=34 StartZ=0 EndX=-119.95 EndY=33.2 EndZ=0
  constraints (20):
    c: Coincident(g2,g0)
    c: Horizontal(g2)
    c: Coincident(g3,g0)
    c: Horizontal(g3)
    c: Coincident(g4,g1)
    c: Horizontal(g4)
    c: Coincident(g5,g1)
    c: Horizontal(g5)
    c: Coincident(g6,g2)
    c: Coincident(g6,g3)
    c: Coincident(g7,g4)
    c: Coincident(g7,g5)
    c: Tangent(g0,g-4)
    c: Tangent(g6,g-5)
    c: Tangent(g1,g-4)
    c: Tangent(g7,g-5)
    c: DistanceY(g3,g2) = 0.8
    c: DistanceY(g5,g4) = 0.8
    c: DistanceY(g-6,g1) = 2
    c: DistanceY(g-6,g0) = 4.5
FEATURE [PartDesign::Chamfer] Chamfer008
  Angle = 45
  Base = -> Pad018 [Edge257]
  BaseFeature = -> Pad018
  ChamferType = 1
  FlipDirection = false
  Refine = true
  Size = 1
  Size2 = 6
  SupportTransform = false
  Suppressed = false
  UseAllEdges = false
FEATURE [PartDesign::Pocket] Pocket010
  BaseFeature = -> Chamfer008
  Direction = (0,1,-2e-16)
  Length = 1
  Length2 = 5
  Profile = -> Sketch126
  ReferenceAxis = -> Sketch126 [N_Axis]
  Refine = true
  Suppressed = false
  Type = 0
FEATURE [PartDesign::Pad] Pad015
  BaseFeature = -> Pocket010
  Direction = (0,-1,2e-16)
  Length = 2
  Length2 = 10
  Profile = -> Sketch121
  ReferenceAxis = -> Sketch121 [N_Axis]
  Refine = true
  Suppressed = false
  Type = 0
FEATURE [PartDesign::Pad] Pad016
  BaseFeature = -> Pad015
  Direction = (0,-1,2e-16)
  Length = 1.6
  Length2 = 10
  Profile = -> Sketch122
  ReferenceAxis = -> Sketch122 [N_Axis]
  Refine = true
  Suppressed = false
  Type = 0
FEATURE [Sketcher::SketchObject] Sketch127
  ArcFitTolerance = 1e-06
  AttachmentSupport = -> [Pad016]
  ExternalGeometry = -> [Pad016]
  FullyConstrained = true
  MakeInternals = false
  MapMode = 5
  Placement = pos=(0,0,-80.4316) rot=(1,0,0;3.14159rad)
  sketch-geometry (8):
    g0: LineSegment StartX=-176.685 StartY=3.6 StartZ=0 EndX=-186.685 EndY=3.6 EndZ=0
    g1: LineSegment [constr] StartX=-186.685 StartY=3.6 StartZ=0 EndX=-186.685 EndY=-9e-16 EndZ=0
    g2: LineSegment StartX=-176.685 StartY=3.6 StartZ=0 EndX=-176.685 EndY=0 EndZ=0
    g3: ArcOfEllipse CenterX=-186.685 CenterY=-9e-16 CenterZ=0 NormalX=0 NormalY=0 NormalZ=1 MajorRadius=10 MinorRadius=3.6 AngleXU=1e-16 StartAngle=0 EndAngle=1.5708
    g4: LineSegment [constr] StartX=-176.685 StartY=-2e-15 StartZ=0 EndX=-196.685 EndY=-2e-15 EndZ=0
    g5: LineSegment [constr] StartX=-186.685 StartY=3.6 StartZ=0 EndX=-186.685 EndY=-3.6 EndZ=0
    g6: GeomPoint [constr] X=-177.356 Y=0 Z=0
    g7: GeomPoint [constr] X=-196.015 Y=-1.9e-15 Z=0
  constraints (13):
    c: Coincident(g0,g-4)
    c: PointOnObject(g0,g-4)
    c: DistanceX(g0,g0) = 10
    c: Coincident(g1,g0)
    c: PointOnObject(g1,g-5)
    c: Vertical(g1)
    c: Coincident(g2,g0)
    c: Coincident(g2,g-5)
    c: InternalAlignment(g4-g7 -> g3) x4
    c: Coincident(g3,g1)
    c: Coincident(g3,g0)
    c: Coincident(g3,g2)
    c: Horizontal(g4)
FEATURE [Sketcher::SketchObject] Sketch128
  ArcFitTolerance = 1e-06
  AttachmentSupport = -> [Pad016]
  ExternalGeometry = -> [Pad016]
  FullyConstrained = true
  MakeInternals = false
  MapMode = 5
  Placement = pos=(0,0,-80.4316) rot=(1,0,0;3.14159rad)
  sketch-geometry (8):
    g0: LineSegment StartX=-215.932 StartY=3.6 StartZ=0 EndX=-215.932 EndY=-1.3e-15 EndZ=0
    g1: LineSegment StartX=-215.932 StartY=3.6 StartZ=0 EndX=-205.932 EndY=3.6 EndZ=0
    g2: LineSegment [constr] StartX=-205.932 StartY=3.6 StartZ=0 EndX=-205.932 EndY=-9e-16 EndZ=0
    g3: ArcOfEllipse CenterX=-205.932 CenterY=-9e-16 CenterZ=0 NormalX=0 NormalY=0 NormalZ=1 MajorRadius=10 MinorRadius=3.6 AngleXU=-3.14159 StartAngle=4.71239 EndAngle=6.28319
    g4: LineSegment [constr] StartX=-215.932 StartY=-1e-15 StartZ=0 EndX=-195.932 EndY=-1e-15 EndZ=0
    g5: LineSegment [constr] StartX=-205.932 StartY=-3.6 StartZ=0 EndX=-205.932 EndY=3.6 EndZ=0
    g6: GeomPoint [constr] X=-215.262 Y=-2e-15 Z=0
    g7: GeomPoint [constr] X=-196.602 Y=-1e-15 Z=0
  constraints (13):
    c: Coincident(g0,g-4)
    c: Coincident(g0,g-5)
    c: Coincident(g1,g0)
    c: PointOnObject(g1,g-3)
    c: DistanceX(g1,g1) = 10
    c: Coincident(g2,g1)
    c: Vertical(g2)
    c: PointOnObject(g2,g-5)
    c: InternalAlignment(g4-g7 -> g3) x4
    c: Coincident(g3,g2)
    c: Coincident(g3,g1)
    c: Coincident(g3,g0)
    c: Horizontal(g4)
FEATURE [PartDesign::SubtractivePipe] SubtractivePipe002
  AuxilleryCurvelinear = true
  AuxillerySpineTangent = false
  BaseFeature = -> Pad016
  Binormal = (0,0,0)
  Mode = 0
  Profile = -> Sketch127
  Refine = true
  Spine = -> Pad016 [Edge254]
  SpineTangent = false
  Suppressed = false
  Transformation = 0
  Transition = 0
FEATURE [PartDesign::SubtractivePipe] SubtractivePipe003
  AuxilleryCurvelinear = true
  AuxillerySpineTangent = false
  BaseFeature = -> SubtractivePipe002
  Binormal = (0,0,0)
  Mode = 0
  Profile = -> Sketch128
  Refine = true
  Spine = -> Pad016 [Edge256,Edge251,Edge252]
  SpineTangent = false
  Suppressed = false
  Transformation = 0
  Transition = 0
FEATURE [Sketcher::SketchObject] Sketch129
  ArcFitTolerance = 1e-06
  AttachmentSupport = -> [Pad016]
  ExternalGeometry = -> [Binder001]
  FullyConstrained = true
  MakeInternals = false
  MapMode = 5
  Placement = pos=(0,-3.6,0) rot=(1,0,0;1.5708rad)
  sketch-geometry (12):
    g0: LineSegment [constr] StartX=-192.176 StartY=-3.18451 StartZ=0 EndX=-181.223 EndY=20.303 EndZ=0
    g1: LineSegment [constr] StartX=-202.765 StartY=20.303 StartZ=0 EndX=-181.223 EndY=20.303 EndZ=0
    g2: LineSegment StartX=-202.765 StartY=20.303 StartZ=0 EndX=-181.223 EndY=20.303 EndZ=0
    g3: LineSegment StartX=-192.176 StartY=-3.18451 StartZ=0 EndX=-196.804 EndY=-13.1107 EndZ=0
    g4: ArcOfCircle CenterX=-207.583 CenterY=4 CenterZ=0 NormalX=0 NormalY=0 NormalZ=1 AngleXU=0 Radius=17 StartAngle=5.84685 EndAngle=7.56663
    g5: ArcOfEllipse CenterX=-181.223 CenterY=8.55923 CenterZ=0 NormalX=0 NormalY=0 NormalZ=1 MajorRadius=23.4779 MinorRadius=11.7437 AngleXU=2e-16 StartAngle=4.71239 EndAngle=7.85398
    g6: LineSegment [constr] StartX=-157.745 StartY=8.55923 StartZ=0 EndX=-204.701 EndY=8.55923 EndZ=0
    g7: LineSegment [constr] StartX=-181.223 StartY=20.303 StartZ=0 EndX=-181.223 EndY=-3.18451 EndZ=0
    g8: GeomPoint [constr] X=-160.894 Y=8.55923 Z=0
    g9: GeomPoint [constr] X=-201.553 Y=8.55923 Z=0
    g10: ArcOfCircle CenterX=-181.223 CenterY=-20.3763 CenterZ=0 NormalX=0 NormalY=0 NormalZ=1 AngleXU=0 Radius=17.1918 StartAngle=1.57079 EndAngle=2.70526
    g11: GeomPoint [constr] X=-181.223 Y=-3.18451 Z=0
  constraints (23):
    c: Coincident(g0,g-5)
    c: Coincident(g1,g-6)
    c: Horizontal(g1)
    c: Coincident(g1,g0)
    c: Parallel(g0,g-4)
    c: Coincident(g2,g1)
    c: Coincident(g2,g0)
    c: Coincident(g3,g0)
    c: Equal(g4,g-5)
    c: Coincident(g4,g1)
    c: Coincident(g4,g0)
    c: InternalAlignment(g6-g9 -> g5) x4
    c: Vertical(g5,g0)
    c: Horizontal(g6)
    c: Coincident(g5,g0)
    c: DistanceX(g6,g-3) = 10.1
    c: Tangent(g10,g3) = -1.5708
    c: PointOnObject(g11,g10)
    c: Tangent(g5,g10,g11) = 1.5708
    c: Coincident(g10,g5)
    c: Coincident(g11,g7)
    c: Parallel(g3,g-4)
    c: Horizontal(g5,g0)
FEATURE [Sketcher::SketchObject] Sketch130
  ArcFitTolerance = 1e-06
  AttachmentOffset = pos=(0,0,-1.6) rot=(0,0,1;0rad)
  AttachmentSupport = -> [Pad016]
  ExternalGeometry = -> [Binder001]
  FullyConstrained = true
  MakeInternals = false
  MapMode = 5
  Placement = pos=(0,-2,-4e-16) rot=(1,0,0;1.5708rad)
  sketch-geometry (12):
    g0: LineSegment [constr] StartX=-192.176 StartY=-3.18451 StartZ=0 EndX=-181.223 EndY=20.303 EndZ=0
    g1: LineSegment [constr] StartX=-202.765 StartY=20.303 StartZ=0 EndX=-181.223 EndY=20.303 EndZ=0
    g2: LineSegment StartX=-202.765 StartY=20.303 StartZ=0 EndX=-181.223 EndY=20.303 EndZ=0
    g3: LineSegment StartX=-192.176 StartY=-3.18451 StartZ=0 EndX=-193.827 EndY=-6.72678 EndZ=0
    g4: ArcOfCircle CenterX=-207.583 CenterY=4 CenterZ=0 NormalX=0 NormalY=0 NormalZ=1 AngleXU=0 Radius=17 StartAngle=5.84685 EndAngle=7.56663
    g5: ArcOfEllipse CenterX=-181.223 CenterY=10.803 CenterZ=0 NormalX=0 NormalY=0 NormalZ=1 MajorRadius=14.4779 MinorRadius=9.5 AngleXU=0 StartAngle=4.71239 EndAngle=7.85398
    g6: LineSegment [constr] StartX=-166.745 StartY=10.803 StartZ=0 EndX=-195.701 EndY=10.803 EndZ=0
    g7: LineSegment [constr] StartX=-181.223 StartY=20.303 StartZ=0 EndX=-181.223 EndY=1.30297 EndZ=0
    g8: GeomPoint [constr] X=-170.298 Y=10.803 Z=0
    g9: GeomPoint [constr] X=-192.148 Y=10.803 Z=0
    g10: ArcOfCircle CenterX=-181.223 CenterY=-12.6042 CenterZ=0 NormalX=0 NormalY=0 NormalZ=1 AngleXU=0 Radius=13.9072 StartAngle=1.5708 EndAngle=2.70526
    g11: GeomPoint [constr] X=-181.223 Y=1.30297 Z=0
  constraints (23):
    c: Coincident(g0,g-5)
    c: Coincident(g1,g-6)
    c: Horizontal(g1)
    c: Coincident(g1,g0)
    c: Parallel(g0,g-4)
    c: Coincident(g2,g1)
    c: Coincident(g2,g0)
    c: Coincident(g3,g0)
    c: Equal(g4,g-5)
    c: Coincident(g4,g1)
    c: Coincident(g4,g0)
    c: InternalAlignment(g6-g9 -> g5) x4
    c: Vertical(g5,g0)
    c: Horizontal(g6)
    c: Coincident(g5,g0)
    c: DistanceX(g6,g-3) = 19.1
    c: Tangent(g10,g3) = -1.5708
    c: PointOnObject(g11,g10)
    c: Tangent(g5,g10,g11) = 1.5708
    c: Coincident(g10,g5)
    c: Coincident(g11,g7)
    c: Parallel(g3,g-4)
    c: DistanceY(g5,g0) = 19
FEATURE [Part::Part2DObjectPython] Clone2D001  label="Sketch130 (2D)"  # Draft 2D object (typed FeaturePython)
  Fuse = false
  Objects = -> [Sketch130]
  Placement = pos=(0,-2,-4e-16) rot=(1,0,0;1.5708rad)
  Scale = (1,1,1)
FEATURE [Sketcher::SketchObject] Sketch131
  ArcFitTolerance = 1e-06
  AttachmentOffset = pos=(0,0,-3.5) rot=(0,0,1;0rad)
  AttachmentSupport = -> [Pad016]
  ExternalGeometry = -> [Binder001]
  FullyConstrained = true
  MakeInternals = false
  MapMode = 5
  Placement = pos=(0,-0.1,-8e-16) rot=(1,0,0;1.5708rad)
  sketch-geometry (1):
    g0: GeomPoint X=-197.47 Y=8.55923 Z=0
  constraints (1):
    c: Symmetric(g-6,g-4,g0)
FEATURE [PartDesign::SubtractiveLoft] SubtractiveLoft002
  BaseFeature = -> SubtractivePipe003
  Closed = false
  Profile = -> Sketch129
  Refine = true
  Ruled = false
  Sections = -> [Sketch130]
  Suppressed = false
FEATURE [PartDesign::SubtractiveLoft] SubtractiveLoft003
  BaseFeature = -> SubtractiveLoft002
  Closed = false
  Profile = -> Clone2D001
  Refine = true
  Ruled = false
  Sections = -> [Sketch131]
  Suppressed = false
FEATURE [PartDesign::Chamfer] Chamfer010
  Angle = 45
  Base = -> SubtractiveLoft003 [Edge200,Edge201,Edge203,Edge202,Edge194]
  BaseFeature = -> SubtractiveLoft003
  ChamferType = 0
  FlipDirection = false
  Refine = true
  Size = 1.5
  Size2 = 1
  SupportTransform = false
  Suppressed = false
  UseAllEdges = false
FEATURE [PartDesign::Chamfer] Chamfer011
  Angle = 45
  Base = -> Chamfer010 [Edge15]
  BaseFeature = -> Chamfer010
  ChamferType = 0
  FlipDirection = false
  Refine = true
  Size = 1.6
  Size2 = 1
  SupportTransform = false
  Suppressed = false
  UseAllEdges = false
FEATURE [PartDesign::Chamfer] Chamfer012
  Angle = 45
  Base = -> Chamfer011 [Edge10]
  BaseFeature = -> Chamfer011
  ChamferType = 0
  FlipDirection = false
  Refine = true
  Size = 3.5
  Size2 = 1
  SupportTransform = false
  Suppressed = false
  UseAllEdges = false
FEATURE [PartDesign::Chamfer] Chamfer013
  Angle = 45
  Base = -> Chamfer012 [Edge145,Edge94]
  BaseFeature = -> Chamfer012
  ChamferType = 0
  FlipDirection = false
  Refine = true
  Size = 1.9
  Size2 = 1
  SupportTransform = false
  Suppressed = false
  UseAllEdges = false
FEATURE [Sketcher::SketchObject] Sketch132
  ArcFitTolerance = 1e-06
  AttachmentSupport = -> [Pad016]
  ExternalGeometry = -> [Binder001]
  FullyConstrained = true
  MakeInternals = false
  MapMode = 5
  Placement = pos=(0,-3.6,0) rot=(1,0,0;1.5708rad)
  sketch-geometry (3):
    g0: LineSegment [constr] StartX=-215.42 StartY=-53.0314 StartZ=0 EndX=-167.782 EndY=-53.0314 EndZ=0
    g1: Circle CenterX=-191.282 CenterY=-53.0314 CenterZ=0 NormalX=0 NormalY=0 NormalZ=1 AngleXU=0 Radius=11.5
    g2: Circle CenterX=-191.282 CenterY=-53.0314 CenterZ=0 NormalX=0 NormalY=0 NormalZ=1 AngleXU=0 Radius=10.7
  constraints (8):
    c: Coincident(g0,g-3)
    c: PointOnObject(g0,g-4)
    c: Horizontal(g0)
    c: Diameter(g1) = 23
    c: PointOnObject(g1,g0)
    c: DistanceX(g1,g0) = 23.5
    c: Diameter(g2) = 21.4
    c: Coincident(g2,g1)
FEATURE [PartDesign::Fillet] Fillet007
  Base = -> Chamfer013 [Edge83]
  BaseFeature = -> Chamfer013
  Radius = 1.1
  Refine = true
  SupportTransform = false
  Suppressed = false
  UseAllEdges = false
FEATURE [PartDesign::Fillet] Fillet008
  Base = -> Fillet007 [Edge76]
  BaseFeature = -> Fillet007
  Radius = 1.9
  Refine = true
  SupportTransform = false
  Suppressed = false
  UseAllEdges = false
FEATURE [PartDesign::Pocket] Pocket011
  BaseFeature = -> Fillet008
  Direction = (0,1,-2e-16)
  Length = 0.8
  Length2 = 5
  Profile = -> Sketch132
  ReferenceAxis = -> Sketch132 [N_Axis]
  Refine = true
  Suppressed = false
  Type = 0
FEATURE [Part::Part2DObjectPython] ShapeString  # Draft 2D object (typed FeaturePython)
  FontFile = <path>
  Fuse = false
  Justification = 6
  JustificationReference = 0
  KeepLeftMargin = false
  MakeFace = true
  ObliqueAngle = 0
  Placement = pos=(-199,-3.6,-57.5) rot=(1,0,0;1.5708rad)
  ScaleToSize = true
  Size = 10
  String = AS
  Tracking = 0
FEATURE [PartDesign::Pocket] Pocket012
  BaseFeature = -> Pocket011
  Direction = (0,1,0)
  Length = 1
  Length2 = 5
  Profile = -> ShapeString
  ReferenceAxis = -> ShapeString [N_Axis]
  Refine = true
  Suppressed = false
  Type = 0
FEATURE [PartDesign::Body] Body007  label="lato DX"
  AllowCompound = false
  Group = -> [Binder001,Sketch114,Pad011,Chamfer014,Sketch115,Pocket006,Sketch116,Pad012,Sketch117,Pocket007,Sketch118,Pad013,Sketch119,Pocket008,Pad017,Chamfer009,Pocket009,Sketch123,Sketch120,Pad014,Pad018,Chamfer008,Pocket010,Sketch121,Pad015,Sketch122,Pad016,Sketch124,Sketch125,Sketch126,Sketch127,Sketch128,SubtractivePipe002,SubtractivePipe003,Sketch129,Sketch130,Clone2D001,Sketch131,SubtractiveLoft002,+11 more]
  Origin = -> Origin007
  Tip = -> Pocket012
FEATURE [Sketcher::SketchObject] Sketch133
  ArcFitTolerance = 1e-06
  AttachmentSupport = -> [Binder]
  ExternalGeometry = -> [Binder]
  FullyConstrained = true
  MakeInternals = false
  MapMode = 5
  Placement = pos=(0,9e-16,0) rot=(0,0.707107,0.707107;3.14159rad)
  sketch-geometry (30):
    g0: LineSegment StartX=0 StartY=39.2 StartZ=0 EndX=0 EndY=3.2 EndZ=0
    g1: LineSegment StartX=0 StartY=3.2 StartZ=0 EndX=82.8 EndY=3.2 EndZ=0
    g2: LineSegment StartX=82.8 StartY=3.2 StartZ=0 EndX=82.8 EndY=6.2 EndZ=0
    g3: LineSegment StartX=82.8 StartY=6.2 StartZ=0 EndX=91.752 EndY=6.2 EndZ=0
    g4: LineSegment StartX=0 StartY=39.2 StartZ=0 EndX=195.887 EndY=39.2 EndZ=0
    g5: LineSegment StartX=195.887 StartY=39.2 StartZ=0 EndX=202.765 EndY=20.303 EndZ=0
    g6: LineSegment StartX=192.333 StartY=24.9893 StartZ=0 EndX=196.467 EndY=26.4942 EndZ=0
    g7: LineSegment StartX=196.467 StartY=26.4942 StartZ=0 EndX=194.073 EndY=33.0721 EndZ=0
    g8: LineSegment StartX=194.073 StartY=33.0721 StartZ=0 EndX=189.939 EndY=31.5672 EndZ=0
    g9: LineSegment StartX=189.939 StartY=31.5672 StartZ=0 EndX=192.333 EndY=24.9893 EndZ=0
    g10: ArcOfCircle CenterX=107.6 CenterY=4 CenterZ=0 NormalX=0 NormalY=0 NormalZ=1 AngleXU=0 Radius=16 StartAngle=1.5708 EndAngle=3.00366
    g11: LineSegment StartX=107.6 StartY=20 StartZ=0 EndX=132.428 EndY=20 EndZ=0
    g12: ArcOfCircle [constr] CenterX=132.428 CenterY=4 CenterZ=0 NormalX=0 NormalY=0 NormalZ=1 AngleXU=0 Radius=16 StartAngle=0.314159 EndAngle=1.5708
    g13: LineSegment StartX=147.645 StartY=8.94427 StartZ=0 EndX=176.685 EndY=-80.4316 EndZ=0
    g14: LineSegment StartX=176.685 StartY=-80.4316 StartZ=0 EndX=215.932 EndY=-80.4316 EndZ=0
    g15: ArcOfCircle CenterX=207.583 CenterY=4 CenterZ=0 NormalX=0 NormalY=0 NormalZ=1 AngleXU=0 Radius=17 StartAngle=1.85815 EndAngle=3.57792
    g16: ArcOfCircle CenterX=184.801 CenterY=-67.3089 CenterZ=0 NormalX=0 NormalY=0 NormalZ=1 AngleXU=0 Radius=33.7833 StartAngle=5.88425 EndAngle=6.71952
    g17: LineSegment StartX=192.176 StartY=-3.18451 StartZ=0 EndX=215.42 EndY=-53.0314 EndZ=0
    g18: Circle CenterX=5.6 CenterY=34.8 CenterZ=0 NormalX=0 NormalY=0 NormalZ=1 AngleXU=0 Radius=1.8
    g19: Circle CenterX=5.6 CenterY=7.6 CenterZ=0 NormalX=0 NormalY=0 NormalZ=1 AngleXU=0 Radius=1.8
    g20: Circle CenterX=78.51 CenterY=34.8 CenterZ=0 NormalX=0 NormalY=0 NormalZ=1 AngleXU=0 Radius=1.8
    g21: Circle CenterX=78.51 CenterY=7.6 CenterZ=0 NormalX=0 NormalY=0 NormalZ=1 AngleXU=0 Radius=1.8
    g22: Circle CenterX=184.08 CenterY=34.8 CenterZ=0 NormalX=0 NormalY=0 NormalZ=1 AngleXU=0 Radius=1.8
    g23: Circle CenterX=179.305 CenterY=-76.8316 CenterZ=0 NormalX=0 NormalY=0 NormalZ=1 AngleXU=0 Radius=1.8
    g24: Circle CenterX=213.443 CenterY=-76.8316 CenterZ=0 NormalX=0 NormalY=0 NormalZ=1 AngleXU=0 Radius=1.8
    g25: Circle CenterX=19 CenterY=21.2 CenterZ=0 NormalX=0 NormalY=0 NormalZ=1 AngleXU=0 Radius=6.3
    g26: Circle CenterX=42 CenterY=21.2 CenterZ=0 NormalX=0 NormalY=0 NormalZ=1 AngleXU=0 Radius=6.3
    g27: Circle CenterX=65 CenterY=21.2 CenterZ=0 NormalX=0 NormalY=0 NormalZ=1 AngleXU=0 Radius=6.3
    g28: LineSegment StartX=132.428 StartY=20 StartZ=0 EndX=144.053 EndY=20 EndZ=0
    g29: LineSegment StartX=147.645 StartY=8.94427 StartZ=0 EndX=144.053 EndY=20 EndZ=0
  constraints (65):
    c: Coincident(g0,g-4)
    c: Coincident(g0,g-5)
    c: Coincident(g1,g0)
    c: Coincident(g1,g-6)
    c: Coincident(g2,g1)
    c: Coincident(g2,g-7)
    c: Coincident(g3,g2)
    c: Coincident(g3,g-8)
    c: Coincident(g4,g0)
    c: Coincident(g4,g-16)
    c: Coincident(g5,g4)
    c: Coincident(g5,g-16)
    c: Coincident(g6,g-20)
    c: Coincident(g6,g-21)
    c: Coincident(g7,g6)
    c: Coincident(g7,g-23)
    c: Coincident(g8,g7)
    c: Coincident(g8,g-22)
    c: Coincident(g9,g8)
    c: Coincident(g9,g6)
    c: Equal(g10,g-8)
    c: Coincident(g10,g3)
    c: Coincident(g10,g-9)
    c: Coincident(g11,g10)
    c: Coincident(g11,g-10)
    c: Equal(g12,g-10)
    c: Coincident(g12,g11)
    c: Coincident(g12,g-11)
    c: Coincident(g13,g12)
    c: Coincident(g13,g-12)
    c: Coincident(g14,g13)
    c: Coincident(g14,g-13)
    c: Equal(g15,g-15)
    c: Coincident(g15,g5)
    c: Coincident(g15,g-15)
    c: Equal(g16,g-13)
    c: Coincident(g16,g14)
    c: Coincident(g16,g-14)
    c: Coincident(g17,g15)
    c: Coincident(g17,g16)
    c: Equal(g18,g-28)
    c: Equal(g19,g-29)
    c: Equal(g20,g-26)
    c: Equal(g21,g-27)
    c: Equal(g22,g-17)
    c: Equal(g24,g-25)
    c: Equal(g23,g-24)
    c: Coincident(g23,g-24)
    c: Coincident(g24,g-25)
    c: Coincident(g22,g-17)
    c: Coincident(g20,g-26)
    c: Coincident(g21,g-27)
    c: Coincident(g18,g-28)
    c: Coincident(g19,g-29)
    c: Equal(g25,g-30)
    c: Equal(g26,g-31)
    c: Equal(g27,g-32)
    c: Coincident(g25,g-30)
    c: Coincident(g26,g-31)
    c: Coincident(g27,g-32)
    c: Parallel(g28,g11)
    c: Parallel(g29,g13)
    c: Coincident(g28,g11)
    c: Coincident(g29,g12)
    c: Coincident(g29,g28)
FEATURE [PartDesign::Pad] Pad019
  Direction = (0,1,-2e-16)
  Length = 2
  Length2 = 10
  Profile = -> Sketch133
  ReferenceAxis = -> Sketch133 [N_Axis]
  Refine = true
  Suppressed = false
  Type = 0
FEATURE [Sketcher::SketchObject] Sketch091  label="Sketch091 - forma anteriore"
  ArcFitTolerance = 1e-06
  AttachmentSupport = -> [Pad019]
  ExternalGeometry = -> [Binder]
  FullyConstrained = true
  MakeInternals = false
  MapMode = 5
  Placement = pos=(0,2,0) rot=(0,0.707107,0.707107;3.14159rad)
  sketch-geometry (12):
    g0: Circle CenterX=5.6 CenterY=34.8 CenterZ=0 NormalX=0 NormalY=0 NormalZ=1 AngleXU=0 Radius=1.8
    g1: Circle CenterX=5.6 CenterY=7.6 CenterZ=0 NormalX=0 NormalY=0 NormalZ=1 AngleXU=0 Radius=1.8
    g2: Circle CenterX=78.51 CenterY=34.8 CenterZ=0 NormalX=0 NormalY=0 NormalZ=1 AngleXU=0 Radius=1.8
    g3: Circle CenterX=78.51 CenterY=7.6 CenterZ=0 NormalX=0 NormalY=0 NormalZ=1 AngleXU=0 Radius=1.8
    g4: LineSegment StartX=0 StartY=39.2 StartZ=0 EndX=0 EndY=3.2 EndZ=0
    g5: LineSegment StartX=0 StartY=3.2 StartZ=0 EndX=82.8 EndY=3.2 EndZ=0
    g6: LineSegment StartX=82.8 StartY=3.2 StartZ=0 EndX=82.8 EndY=39.2 EndZ=0
    g7: LineSegment StartX=82.8 StartY=39.2 StartZ=0 EndX=0 EndY=39.2 EndZ=0
    g8: ArcOfCircle CenterX=19 CenterY=21.2 CenterZ=0 NormalX=0 NormalY=0 NormalZ=1 AngleXU=0 Radius=10 StartAngle=1.5708 EndAngle=4.71239
    g9: ArcOfCircle CenterX=65 CenterY=21.2 CenterZ=0 NormalX=0 NormalY=0 NormalZ=1 AngleXU=0 Radius=10 StartAngle=4.71239 EndAngle=7.85398
    g10: LineSegment StartX=19 StartY=31.2 StartZ=0 EndX=65 EndY=31.2 EndZ=0
    g11: LineSegment StartX=19 StartY=11.2 StartZ=0 EndX=65 EndY=11.2 EndZ=0
  constraints (25):
    c: Equal(g2,g-7)
    c: Equal(g3,g-8)
    c: Equal(g1,g-13)
    c: Equal(g0,g-12)
    c: Coincident(g0,g-12)
    c: Coincident(g1,g-13)
    c: Coincident(g3,g-8)
    c: Coincident(g2,g-7)
    c: Coincident(g4,g-4)
    c: Coincident(g4,g-5)
    c: Coincident(g5,g4)
    c: Coincident(g5,g-6)
    c: Coincident(g6,g5)
    c: PointOnObject(g6,g-3)
    c: Vertical(g6)
    c: Coincident(g7,g6)
    c: Coincident(g7,g4)
    c: Tangent(g8,g10) = 1.5708
    c: Tangent(g8,g11) = -1.5708
    c: Tangent(g9,g10) = 1.5708
    c: Tangent(g9,g11) = -1.5708
    c: Equal(g8,g9)
    c: Radius(g8) = 10
    c: Coincident(g8,g-11)
    c: Coincident(g9,g-9)
FEATURE [Sketcher::SketchObject] Sketch093  label="Sketch093 - scavi interni pulsanti"
  ArcFitTolerance = 1e-06
  AttachmentSupport = -> [Pad019]
  ExternalGeometry = -> [Binder]
  FullyConstrained = true
  MakeInternals = false
  MapMode = 5
  Placement = pos=(0,1.8e-15,0) rot=(1,0,0;1.5708rad)
  sketch-geometry (3):
    g0: Circle CenterX=-65 CenterY=21.2 CenterZ=0 NormalX=0 NormalY=0 NormalZ=1 AngleXU=0 Radius=7.3
    g1: Circle CenterX=-42 CenterY=21.2 CenterZ=0 NormalX=0 NormalY=0 NormalZ=1 AngleXU=0 Radius=7.3
    g2: Circle CenterX=-19 CenterY=21.2 CenterZ=0 NormalX=0 NormalY=0 NormalZ=1 AngleXU=0 Radius=7.3
  constraints (6):
    c: Coincident(g0,g-3)
    c: Coincident(g1,g-4)
    c: Coincident(g2,g-5)
    c: Diameter(g0) = 14.6
    c: Diameter(g1) = 14.6
    c: Diameter(g2) = 14.6
FEATURE [Sketcher::SketchObject] Sketch094  label="Sketch094 - forma centrale"
  ArcFitTolerance = 1e-06
  AttachmentSupport = -> [Pad019]
  ExternalGeometry = -> [Binder]
  FullyConstrained = true
  MakeInternals = false
  MapMode = 5
  Placement = pos=(0,2,0) rot=(0,0.707107,0.707107;3.14159rad)
  sketch-geometry (4):
    g0: LineSegment StartX=137.815 StartY=39.2 StartZ=0 EndX=142.655 EndY=24.303 EndZ=0
    g1: LineSegment StartX=110.815 StartY=24.303 StartZ=0 EndX=142.655 EndY=24.303 EndZ=0
    g2: LineSegment StartX=137.815 StartY=39.2 StartZ=0 EndX=110.815 EndY=39.2 EndZ=0
    g3: ArcOfCircle CenterX=92.2534 CenterY=31.7515 CenterZ=0 NormalX=0 NormalY=0 NormalZ=1 AngleXU=0 Radius=20 StartAngle=5.90156 EndAngle=6.66481
  constraints (12):
    c: PointOnObject(g0,g-3)
    c: Tangent(g0,g-5)
    c: Horizontal(g1)
    c: Coincident(g1,g0)
    c: Coincident(g2,g0)
    c: PointOnObject(g2,g-3)
    c: DistanceX(g2,g2) = 27
    c: Vertical(g1,g2)
    c: Coincident(g3,g2)
    c: Radius(g3) = 20
    c: Coincident(g3,g1)
    c: DistanceY(g-6,g0) = 4
FEATURE [Sketcher::SketchObject] Sketch095  label="Sketch095 - forma posteriore"
  ArcFitTolerance = 1e-06
  AttachmentSupport = -> [Pad019]
  ExternalGeometry = -> [Binder]
  FullyConstrained = true
  MakeInternals = false
  MapMode = 5
  Placement = pos=(0,2,0) rot=(0,0.707107,0.707107;3.14159rad)
  sketch-geometry (15):
    g0: LineSegment StartX=137.815 StartY=39.2 StartZ=0 EndX=143.955 EndY=20.303 EndZ=0
    g1: LineSegment StartX=143.955 StartY=20.303 StartZ=0 EndX=190.141 EndY=20.303 EndZ=0
    g2: ArcOfCircle CenterX=184.08 CenterY=34.8 CenterZ=0 NormalX=0 NormalY=0 NormalZ=1 AngleXU=0 Radius=3.5 StartAngle=3.49066 EndAngle=4.71239
    g3: LineSegment StartX=180.791 StartY=33.6029 StartZ=0 EndX=178.754 EndY=39.2 EndZ=0
    g4: LineSegment StartX=184.08 StartY=31.3 StartZ=0 EndX=186.139 EndY=31.3 EndZ=0
    g5: LineSegment StartX=190.141 StartY=20.303 StartZ=0 EndX=186.139 EndY=31.3 EndZ=0
    g6: LineSegment StartX=137.815 StartY=39.2 StartZ=0 EndX=156.815 EndY=39.2 EndZ=0
    g7: LineSegment StartX=178.754 StartY=39.2 StartZ=0 EndX=168.815 EndY=39.2 EndZ=0
    g8: LineSegment StartX=156.815 StartY=31.2 StartZ=0 EndX=168.815 EndY=31.2 EndZ=0
    g9: ArcOfCircle CenterX=176.411 CenterY=35.2 CenterZ=0 NormalX=0 NormalY=0 NormalZ=1 AngleXU=0 Radius=20 StartAngle=2.94023 EndAngle=3.34295
    g10: ArcOfCircle CenterX=188.411 CenterY=35.2 CenterZ=0 NormalX=0 NormalY=0 NormalZ=1 AngleXU=0 Radius=20 StartAngle=2.94023 EndAngle=3.34295
    g11: LineSegment StartX=157.815 StartY=39.2 StartZ=0 EndX=167.815 EndY=39.2 EndZ=0
    g12: LineSegment StartX=157.436 StartY=36.2 StartZ=0 EndX=167.436 EndY=36.2 EndZ=0
    g13: ArcOfCircle CenterX=177.411 CenterY=35.2 CenterZ=0 NormalX=0 NormalY=0 NormalZ=1 AngleXU=0 Radius=20 StartAngle=2.94023 EndAngle=3.09157
    g14: ArcOfCircle CenterX=187.411 CenterY=35.2 CenterZ=0 NormalX=0 NormalY=0 NormalZ=1 AngleXU=0 Radius=20 StartAngle=2.94023 EndAngle=3.09157
  constraints (46):
    c: PointOnObject(g0,g-3)
    c: Tangent(g0,g-6)
    c: Coincident(g1,g0)
    c: Horizontal(g1)
    c: Radius(g2) = 3.5
    c: Coincident(g2,g-5)
    c: PointOnObject(g3,g-3)
    c: Parallel(g3,g-4)
    c: Tangent(g3,g2) = 1.5708
    c: Horizontal(g4)
    c: Tangent(g4,g2) = -1.5708
    c: Coincident(g5,g1)
    c: Parallel(g5,g-4)
    c: Coincident(g5,g4)
    c: DistanceX(g4,g-8) = 3.8
    c: Coincident(g6,g0)
    c: PointOnObject(g6,g-3)
    c: Coincident(g7,g3)
    c: PointOnObject(g7,g-3)
    c: Horizontal(g8)
    c: DistanceX(g6,g7) = 12
    c: Vertical(g8,g6)
    c: Vertical(g7,g8)
    c: DistanceY(g8,g6) = 8
    c: Coincident(g9,g8)
    c: Coincident(g9,g6)
    c: Coincident(g10,g7)
    c: Coincident(g10,g8)
    c: Radius(g9) = 20
    c: Radius(g10) = 20
    c: PointOnObject(g11,g-3)
    c: PointOnObject(g11,g-3)
    c: DistanceX(g11,g11) = 10
    c: DistanceX(g6,g11) = 1
    c: Horizontal(g12)
    c: Equal(g12,g11)
    c: DistanceY(g12,g11) = 3
    c: Coincident(g13,g11)
    c: Coincident(g13,g12)
    c: Radius(g13) = 20
    c: Coincident(g14,g11)
    c: Coincident(g14,g12)
    c: Radius(g14) = 20
    c: DistanceX(g0,g6) = 19
    c: Horizontal(g9,g13)
    c: Horizontal(g0,g-4)
FEATURE [Sketcher::SketchObject] Sketch096  label="Sketch096 - forma impugnatura"
  ArcFitTolerance = 1e-06
  AttachmentSupport = -> [Pad019]
  ExternalGeometry = -> [Binder]
  FullyConstrained = true
  MakeInternals = false
  MapMode = 5
  Placement = pos=(0,2,0) rot=(0,0.707107,0.707107;3.14159rad)
  sketch-geometry (8):
    g0: LineSegment StartX=176.685 StartY=-80.4316 StartZ=0 EndX=143.955 EndY=20.303 EndZ=0
    g1: LineSegment StartX=176.685 StartY=-80.4316 StartZ=0 EndX=215.932 EndY=-80.4316 EndZ=0
    g2: Circle CenterX=179.305 CenterY=-76.8316 CenterZ=0 NormalX=0 NormalY=0 NormalZ=1 AngleXU=0 Radius=3
    g3: Circle CenterX=213.443 CenterY=-76.8316 CenterZ=0 NormalX=0 NormalY=0 NormalZ=1 AngleXU=0 Radius=3
    g4: LineSegment StartX=143.955 StartY=20.303 StartZ=0 EndX=202.765 EndY=20.303 EndZ=0
    g5: LineSegment StartX=215.42 StartY=-53.0314 StartZ=0 EndX=192.176 EndY=-3.18451 EndZ=0
    g6: ArcOfCircle CenterX=184.801 CenterY=-67.3089 CenterZ=0 NormalX=0 NormalY=0 NormalZ=1 AngleXU=0 Radius=33.7833 StartAngle=5.88425 EndAngle=6.71952
    g7: ArcOfCircle CenterX=207.583 CenterY=4 CenterZ=0 NormalX=0 NormalY=0 NormalZ=1 AngleXU=0 Radius=17 StartAngle=1.85815 EndAngle=3.57792
  constraints (19):
    c: Coincident(g0,g-4)
    c: PointOnObject(g0,g-3)
    c: Horizontal(g0,g-7)
    c: Coincident(g1,g0)
    c: Coincident(g1,g-5)
    c: Diameter(g2) = 6
    c: Diameter(g3) = 6
    c: Coincident(g2,g-9)
    c: Coincident(g3,g-10)
    c: Coincident(g4,g0)
    c: Coincident(g5,g-6)
    c: Coincident(g6,g1)
    c: Coincident(g6,g5)
    c: Equal(g-5,g6)
    c: Coincident(g5,g-7)
    c: Coincident(g4,g-7)
    c: Tangent(g7,g-7)
    c: Coincident(g7,g4)
    c: Coincident(g7,g5)
FEATURE [Sketcher::SketchObject] Sketch097
  ArcFitTolerance = 1e-06
  AttachmentSupport = -> [Pad019]
  ExternalGeometry = -> [Binder]
  FullyConstrained = true
  MakeInternals = false
  MapMode = 5
  Placement = pos=(0,2,0) rot=(0,0.707107,0.707107;3.14159rad)
  sketch-geometry (4):
    g0: LineSegment StartX=90 StartY=36.8 StartZ=0 EndX=108 EndY=36.8 EndZ=0
    g1: LineSegment StartX=108 StartY=36.8 StartZ=0 EndX=108 EndY=26.8 EndZ=0
    g2: LineSegment StartX=108 StartY=26.8 StartZ=0 EndX=90 EndY=26.8 EndZ=0
    g3: ArcOfCircle CenterX=94 CenterY=31.8 CenterZ=0 NormalX=0 NormalY=0 NormalZ=1 AngleXU=0 Radius=6.40312 StartAngle=2.24554 EndAngle=4.03765
  constraints (13):
    c: Horizontal(g0)
    c: Coincident(g1,g0)
    c: Vertical(g1)
    c: DistanceX(g0,g0) = 18
    c: DistanceY(g1,g1) = 10
    c: Coincident(g2,g1)
    c: Horizontal(g2)
    c: Equal(g2,g0)
    c: DistanceY(g0,g-3) = 2.4
    c: Coincident(g3,g0)
    c: Coincident(g3,g2)
    c: DistanceX(g2,g3) = 4
    c: DistanceX(g-3,g0) = 90
FEATURE [PartDesign::Chamfer] Chamfer015
  Angle = 45
  Base = -> Pad019 [Edge19,Edge22,Edge79]
  BaseFeature = -> Pad019
  ChamferType = 0
  FlipDirection = false
  Refine = true
  Size = 1.9
  Size2 = 1
  SupportTransform = false
  Suppressed = false
  UseAllEdges = false
FEATURE [PartDesign::Pocket] Pocket002
  BaseFeature = -> Chamfer015
  Direction = (0,1,-2e-16)
  Length = 1.2
  Length2 = 5
  Profile = -> Sketch093
  ReferenceAxis = -> Sketch093 [N_Axis]
  Refine = true
  Suppressed = false
  Type = 0
FEATURE [PartDesign::Pad] Pad005
  BaseFeature = -> Pocket002
  Direction = (0,1,-2e-16)
  Length = 1.6
  Length2 = 10
  Profile = -> Sketch091
  ReferenceAxis = -> Sketch091 [N_Axis]
  Refine = true
  Suppressed = false
  Type = 0
FEATURE [Sketcher::SketchObject] Sketch092  label="Sketch092 - scavi per viti anteriori"
  ArcFitTolerance = 1e-06
  AttachmentSupport = -> [Pad005]
  ExternalGeometry = -> [Binder]
  FullyConstrained = true
  MakeInternals = false
  MapMode = 5
  Placement = pos=(0,3.6,0) rot=(0,0.707107,0.707107;3.14159rad)
  sketch-geometry (20):
    g0: ArcOfCircle CenterX=5.6 CenterY=7.6 CenterZ=0 NormalX=0 NormalY=0 NormalZ=1 AngleXU=0 Radius=3.5 StartAngle=0 EndAngle=1.5708
    g1: ArcOfCircle CenterX=5.6 CenterY=34.8 CenterZ=0 NormalX=0 NormalY=0 NormalZ=1 AngleXU=0 Radius=3.5 StartAngle=4.71239 EndAngle=6.28319
    g2: ArcOfCircle CenterX=78.51 CenterY=34.8 CenterZ=0 NormalX=0 NormalY=0 NormalZ=1 AngleXU=0 Radius=3.5 StartAngle=3.14159 EndAngle=4.71239
    g3: ArcOfCircle CenterX=78.51 CenterY=7.6 CenterZ=0 NormalX=0 NormalY=0 NormalZ=1 AngleXU=0 Radius=3.5 StartAngle=1.5708 EndAngle=3.14159
    g4: LineSegment StartX=0 StartY=3.2 StartZ=0 EndX=0 EndY=11.1 EndZ=0
    g5: LineSegment StartX=0 StartY=11.1 StartZ=0 EndX=5.6 EndY=11.1 EndZ=0
    g6: LineSegment StartX=0 StartY=3.2 StartZ=0 EndX=9.1 EndY=3.2 EndZ=0
    g7: LineSegment StartX=9.1 StartY=3.2 StartZ=0 EndX=9.1 EndY=7.6 EndZ=0
    g8: LineSegment StartX=0 StartY=39.2 StartZ=0 EndX=0 EndY=31.3 EndZ=0
    g9: LineSegment StartX=0 StartY=31.3 StartZ=0 EndX=5.6 EndY=31.3 EndZ=0
    g10: LineSegment StartX=0 StartY=39.2 StartZ=0 EndX=9.1 EndY=39.2 EndZ=0
    g11: LineSegment StartX=9.1 StartY=39.2 StartZ=0 EndX=9.1 EndY=34.8 EndZ=0
    g12: LineSegment StartX=82.8 StartY=39.2 StartZ=0 EndX=75.01 EndY=39.2 EndZ=0
    g13: LineSegment StartX=82.8 StartY=39.2 StartZ=0 EndX=82.8 EndY=31.3 EndZ=0
    g14: LineSegment StartX=82.8 StartY=31.3 StartZ=0 EndX=78.51 EndY=31.3 EndZ=0
    g15: LineSegment StartX=82.8 StartY=3.2 StartZ=0 EndX=75.01 EndY=3.2 EndZ=0
    g16: LineSegment StartX=75.01 StartY=3.2 StartZ=0 EndX=75.01 EndY=7.6 EndZ=0
    g17: LineSegment StartX=82.8 StartY=3.2 StartZ=0 EndX=82.8 EndY=11.1 EndZ=0
    g18: LineSegment StartX=82.8 StartY=11.1 StartZ=0 EndX=78.51 EndY=11.1 EndZ=0
    g19: LineSegment StartX=75.01 StartY=39.2 StartZ=0 EndX=75.01 EndY=34.8 EndZ=0
  constraints (48):
    c: Radius(g0) = 3.5
    c: Coincident(g0,g-10)
    c: Radius(g1) = 3.5
    c: Coincident(g1,g-9)
    c: Radius(g2) = 3.5
    c: Coincident(g2,g-8)
    c: Radius(g3) = 3.5
    c: Coincident(g3,g-7)
    c: Coincident(g4,g-5)
    c: PointOnObject(g4,g-4)
    c: Coincident(g5,g4)
    c: Horizontal(g5)
    c: Coincident(g6,g4)
    c: PointOnObject(g6,g-5)
    c: Coincident(g7,g6)
    c: Vertical(g7)
    c: Coincident(g8,g-4)
    c: PointOnObject(g8,g-4)
    c: Coincident(g9,g8)
    c: Horizontal(g9)
    c: Coincident(g10,g8)
    c: PointOnObject(g10,g-3)
    c: Coincident(g11,g10)
    c: Vertical(g11)
    c: PointOnObject(g12,g-3)
    c: PointOnObject(g12,g-3)
    c: Coincident(g13,g12)
    c: Vertical(g13)
    c: Coincident(g14,g13)
    c: Horizontal(g14)
    c: Coincident(g15,g-6)
    c: PointOnObject(g15,g-5)
    c: Coincident(g16,g15)
    c: Vertical(g16)
    c: Coincident(g17,g15)
    c: Coincident(g18,g17)
    c: Horizontal(g18)
    c: Tangent(g3,g18) = -1.5708
    c: Tangent(g16,g3) = 1.5708
    c: Coincident(g19,g12)
    c: Vertical(g19)
    c: Tangent(g2,g19) = -1.5708
    c: Tangent(g2,g14) = 1.5708
    c: Tangent(g0,g7) = -1.5708
    c: Tangent(g0,g5) = 1.5708
    c: Tangent(g9,g1) = -1.5708
    c: Tangent(g1,g11) = 1.5708
    c: Tangent(g17,g13)
FEATURE [PartDesign::Pocket] Pocket001
  BaseFeature = -> Pad005
  Direction = (0,-1,2e-16)
  Length = 1.6
  Length2 = 5
  Profile = -> Sketch092
  ReferenceAxis = -> Sketch092 [N_Axis]
  Refine = true
  Suppressed = false
  Type = 0
FEATURE [PartDesign::Pad] Pad006
  BaseFeature = -> Pocket001
  Direction = (0,1,-2e-16)
  Length = 0.8
  Length2 = 10
  Profile = -> Sketch094
  ReferenceAxis = -> Sketch094 [N_Axis]
  Refine = true
  Suppressed = false
  Type = 0
FEATURE [PartDesign::Pad] Pad007
  BaseFeature = -> Pad006
  Direction = (0,1,-2e-16)
  Length = 2
  Length2 = 10
  Profile = -> Sketch095
  ReferenceAxis = -> Sketch095 [N_Axis]
  Refine = true
  Suppressed = false
  Type = 0
FEATURE [PartDesign::Pad] Pad008  label="Pad008 - forma impugnatura"
  BaseFeature = -> Pad007
  Direction = (0,1,-2e-16)
  Length = 1.6
  Length2 = 10
  Profile = -> Sketch096
  ReferenceAxis = -> Sketch096 [N_Axis]
  Refine = true
  Suppressed = false
  Type = 0
FEATURE [PartDesign::Pad] Pad009
  BaseFeature = -> Pad008
  Direction = (0,1,-2e-16)
  Length = 1.6
  Length2 = 10
  Profile = -> Sketch097
  ReferenceAxis = -> Sketch097 [N_Axis]
  Refine = true
  Suppressed = false
  Type = 0
FEATURE [Sketcher::SketchObject] Sketch098
  ArcFitTolerance = 1e-06
  AttachmentSupport = -> [Pad006]
  ExternalGeometry = -> [Binder]
  FullyConstrained = true
  MakeInternals = false
  MapMode = 5
  Placement = pos=(0,2.8,-7e-16) rot=(0,0.707107,0.707107;3.14159rad)
  sketch-geometry (4):
    g0: LineSegment StartX=118 StartY=39.2 StartZ=0 EndX=129 EndY=39.2 EndZ=0
    g1: LineSegment StartX=120.599 StartY=31.2 StartZ=0 EndX=131.599 EndY=31.2 EndZ=0
    g2: LineSegment StartX=129 StartY=39.2 StartZ=0 EndX=131.599 EndY=31.2 EndZ=0
    g3: LineSegment StartX=118 StartY=39.2 StartZ=0 EndX=120.599 EndY=31.2 EndZ=0
  constraints (12):
    c: PointOnObject(g0,g-3)
    c: PointOnObject(g0,g-3)
    c: DistanceX(g0,g0) = 11
    c: Horizontal(g1)
    c: Equal(g1,g0)
    c: Coincident(g2,g0)
    c: Coincident(g3,g0)
    c: Parallel(g-4,g2)
    c: Coincident(g1,g2)
    c: Coincident(g1,g3)
    c: DistanceY(g1,g0) = 8
    c: DistanceX(g-3,g0) = 118
FEATURE [Sketcher::SketchObject] Sketch099
  ArcFitTolerance = 1e-06
  AttachmentSupport = -> [Pad008]
  ExternalGeometry = -> [Binder]
  FullyConstrained = true
  MakeInternals = false
  MapMode = 5
  Placement = pos=(0,3.6,0) rot=(0,0.707107,0.707107;3.14159rad)
  sketch-geometry (13):
    g0: LineSegment StartX=192.176 StartY=-3.18451 StartZ=0 EndX=196.804 EndY=-13.1108 EndZ=0
    g1: LineSegment [constr] StartX=202.765 StartY=20.303 StartZ=0 EndX=181.223 EndY=20.303 EndZ=0
    g2: LineSegment [constr] StartX=181.223 StartY=20.303 StartZ=0 EndX=181.223 EndY=-3.18451 EndZ=0
    g3: ArcOfCircle CenterX=181.223 CenterY=-20.3764 CenterZ=0 NormalX=0 NormalY=0 NormalZ=1 AngleXU=0 Radius=17.1918 StartAngle=0.436332 EndAngle=1.57079
    g4: ArcOfEllipse CenterX=181.223 CenterY=8.55923 CenterZ=0 NormalX=0 NormalY=0 NormalZ=1 MajorRadius=23.4779 MinorRadius=11.7437 AngleXU=0 StartAngle=1.5708 EndAngle=4.71239
    g5: LineSegment [constr] StartX=204.701 StartY=8.55923 StartZ=0 EndX=157.745 EndY=8.55923 EndZ=0
    g6: LineSegment [constr] StartX=181.223 StartY=20.303 StartZ=0 EndX=181.223 EndY=-3.18451 EndZ=0
    g7: GeomPoint [constr] X=201.553 Y=8.55923 Z=0
    g8: GeomPoint [constr] X=160.894 Y=8.55923 Z=0
    g9: GeomPoint [constr] X=181.223 Y=-3.18451 Z=0
    g10: LineSegment StartX=181.223 StartY=20.303 StartZ=0 EndX=202.765 EndY=20.303 EndZ=0
    g11: ArcOfCircle CenterX=207.583 CenterY=4 CenterZ=0 NormalX=0 NormalY=0 NormalZ=1 AngleXU=0 Radius=17 StartAngle=1.85815 EndAngle=3.57792
    g12: LineSegment [constr] StartX=172.411 StartY=39.2 StartZ=0 EndX=192.176 EndY=-3.18451 EndZ=0
  constraints (27):
    c: Coincident(g1,g-7)
    c: Horizontal(g1)
    c: Coincident(g2,g1)
    c: Vertical(g2)
    c: Horizontal(g2,g0)
    c: Coincident(g3,g0)
    c: Coincident(g3,g2)
    c: InternalAlignment(g5-g8 -> g4) x4
    c: Horizontal(g5)
    c: PointOnObject(g4,g2)
    c: Coincident(g4,g1)
    c: DistanceX(g-3,g5) = 10.1
    c: Coincident(g4,g2)
    c: Tangent(g3,g-5)
    c: PointOnObject(g9,g4)
    c: PointOnObject(g9,g3)
    c: Tangent(g4,g3,g9) = 1.5708
    c: Coincident(g10,g1)
    c: Coincident(g10,g1)
    c: Equal(g11,g-4)
    c: Coincident(g11,g1)
    c: Coincident(g11,g0)
    c: PointOnObject(g12,g-6)
    c: PointOnObject(g1,g12)
    c: Tangent(g12,g-5) = -1.5708
    c: Tangent(g0,g-5) = -1.5708
    c: Horizontal(g9,g12)
FEATURE [Sketcher::SketchObject] Sketch106  label="Sketch106 - smusso impuniatura interno"
  ArcFitTolerance = 1e-06
  AttachmentSupport = -> [Pad008]
  ExternalGeometry = -> [Pad008]
  FullyConstrained = true
  MakeInternals = false
  MapMode = 5
  Placement = pos=(0,-1.586e-13,-80.4316) rot=(1,0,0;3.14159rad)
  sketch-geometry (9):
    g0: LineSegment StartX=-176.685 StartY=-3.6 StartZ=0 EndX=-176.685 EndY=-1.492e-13 EndZ=0
    g1: LineSegment [constr] StartX=-176.685 StartY=-1.416e-13 StartZ=0 EndX=-176.685 EndY=-1.49e-13 EndZ=0
    g2: LineSegment [constr] StartX=-186.685 StartY=-3.6 StartZ=0 EndX=-186.685 EndY=-1.492e-13 EndZ=0
    g3: ArcOfEllipse CenterX=-186.685 CenterY=-1.49e-13 CenterZ=0 NormalX=0 NormalY=0 NormalZ=1 MajorRadius=10 MinorRadius=3.6 AngleXU=3.14159 StartAngle=1.5708 EndAngle=3.14159
    g4: LineSegment [constr] StartX=-196.685 StartY=-1.416e-13 StartZ=0 EndX=-176.685 EndY=-1.416e-13 EndZ=0
    g5: LineSegment [constr] StartX=-186.685 StartY=-3.6 StartZ=0 EndX=-186.685 EndY=3.6 EndZ=0
    g6: GeomPoint [constr] X=-196.015 Y=-1.416e-13 Z=0
    g7: GeomPoint [constr] X=-177.356 Y=-1.416e-13 Z=0
    g8: LineSegment StartX=-176.685 StartY=-3.6 StartZ=0 EndX=-186.685 EndY=-3.6 EndZ=0
  constraints (15):
    c: PointOnObject(g2,g-3)
    c: Coincident(g1,g-5)
    c: DistanceY(g1,g1) = 0
    c: Coincident(g0,g1)
    c: DistanceX(g2,g-5) = 10
    c: Vertical(g2)
    c: Horizontal(g2,g0)
    c: InternalAlignment(g4-g7 -> g3) x4
    c: Coincident(g3,g2)
    c: Horizontal(g4)
    c: Coincident(g3,g0)
    c: Tangent(g0,g-5) = 1.5708
    c: Coincident(g3,g2)
    c: Coincident(g8,g0)
    c: Coincident(g8,g2)
FEATURE [Sketcher::SketchObject] Sketch107  label="Sketch107 - smusso impugnatura esterno"
  ArcFitTolerance = 1e-06
  AttachmentSupport = -> [Pad008]
  ExternalGeometry = -> [Pad008]
  FullyConstrained = true
  MakeInternals = false
  MapMode = 5
  Placement = pos=(0,-1.586e-13,-80.4316) rot=(1,0,0;3.14159rad)
  sketch-geometry (9):
    g0: LineSegment [constr] StartX=-215.932 StartY=1.79e-14 StartZ=0 EndX=-215.932 EndY=2.71e-14 EndZ=0
    g1: LineSegment StartX=-215.932 StartY=-3.6 StartZ=0 EndX=-215.932 EndY=2.71e-14 EndZ=0
    g2: LineSegment StartX=-215.932 StartY=-3.6 StartZ=0 EndX=-205.932 EndY=-3.6 EndZ=0
    g3: LineSegment [constr] StartX=-205.932 StartY=-3.6 StartZ=0 EndX=-205.932 EndY=2.71e-14 EndZ=0
    g4: ArcOfEllipse CenterX=-205.932 CenterY=2.71e-14 CenterZ=0 NormalX=0 NormalY=0 NormalZ=1 MajorRadius=10 MinorRadius=3.6 AngleXU=3.14159 StartAngle=1e-16 EndAngle=1.5708
    g5: LineSegment [constr] StartX=-215.932 StartY=1.79e-14 StartZ=0 EndX=-195.932 EndY=1.79e-14 EndZ=0
    g6: LineSegment [constr] StartX=-205.932 StartY=-3.6 StartZ=0 EndX=-205.932 EndY=3.6 EndZ=0
    g7: GeomPoint [constr] X=-215.262 Y=2.76e-14 Z=0
    g8: GeomPoint [constr] X=-196.602 Y=1.78e-14 Z=0
  constraints (16):
    c: Coincident(g0,g-6)
    c: PointOnObject(g0,g-6)
    c: DistanceY(g0,g0) = 0
    c: Coincident(g1,g-6)
    c: Coincident(g1,g0)
    c: Tangent(g2,g-3)
    c: DistanceX(g2,g2) = 10
    c: Coincident(g3,g2)
    c: Vertical(g3)
    c: Horizontal(g3,g0)
    c: InternalAlignment(g5-g8 -> g4) x4
    c: Coincident(g4,g3)
    c: Horizontal(g5)
    c: Coincident(g4,g0)
    c: Coincident(g4,g2)
    c: PointOnObject(g2,g1)
FEATURE [Sketcher::SketchObject] Sketch108
  ArcFitTolerance = 1e-06
  AttachmentOffset = pos=(0,0,-1.6) rot=(0,0,1;0rad)
  AttachmentSupport = -> [Pad008]
  ExternalGeometry = -> [Binder]
  FullyConstrained = true
  MakeInternals = false
  MapMode = 5
  Placement = pos=(0,2,4e-16) rot=(0,0.707107,0.707107;3.14159rad)
  sketch-geometry (14):
    g0: LineSegment StartX=192.176 StartY=-3.18451 StartZ=0 EndX=193.827 EndY=-6.72678 EndZ=0
    g1: LineSegment [constr] StartX=202.765 StartY=20.303 StartZ=0 EndX=181.223 EndY=20.303 EndZ=0
    g2: LineSegment [constr] StartX=181.223 StartY=20.303 StartZ=0 EndX=181.223 EndY=1.30297 EndZ=0
    g3: ArcOfCircle CenterX=181.223 CenterY=-12.6042 CenterZ=0 NormalX=0 NormalY=0 NormalZ=1 AngleXU=0 Radius=13.9072 StartAngle=0.436332 EndAngle=1.5708
    g4: ArcOfEllipse CenterX=181.223 CenterY=10.803 CenterZ=0 NormalX=0 NormalY=0 NormalZ=1 MajorRadius=14.4779 MinorRadius=9.5 AngleXU=0 StartAngle=1.5708 EndAngle=4.71239
    g5: LineSegment [constr] StartX=195.701 StartY=10.803 StartZ=0 EndX=166.745 EndY=10.803 EndZ=0
    g6: LineSegment [constr] StartX=181.223 StartY=20.303 StartZ=0 EndX=181.223 EndY=1.30297 EndZ=0
    g7: GeomPoint [constr] X=192.148 Y=10.803 Z=0
    g8: GeomPoint [constr] X=170.298 Y=10.803 Z=0
    g9: LineSegment StartX=181.223 StartY=20.303 StartZ=0 EndX=202.765 EndY=20.303 EndZ=0
    g10: ArcOfCircle CenterX=207.583 CenterY=4 CenterZ=0 NormalX=0 NormalY=0 NormalZ=1 AngleXU=0 Radius=17 StartAngle=1.85815 EndAngle=3.57792
    g11: LineSegment [constr] StartX=172.411 StartY=39.2 StartZ=0 EndX=192.176 EndY=-3.18451 EndZ=0
    g12: GeomPoint [constr] X=181.223 Y=1.30297 Z=0
    g13: GeomPoint [constr] X=181.223 Y=1.30297 Z=0
  constraints (28):
    c: Coincident(g1,g-7)
    c: Horizontal(g1)
    c: Coincident(g2,g1)
    c: Vertical(g2)
    c: Coincident(g3,g2)
    c: InternalAlignment(g5-g8 -> g4) x4
    c: Horizontal(g5)
    c: PointOnObject(g4,g2)
    c: Coincident(g4,g1)
    c: DistanceX(g-3,g5) = 19.1
    c: Coincident(g4,g2)
    c: Coincident(g9,g1)
    c: Coincident(g9,g1)
    c: Coincident(g10,g1)
    c: Coincident(g10,g0)
    c: PointOnObject(g11,g-6)
    c: PointOnObject(g1,g11)
    c: DistanceY(g2,g1) = 19
    c: Coincident(g10,g-4)
    c: PointOnObject(g12,g4)
    c: PointOnObject(g12,g3)
    c: Tangent(g11,g-5) = -1.5708
    c: Tangent(g0,g-5) = -1.5708
    c: Tangent(g3,g0) = 1.5708
    c: PointOnObject(g13,g4)
    c: PointOnObject(g13,g3)
    c: Tangent(g4,g3,g13) = 1.5708
    c: Horizontal(g11,g0)
FEATURE [Part::Part2DObjectPython] Clone2D  label="Sketch108 (2D)"  # Draft 2D object (typed FeaturePython)
  Fuse = false
  Objects = -> [Sketch108]
  Placement = pos=(0,2,4e-16) rot=(0,0.707107,0.707107;3.14159rad)
  Scale = (1,1,1)
FEATURE [Sketcher::SketchObject] Sketch109
  ArcFitTolerance = 1e-06
  AttachmentOffset = pos=(0,0,-3.5) rot=(0,0,1;0rad)
  AttachmentSupport = -> [Pad008]
  ExternalGeometry = -> [Binder]
  FullyConstrained = true
  MakeInternals = false
  MapMode = 5
  Placement = pos=(0,0.1,8e-16) rot=(0,0.707107,0.707107;3.14159rad)
  sketch-geometry (1):
    g0: GeomPoint X=197.47 Y=8.55923 Z=0
  constraints (1):
    c: Symmetric(g-7,g-5,g0)
FEATURE [PartDesign::Chamfer] Chamfer005
  Angle = 45
  Base = -> Pad009 [Edge215,Edge212]
  BaseFeature = -> Pad009
  ChamferType = 1
  FlipDirection = false
  Refine = true
  Size = 1.5
  Size2 = 2.8
  SupportTransform = false
  Suppressed = false
  UseAllEdges = false
FEATURE [Sketcher::SketchObject] Sketch111
  ArcFitTolerance = 1e-06
  AttachmentSupport = -> [Pad009]
  ExternalGeometry = -> [Pad009]
  FullyConstrained = true
  MakeInternals = false
  MapMode = 5
  Placement = pos=(0,3.6,-8e-16) rot=(0,0.707107,0.707107;3.14159rad)
  sketch-geometry (21):
    g0: LineSegment [constr] StartX=97 StartY=36.8 StartZ=0 EndX=97 EndY=26.8 EndZ=0
    g1: LineSegment StartX=97 StartY=28.6 StartZ=0 EndX=97 EndY=27.8 EndZ=0
    g2: LineSegment StartX=97 StartY=27.8 StartZ=0 EndX=108 EndY=27.8 EndZ=0
    g3: LineSegment StartX=108 StartY=27.8 StartZ=0 EndX=108 EndY=28.6 EndZ=0
    g4: LineSegment StartX=108 StartY=28.6 StartZ=0 EndX=97 EndY=28.6 EndZ=0
    g5: LineSegment StartX=97 StartY=35.8 StartZ=0 EndX=97 EndY=35 EndZ=0
    g6: LineSegment StartX=97 StartY=35 StartZ=0 EndX=108 EndY=35 EndZ=0
    g7: LineSegment StartX=108 StartY=35 StartZ=0 EndX=108 EndY=35.8 EndZ=0
    g8: LineSegment StartX=108 StartY=35.8 StartZ=0 EndX=97 EndY=35.8 EndZ=0
    g9: LineSegment StartX=97 StartY=30.4 StartZ=0 EndX=97 EndY=29.6 EndZ=0
    g10: LineSegment StartX=97 StartY=29.6 StartZ=0 EndX=108 EndY=29.6 EndZ=0
    g11: LineSegment StartX=108 StartY=29.6 StartZ=0 EndX=108 EndY=30.4 EndZ=0
    g12: LineSegment StartX=108 StartY=30.4 StartZ=0 EndX=97 EndY=30.4 EndZ=0
    g13: LineSegment StartX=97 StartY=34 StartZ=0 EndX=97 EndY=33.2 EndZ=0
    g14: LineSegment StartX=97 StartY=33.2 StartZ=0 EndX=108 EndY=33.2 EndZ=0
    g15: LineSegment StartX=108 StartY=33.2 StartZ=0 EndX=108 EndY=34 EndZ=0
    g16: LineSegment StartX=108 StartY=34 StartZ=0 EndX=97 EndY=34 EndZ=0
    g17: LineSegment StartX=97 StartY=32.2 StartZ=0 EndX=97 EndY=31.4 EndZ=0
    g18: LineSegment StartX=97 StartY=31.4 StartZ=0 EndX=108 EndY=31.4 EndZ=0
    g19: LineSegment StartX=108 StartY=31.4 StartZ=0 EndX=108 EndY=32.2 EndZ=0
    g20: LineSegment StartX=108 StartY=32.2 StartZ=0 EndX=97 EndY=32.2 EndZ=0
  constraints (54):
    c: Vertical(g0)
    c: PointOnObject(g0,g-3)
    c: PointOnObject(g0,g-4)
    c: DistanceX(g0,g-5) = 11
    c: Coincident(g1,g2)
    c: Coincident(g2,g3)
    c: Coincident(g3,g4)
    c: Coincident(g4,g1)
    c: Horizontal(g2)
    c: Horizontal(g4)
    c: Tangent(g1,g0)
    c: Tangent(g3,g-5)
    c: DistanceY(g2,g3) = 0.8
    c: Coincident(g5,g6)
    c: Coincident(g6,g7)
    c: Coincident(g7,g8)
    c: Coincident(g8,g5)
    c: Horizontal(g6)
    c: Horizontal(g8)
    c: DistanceY(g6,g7) = 0.8
    c: Coincident(g9,g10)
    c: Coincident(g10,g11)
    c: Coincident(g11,g12)
    c: Coincident(g12,g9)
    c: Horizontal(g10)
    c: Horizontal(g12)
    c: DistanceY(g10,g11) = 0.8
    c: Tangent(g5,g0)
    c: Tangent(g7,g-5)
    c: Tangent(g9,g0)
    c: Tangent(g11,g-5)
    c: Coincident(g13,g14)
    c: Coincident(g14,g15)
    c: Coincident(g15,g16)
    c: Coincident(g16,g13)
    c: Horizontal(g14)
    c: Horizontal(g16)
    c: DistanceY(g14,g15) = 0.8
    c: Tangent(g13,g0)
    c: Tangent(g15,g-5)
    c: Coincident(g17,g18)
    c: Coincident(g18,g19)
    c: Coincident(g19,g20)
    c: Coincident(g20,g17)
    c: Horizontal(g18)
    c: Horizontal(g20)
    c: DistanceY(g18,g19) = 0.8
    c: Tangent(g17,g0)
    c: Tangent(g19,g-5)
    c: DistanceY(g1,g9) = 1
    c: DistanceY(g9,g17) = 1
    c: DistanceY(g17,g13) = 1
    c: DistanceY(g13,g5) = 1
    c: DistanceY(g0,g1) = 1
FEATURE [PartDesign::Pocket] Pocket004
  BaseFeature = -> Chamfer005
  Direction = (0,-1,2e-16)
  Length = 1
  Length2 = 5
  Profile = -> Sketch111
  ReferenceAxis = -> Sketch111 [N_Axis]
  Refine = true
  Suppressed = false
  Type = 0
FEATURE [PartDesign::Pad] Pad010
  BaseFeature = -> Pocket004
  Direction = (0,1,-2e-16)
  Length = 1.2
  Length2 = 10
  Profile = -> Sketch098
  ReferenceAxis = -> Sketch098 [N_Axis]
  Refine = true
  Suppressed = false
  Type = 0
FEATURE [PartDesign::Chamfer] Chamfer006
  Angle = 45
  Base = -> Pad010 [Edge291]
  BaseFeature = -> Pad010
  ChamferType = 1
  FlipDirection = false
  Refine = true
  Size = 1
  Size2 = 6
  SupportTransform = false
  Suppressed = false
  UseAllEdges = false
FEATURE [Sketcher::SketchObject] Sketch110
  ArcFitTolerance = 1e-06
  AttachmentSupport = -> [Pad010]
  ExternalGeometry = -> [Sketch098]
  FullyConstrained = true
  MakeInternals = false
  MapMode = 5
  Placement = pos=(0,4,-9e-16) rot=(0,0.707107,0.707107;3.14159rad)
  sketch-geometry (8):
    g0: LineSegment StartX=119.69 StartY=34 StartZ=0 EndX=130.69 EndY=34 EndZ=0
    g1: LineSegment StartX=119.95 StartY=33.2 StartZ=0 EndX=130.95 EndY=33.2 EndZ=0
    g2: LineSegment StartX=119.137 StartY=35.7 StartZ=0 EndX=130.137 EndY=35.7 EndZ=0
    g3: LineSegment StartX=118.877 StartY=36.5 StartZ=0 EndX=129.877 EndY=36.5 EndZ=0
    g4: LineSegment StartX=118.877 StartY=36.5 StartZ=0 EndX=119.137 EndY=35.7 EndZ=0
    g5: LineSegment StartX=129.877 StartY=36.5 StartZ=0 EndX=130.137 EndY=35.7 EndZ=0
    g6: LineSegment StartX=119.69 StartY=34 StartZ=0 EndX=119.95 EndY=33.2 EndZ=0
    g7: LineSegment StartX=130.69 StartY=34 StartZ=0 EndX=130.95 EndY=33.2 EndZ=0
  constraints (24):
    c: Horizontal(g0)
    c: Horizontal(g1)
    c: Horizontal(g2)
    c: Horizontal(g3)
    c: Equal(g1,g-5)
    c: Equal(g0,g-5)
    c: Equal(g2,g-5)
    c: Equal(g3,g-5)
    c: PointOnObject(g0,g-3)
    c: PointOnObject(g1,g-3)
    c: PointOnObject(g2,g-3)
    c: PointOnObject(g3,g-3)
    c: Coincident(g4,g3)
    c: Coincident(g4,g2)
    c: Coincident(g5,g3)
    c: Coincident(g5,g2)
    c: Coincident(g6,g0)
    c: Coincident(g6,g1)
    c: Coincident(g7,g0)
    c: Coincident(g7,g1)
    c: DistanceY(g1,g0) = 0.8
    c: DistanceY(g2,g3) = 0.8
    c: DistanceY(g-5,g1) = 2
    c: DistanceY(g-5,g2) = 4.5
FEATURE [PartDesign::Pocket] Pocket003
  BaseFeature = -> Chamfer006
  Direction = (0,-1,2e-16)
  Length = 1
  Length2 = 5
  Profile = -> Sketch110
  ReferenceAxis = -> Sketch110 [N_Axis]
  Refine = true
  Suppressed = false
  Type = 0
FEATURE [PartDesign::SubtractivePipe] SubtractivePipe
  AuxilleryCurvelinear = true
  AuxillerySpineTangent = false
  BaseFeature = -> Pocket003
  Binormal = (0,0,0)
  Mode = 0
  Profile = -> Sketch106
  Refine = true
  Spine = -> Pad008 [Edge215]
  SpineTangent = false
  Suppressed = false
  Transformation = 0
  Transition = 0
FEATURE [PartDesign::SubtractivePipe] SubtractivePipe001
  AuxilleryCurvelinear = true
  AuxillerySpineTangent = false
  BaseFeature = -> SubtractivePipe
  Binormal = (0,0,0)
  Mode = 0
  Profile = -> Sketch107
  Refine = true
  Spine = -> Pad008 [Edge213,Edge216,Edge210]
  SpineTangent = false
  Suppressed = false
  Transformation = 0
  Transition = 0
FEATURE [PartDesign::SubtractiveLoft] SubtractiveLoft
  BaseFeature = -> SubtractivePipe001
  Closed = false
  Profile = -> Sketch099
  Refine = true
  Ruled = false
  Sections = -> [Sketch108]
  Suppressed = false
FEATURE [PartDesign::SubtractiveLoft] SubtractiveLoft001
  BaseFeature = -> SubtractiveLoft
  Closed = false
  Profile = -> Clone2D
  Refine = true
  Ruled = false
  Sections = -> [Sketch109]
  Suppressed = false
FEATURE [Sketcher::SketchObject] Sketch112
  ArcFitTolerance = 1e-06
  AttachmentSupport = -> [Pad008]
  ExternalGeometry = -> [Binder]
  FullyConstrained = true
  MakeInternals = false
  MapMode = 5
  Placement = pos=(0,3.6,0) rot=(0,0.707107,0.707107;3.14159rad)
  sketch-geometry (4):
    g0: LineSegment [constr] StartX=167.782 StartY=-53.0314 StartZ=0 EndX=215.42 EndY=-53.0314 EndZ=0
    g1: GeomPoint [constr] X=191.282 Y=-53.0314 Z=0
    g2: Circle CenterX=191.282 CenterY=-53.0314 CenterZ=0 NormalX=0 NormalY=0 NormalZ=1 AngleXU=0 Radius=11.5
    g3: Circle CenterX=191.282 CenterY=-53.0314 CenterZ=0 NormalX=0 NormalY=0 NormalZ=1 AngleXU=0 Radius=10.7
  constraints (9):
    c: Horizontal(g0)
    c: PointOnObject(g0,g-3)
    c: Diameter(g2) = 23
    c: Coincident(g2,g1)
    c: Diameter(g3) = 21.4
    c: Coincident(g3,g1)
    c: DistanceX(g0,g1) = 23.5
    c: PointOnObject(g1,g0)
    c: Coincident(g0,g-4)
FEATURE [PartDesign::Chamfer] Chamfer016
  Angle = 45
  Base = -> SubtractiveLoft001 [Edge118,Edge117,Edge119,Edge120,Edge109]
  BaseFeature = -> SubtractiveLoft001
  ChamferType = 0
  FlipDirection = false
  Refine = true
  Size = 1.5
  Size2 = 1
  SupportTransform = false
  Suppressed = false
  UseAllEdges = false
FEATURE [PartDesign::Chamfer] Chamfer017
  Angle = 45
  Base = -> Chamfer016 [Edge15]
  BaseFeature = -> Chamfer016
  ChamferType = 0
  FlipDirection = false
  Refine = true
  Size = 1.6
  Size2 = 1
  SupportTransform = false
  Suppressed = false
  UseAllEdges = false
FEATURE [PartDesign::Chamfer] Chamfer018
  Angle = 45
  Base = -> Chamfer017 [Edge10]
  BaseFeature = -> Chamfer017
  ChamferType = 0
  FlipDirection = false
  Refine = true
  Size = 3.5
  Size2 = 1
  SupportTransform = false
  Suppressed = false
  UseAllEdges = false
FEATURE [PartDesign::Chamfer] Chamfer019
  Angle = 45
  Base = -> Chamfer018 [Edge94,Edge199]
  BaseFeature = -> Chamfer018
  ChamferType = 0
  FlipDirection = false
  Refine = true
  Size = 1.9
  Size2 = 1
  SupportTransform = false
  Suppressed = false
  UseAllEdges = false
FEATURE [PartDesign::Fillet] Fillet009
  Base = -> Chamfer019 [Edge83]
  BaseFeature = -> Chamfer019
  Radius = 1.1
  Refine = true
  SupportTransform = false
  Suppressed = false
  UseAllEdges = false
FEATURE [PartDesign::Fillet] Fillet010
  Base = -> Fillet009 [Edge77]
  BaseFeature = -> Fillet009
  Radius = 1.9
  Refine = true
  SupportTransform = false
  Suppressed = false
  UseAllEdges = false
FEATURE [PartDesign::Pocket] Pocket005
  BaseFeature = -> Fillet010
  Direction = (0,-1,2e-16)
  Length = 0.8
  Length2 = 5
  Profile = -> Sketch112
  ReferenceAxis = -> Sketch112 [N_Axis]
  Refine = true
  Suppressed = false
  Type = 0
FEATURE [Part::Part2DObjectPython] ShapeString001  # Draft 2D object (typed FeaturePython)
  FontFile = <path>
  Fuse = false
  Justification = 6
  JustificationReference = 0
  KeepLeftMargin = false
  MakeFace = true
  ObliqueAngle = 0
  Placement = pos=(-183.5,3.6,-57.5) rot=(0,0.707107,0.707107;3.14159rad)
  ScaleToSize = true
  Size = 10
  String = AS
  Tracking = 0
FEATURE [PartDesign::Pocket] Pocket013
  BaseFeature = -> Pocket005
  Direction = (-1e-16,-1,2e-16)
  Length = 1
  Length2 = 5
  Profile = -> ShapeString001
  ReferenceAxis = -> ShapeString001 [N_Axis]
  Refine = true
  Suppressed = false
  Type = 0
FEATURE [PartDesign::Body] Body006  label="lato SX"
  AllowCompound = false
  Group = -> [Binder,Pad019,Chamfer015,Pocket002,Sketch133,Sketch091,Pad005,Sketch092,Pocket001,Sketch093,Sketch094,Pad006,Sketch095,Pad007,Sketch096,Pad008,Sketch097,Pad009,Chamfer005,Pocket004,Sketch098,Pad010,Chamfer006,Pocket003,SubtractivePipe,SubtractivePipe001,Sketch099,Sketch106,Sketch107,Sketch108,Clone2D,Sketch109,SubtractiveLoft,SubtractiveLoft001,Sketch110,Sketch111,Sketch112,Chamfer016,Chamfer017,+7 more]
  Origin = -> Origin006
  Tip = -> Pocket013
FEATURE [PartDesign::Pad] Pad020
  Direction = (0,-1,2e-16)
  Length = 25.2
  Length2 = 10
  Midplane = true
  Placement = pos=(0,0,0) rot=(1,0,0;1.5708rad)
  Profile = -> Sketch021
  ReferenceAxis = -> Sketch021 [N_Axis]
  Refine = true
  Suppressed = false
  Type = 0
FEATURE [PartDesign::Body] Body001  label="perno fermo rumble e driver solenoide"
  AllowCompound = false
  Group = -> [Sketch021,Pad020]
  Origin = -> Origin001
  Tip = -> Pad020
FEATURE [PartDesign::Pad] Pad021
  Direction = (0,-1,2e-16)
  Length = 16.8
  Length2 = 10
  Midplane = true
  Placement = pos=(0,0,0) rot=(1,0,0;1.5708rad)
  Profile = -> Sketch061
  ReferenceAxis = -> Sketch061 [N_Axis]
  Refine = true
  Suppressed = false
  Type = 0
FEATURE [PartDesign::Pocket] Pocket014
  BaseFeature = -> Pad021
  Direction = (0,1,-2e-16)
  Length = 12.8
  Length2 = 5
  Midplane = true
  Placement = pos=(0,0,0) rot=(1,0,0;1.5708rad)
  Profile = -> Sketch062
  ReferenceAxis = -> Sketch062 [N_Axis]
  Refine = true
  Suppressed = false
  Type = 0
FEATURE [PartDesign::Pad] Pad022
  BaseFeature = -> Pocket014
  Direction = (0,-1,2e-16)
  Length = 7.6
  Length2 = 10
  Midplane = true
  Placement = pos=(0,0,0) rot=(1,0,0;1.5708rad)
  Profile = -> Sketch063
  ReferenceAxis = -> Sketch063 [N_Axis]
  Refine = true
  Suppressed = false
  Type = 0
FEATURE [PartDesign::Body] Body003  label="blocco switch"
  AllowCompound = false
  Group = -> [Sketch061,Sketch062,Sketch063,Pad021,Pocket014,Pad022]
  Origin = -> Origin003
  Tip = -> Pad022
FEATURE [PartDesign::Pad] Pad024
  Direction = (0,-1,2e-16)
  Length = 17
  Length2 = 10
  Midplane = true
  Placement = pos=(0,0,0) rot=(1,0,0;1.5708rad)
  Profile = -> Sketch045
  ReferenceAxis = -> Sketch045 [N_Axis]
  Refine = true
  Suppressed = false
  Type = 0
FEATURE [PartDesign::Pocket] Pocket015
  BaseFeature = -> Pad024
  Direction = (-1,0,0)
  Length = 8
  Length2 = 5
  Placement = pos=(0,0,0) rot=(1,0,0;1.5708rad)
  Profile = -> Sketch047
  ReferenceAxis = -> Sketch047 [N_Axis]
  Refine = true
  Reversed = true
  Suppressed = false
  Type = 0
FEATURE [PartDesign::Pocket] Pocket016
  BaseFeature = -> Pocket015
  Direction = (-1,0,0)
  Length = 1
  Length2 = 5
  Placement = pos=(0,0,0) rot=(1,0,0;1.5708rad)
  Profile = -> Sketch046
  ReferenceAxis = -> Sketch046 [N_Axis]
  Refine = true
  Reversed = true
  Suppressed = false
  Type = 0
FEATURE [PartDesign::Pocket] Pocket017
  BaseFeature = -> Pocket016
  Direction = (0,1,-2e-16)
  Length = 17
  Length2 = 5
  Midplane = true
  Placement = pos=(0,0,0) rot=(1,0,0;1.5708rad)
  Profile = -> Sketch048
  ReferenceAxis = -> Sketch048 [N_Axis]
  Refine = true
  Suppressed = false
  Type = 0
FEATURE [PartDesign::Pad] Pad025
  BaseFeature = -> Pocket017
  Direction = (0,-1,2e-16)
  Length = 17
  Length2 = 10
  Midplane = true
  Placement = pos=(0,0,0) rot=(1,0,0;1.5708rad)
  Profile = -> Sketch049
  ReferenceAxis = -> Sketch049 [N_Axis]
  Refine = true
  Suppressed = false
  Type = 0
FEATURE [PartDesign::Pad] Pad026
  BaseFeature = -> Pad025
  Direction = (0,-1,2e-16)
  Length = 17
  Length2 = 10
  Midplane = true
  Placement = pos=(0,0,0) rot=(1,0,0;1.5708rad)
  Profile = -> Sketch066
  ReferenceAxis = -> Sketch066 [N_Axis]
  Refine = true
  Suppressed = false
  Type = 0
FEATURE [PartDesign::Pad] Pad027
  BaseFeature = -> Pad026
  Direction = (0,-1,2e-16)
  Length = 5
  Length2 = 10
  Midplane = true
  Placement = pos=(0,0,0) rot=(1,0,0;1.5708rad)
  Profile = -> Sketch064
  ReferenceAxis = -> Sketch064 [N_Axis]
  Refine = true
  Suppressed = false
  Type = 0
FEATURE [PartDesign::Pad] Pad028
  BaseFeature = -> Pad027
  Direction = (1,0,0)
  Length = 1
  Length2 = 10
  Placement = pos=(0,0,0) rot=(1,0,0;1.5708rad)
  Profile = -> Sketch068
  ReferenceAxis = -> Sketch068 [N_Axis]
  Refine = true
  Reversed = true
  Suppressed = false
  Type = 0
FEATURE [PartDesign::Chamfer] Chamfer020
  Angle = 45
  Base = -> Pad028 [Edge73,Edge75,Edge78,Edge77]
  BaseFeature = -> Pad028
  ChamferType = 0
  FlipDirection = false
  Placement = pos=(0,0,0) rot=(1,0,0;1.5708rad)
  Refine = true
  Size = 0.5
  Size2 = 1
  SupportTransform = false
  Suppressed = false
  UseAllEdges = false
FEATURE [PartDesign::Body] Body002  label="supporto per neopixel"
  AllowCompound = false
  Group = -> [Sketch045,Sketch047,Sketch046,Sketch048,Sketch049,Sketch066,Sketch064,Sketch068,Pad024,Pocket015,Pocket016,Pocket017,Pad025,Pad026,Pad027,Pad028,Chamfer020]
  Origin = -> Origin002
  Tip = -> Chamfer020
FEATURE [Sketcher::SketchObject] Sketch134  label="perno fermo rumble002"
  ArcFitTolerance = 1e-06
  AttachmentSupport = -> [XZ_Plane008]
  FullyConstrained = true
  MakeInternals = false
  MapMode = 5
  Placement = pos=(0,0,0) rot=(1,0,0;1.5708rad)
  sketch-geometry (16):
    g0: LineSegment StartX=0 StartY=0.45 StartZ=0 EndX=0 EndY=1.55 EndZ=0
    g1: LineSegment StartX=0.45 StartY=2 StartZ=0 EndX=1.55 EndY=2 EndZ=0
    g2: LineSegment StartX=2 StartY=1.55 StartZ=0 EndX=2 EndY=0.45 EndZ=0
    g3: LineSegment StartX=1.55 StartY=0 StartZ=0 EndX=0.45 EndY=0 EndZ=0
    g4: ArcOfCircle [constr] CenterX=0.45 CenterY=1.55 CenterZ=0 NormalX=0 NormalY=0 NormalZ=1 AngleXU=0 Radius=0.45 StartAngle=1.5708 EndAngle=3.14159
    g5: GeomPoint [constr] X=0 Y=2 Z=0
    g6: LineSegment StartX=0.45 StartY=2 StartZ=0 EndX=0 EndY=1.55 EndZ=0
    g7: ArcOfCircle [constr] CenterX=1.55 CenterY=1.55 CenterZ=0 NormalX=0 NormalY=0 NormalZ=1 AngleXU=0 Radius=0.45 StartAngle=0 EndAngle=1.5708
    g8: GeomPoint [constr] X=2 Y=2 Z=0
    g9: LineSegment StartX=2 StartY=1.55 StartZ=0 EndX=1.55 EndY=2 EndZ=0
    g10: ArcOfCircle [constr] CenterX=1.55 CenterY=0.45 CenterZ=0 NormalX=0 NormalY=0 NormalZ=1 AngleXU=0 Radius=0.45 StartAngle=4.71239 EndAngle=6.28319
    g11: GeomPoint [constr] X=2 Y=0 Z=0
    g12: LineSegment StartX=1.55 StartY=0 StartZ=0 EndX=2 EndY=0.45 EndZ=0
    g13: ArcOfCircle [constr] CenterX=0.45 CenterY=0.45 CenterZ=0 NormalX=0 NormalY=0 NormalZ=1 AngleXU=0 Radius=0.45 StartAngle=3.14159 EndAngle=4.71239
    g14: GeomPoint [constr] X=0 Y=0 Z=0
    g15: LineSegment StartX=0 StartY=0.45 StartZ=0 EndX=0.45 EndY=0 EndZ=0
  constraints (35):
    c: Coincident(g14,g-1)
    c: PointOnObject(g5,g-2)
    c: Horizontal(g1)
    c: Vertical(g2)
    c: Horizontal(g3)
    c: DistanceX(g5,g8) = 2
    c: DistanceY(g11,g8) = 2
    c: PointOnObject(g5,g0)
    c: PointOnObject(g5,g1)
    c: Tangent(g0,g4) = 1.5708
    c: Tangent(g1,g4) = 1.5708
    c: Coincident(g6,g0)
    c: Coincident(g6,g1)
    c: PointOnObject(g8,g2)
    c: PointOnObject(g8,g1)
    c: Tangent(g2,g7) = 1.5708
    c: Tangent(g1,g7) = 1.5708
    c: Coincident(g9,g2)
    c: Coincident(g9,g1)
    c: PointOnObject(g11,g2)
    c: PointOnObject(g11,g3)
    c: Tangent(g2,g10) = 1.5708
    c: Tangent(g3,g10) = 1.5708
    c: Coincident(g12,g2)
    c: Coincident(g12,g3)
    c: PointOnObject(g14,g0)
    c: PointOnObject(g14,g3)
    c: Tangent(g0,g13) = 1.5708
    c: Tangent(g3,g13) = 1.5708
    c: Coincident(g15,g0)
    c: Coincident(g15,g3)
    c: Equal(g6,g9)
    c: Equal(g9,g12)
    c: Equal(g12,g15)
    c: DistanceX(g14,g3) = 0.45
FEATURE [PartDesign::Pad] Pad029
  Direction = (0,-1,2e-16)
  Length = 17
  Length2 = 10
  Midplane = true
  Placement = pos=(0,0,0) rot=(1,0,0;1.5708rad)
  Profile = -> Sketch134
  ReferenceAxis = -> Sketch134 [N_Axis]
  Refine = true
  Suppressed = false
  Type = 0
FEATURE [PartDesign::Body] Body008  label="perno fermo neopixel"
  AllowCompound = false
  Group = -> [Sketch134,Pad029]
  Origin = -> Origin008
  Tip = -> Pad029
FEATURE [Sketcher::SketchObject] Sketch135  label="perno fermo rumble003"
  ArcFitTolerance = 1e-06
  AttachmentSupport = -> [XZ_Plane009]
  FullyConstrained = true
  MakeInternals = false
  MapMode = 5
  Placement = pos=(0,0,0) rot=(1,0,0;1.5708rad)
  sketch-geometry (16):
    g0: LineSegment StartX=4.69e-14 StartY=0.8 StartZ=0 EndX=-3.04e-14 EndY=3.1 EndZ=0
    g1: LineSegment StartX=0.8 StartY=3.9 StartZ=0 EndX=3.1 EndY=3.9 EndZ=0
    g2: LineSegment StartX=3.9 StartY=3.1 StartZ=0 EndX=3.9 EndY=0.8 EndZ=0
    g3: LineSegment StartX=3.1 StartY=0 StartZ=0 EndX=0.8 EndY=0 EndZ=0
    g4: ArcOfCircle [constr] CenterX=0.8 CenterY=3.1 CenterZ=0 NormalX=0 NormalY=0 NormalZ=1 AngleXU=0 Radius=0.8 StartAngle=1.5708 EndAngle=3.14159
    g5: GeomPoint [constr] X=0 Y=3.9 Z=0
    g6: LineSegment StartX=0.8 StartY=3.9 StartZ=0 EndX=-3.04e-14 EndY=3.1 EndZ=0
    g7: ArcOfCircle [constr] CenterX=3.1 CenterY=3.1 CenterZ=0 NormalX=0 NormalY=0 NormalZ=1 AngleXU=0 Radius=0.8 StartAngle=-2.4e-14 EndAngle=1.5708
    g8: GeomPoint [constr] X=3.9 Y=3.9 Z=0
    g9: LineSegment StartX=3.9 StartY=3.1 StartZ=0 EndX=3.1 EndY=3.9 EndZ=0
    g10: ArcOfCircle [constr] CenterX=3.1 CenterY=0.8 CenterZ=0 NormalX=0 NormalY=0 NormalZ=1 AngleXU=0 Radius=0.8 StartAngle=4.71239 EndAngle=6.28319
    g11: GeomPoint [constr] X=3.9 Y=0 Z=0
    g12: LineSegment StartX=3.1 StartY=0 StartZ=0 EndX=3.9 EndY=0.8 EndZ=0
    g13: ArcOfCircle [constr] CenterX=0.8 CenterY=0.8 CenterZ=0 NormalX=0 NormalY=0 NormalZ=1 AngleXU=0 Radius=0.8 StartAngle=3.14159 EndAngle=4.71239
    g14: GeomPoint [constr] X=0 Y=0 Z=0
    g15: LineSegment StartX=4.69e-14 StartY=0.8 StartZ=0 EndX=0.8 EndY=0 EndZ=0
  constraints (35):
    c: Coincident(g14,g-1)
    c: PointOnObject(g5,g-2)
    c: Horizontal(g1)
    c: Vertical(g2)
    c: Horizontal(g3)
    c: DistanceX(g5,g8) = 3.9
    c: DistanceY(g11,g8) = 3.9
    c: PointOnObject(g5,g0)
    c: PointOnObject(g5,g1)
    c: Tangent(g0,g4) = 1.5708
    c: Tangent(g1,g4) = 1.5708
    c: Coincident(g6,g0)
    c: Coincident(g6,g1)
    c: PointOnObject(g8,g2)
    c: PointOnObject(g8,g1)
    c: Tangent(g2,g7) = 1.5708
    c: Tangent(g1,g7) = 1.5708
    c: Coincident(g9,g2)
    c: Coincident(g9,g1)
    c: PointOnObject(g11,g2)
    c: PointOnObject(g11,g3)
    c: Tangent(g2,g10) = 1.5708
    c: Tangent(g3,g10) = 1.5708
    c: Coincident(g12,g2)
    c: Coincident(g12,g3)
    c: PointOnObject(g14,g0)
    c: PointOnObject(g14,g3)
    c: Tangent(g0,g13) = 1.5708
    c: Tangent(g3,g13) = 1.5708
    c: Coincident(g15,g0)
    c: Coincident(g15,g3)
    c: Equal(g6,g9)
    c: Equal(g9,g12)
    c: Equal(g12,g15)
    c: DistanceX(g14,g3) = 0.8
FEATURE [PartDesign::Pad] Pad030
  Direction = (0,-1,2e-16)
  Length = 25.2
  Length2 = 10
  Midplane = true
  Placement = pos=(0,0,0) rot=(1,0,0;1.5708rad)
  Profile = -> Sketch135
  ReferenceAxis = -> Sketch135 [N_Axis]
  Refine = true
  Suppressed = false
  Type = 0
FEATURE [PartDesign::Body] Body009  label="perno fermo switch - caricabatterie - grilletto"
  AllowCompound = false
  Group = -> [Sketch135,Pad030]
  Origin = -> Origin009
  Tip = -> Pad030
FEATURE [Sketcher::SketchObject] Sketch136  label="scavo_rele"
  ArcFitTolerance = 1e-06
  AttachmentSupport = -> [XZ_Plane]
  ExternalGeometry = -> [Sketch]
  FullyConstrained = true
  MakeInternals = false
  MapMode = 5
  Placement = pos=(0,0,0) rot=(1,0,0;1.5708rad)
  sketch-geometry (7):
    g0: LineSegment [constr] StartX=-173.013 StartY=-62.644 StartZ=0 EndX=-176.535 EndY=-73.4861 EndZ=0
    g1: LineSegment [constr] StartX=-173.013 StartY=-62.644 StartZ=0 EndX=-170.35 EndY=-63.5093 EndZ=0
    g2: LineSegment [constr] StartX=-173.013 StartY=-62.644 StartZ=0 EndX=-176.627 EndY=-61.4698 EndZ=0
    g3: LineSegment StartX=-176.627 StartY=-61.4698 StartZ=0 EndX=-170.35 EndY=-63.5093 EndZ=0
    g4: LineSegment StartX=-176.627 StartY=-61.4698 StartZ=0 EndX=-180.149 EndY=-72.3118 EndZ=0
    g5: LineSegment StartX=-170.35 StartY=-63.5093 StartZ=0 EndX=-173.872 EndY=-74.3513 EndZ=0
    g6: LineSegment StartX=-180.149 StartY=-72.3118 StartZ=0 EndX=-173.872 EndY=-74.3513 EndZ=0
  constraints (19):
    c: Tangent(g0,g-3)
    c: Distance(g0,g-3) = 89
    c: Distance(g0,g0) = 11.4
    c: Coincident(g1,g0)
    c: Coincident(g2,g0)
    c: Distance(g2) = 3.8
    c: Distance(g1) = 2.8
    c: Perpendicular(g0,g1)
    c: Perpendicular(g0,g2)
    c: Coincident(g3,g2)
    c: Coincident(g3,g1)
    c: Equal(g4,g0)
    c: Equal(g5,g0)
    c: Parallel(g4,g0)
    c: Parallel(g5,g0)
    c: Coincident(g4,g2)
    c: Coincident(g5,g1)
    c: Coincident(g6,g4)
    c: Coincident(g6,g5)
FEATURE [Part::Extrusion] Extrude076  label="Extrude076 - scavo_rele"
  Base = -> Sketch136
  Dir = (0,-1,2e-16)
  DirMode = 2
  FaceMakerClass = Part::FaceMakerBullseye
  FaceMakerMode = 3
  LengthFwd = 17.8
  LengthRev = 0
  Solid = true
  Symmetric = true
FEATURE [Sketcher::SketchObject] Sketch137  label="scavo_nuovo_driver"
  ArcFitTolerance = 1e-06
  AttachmentSupport = -> [XZ_Plane]
  ExternalGeometry = -> [Sketch]
  FullyConstrained = true
  MakeInternals = false
  MapMode = 5
  Placement = pos=(0,0,0) rot=(1,0,0;1.5708rad)
  sketch-geometry (7):
    g0: LineSegment [constr] StartX=-167.759 StartY=-46.4761 StartZ=0 EndX=-172.58 EndY=-61.3126 EndZ=0
    g1: LineSegment [constr] StartX=-167.759 StartY=-46.4761 StartZ=0 EndX=-165.477 EndY=-47.2177 EndZ=0
    g2: LineSegment [constr] StartX=-167.759 StartY=-46.4761 StartZ=0 EndX=-171.373 EndY=-45.3018 EndZ=0
    g3: LineSegment StartX=-171.373 StartY=-45.3018 StartZ=0 EndX=-165.477 EndY=-47.2177 EndZ=0
    g4: LineSegment StartX=-171.373 StartY=-45.3018 StartZ=0 EndX=-176.194 EndY=-60.1383 EndZ=0
    g5: LineSegment StartX=-165.477 StartY=-47.2177 StartZ=0 EndX=-170.297 EndY=-62.0542 EndZ=0
    g6: LineSegment StartX=-176.194 StartY=-60.1383 StartZ=0 EndX=-170.297 EndY=-62.0542 EndZ=0
  constraints (19):
    c: Distance(g0,g-3) = 72
    c: Distance(g0) = 15.6
    c: Tangent(g0,g-3)
    c: Coincident(g1,g0)
    c: Coincident(g2,g0)
    c: Distance(g1) = 2.4
    c: Distance(g2) = 3.8
    c: Perpendicular(g0,g1)
    c: Perpendicular(g0,g2)
    c: Coincident(g3,g2)
    c: Coincident(g3,g1)
    c: Equal(g4,g0)
    c: Equal(g5,g0)
    c: Parallel(g4,g0)
    c: Parallel(g5,g0)
    c: Coincident(g4,g2)
    c: Coincident(g5,g1)
    c: Coincident(g6,g4)
    c: Coincident(g6,g5)
FEATURE [Part::Extrusion] Extrude077  label="Extrude077 - scavo_nuovo_driver"
  Base = -> Sketch137
  Dir = (0,-1,2e-16)
  DirMode = 2
  FaceMakerClass = Part::FaceMakerBullseye
  FaceMakerMode = 3
  LengthFwd = 20.8
  LengthRev = 0
  Solid = true
  Symmetric = true
FEATURE [Sketcher::SketchObject] Sketch138  label="scavo_nuovo_driver_alto"
  ArcFitTolerance = 1e-06
  AttachmentSupport = -> [XZ_Plane]
  ExternalGeometry = -> [Sketch]
  FullyConstrained = true
  MakeInternals = false
  MapMode = 5
  Placement = pos=(0,0,0) rot=(1,0,0;1.5708rad)
  sketch-geometry (7):
    g0: LineSegment [constr] StartX=-188.796 StartY=17.7274 StartZ=0 EndX=-187.75 EndY=4.97025 EndZ=0
    g1: LineSegment StartX=-187.75 StartY=4.97025 StartZ=0 EndX=-189.743 EndY=4.8067 EndZ=0
    g2: LineSegment StartX=-187.75 StartY=4.97025 StartZ=0 EndX=-182.766 EndY=5.37913 EndZ=0
    g3: LineSegment StartX=-190.79 StartY=17.5638 StartZ=0 EndX=-189.743 EndY=4.8067 EndZ=0
    g4: LineSegment StartX=-183.813 StartY=18.1363 StartZ=0 EndX=-182.766 EndY=5.37913 EndZ=0
    g5: LineSegment StartX=-190.79 StartY=17.5638 StartZ=0 EndX=-188.796 EndY=17.7274 EndZ=0
    g6: LineSegment StartX=-188.796 StartY=17.7274 StartZ=0 EndX=-183.813 EndY=18.1363 EndZ=0
  constraints (20):
    c: Distance(g0) = 12.8
    c: DistanceY(g-3,g0) = 9
    c: PointOnObject(g0,g-4)
    c: PointOnObject(g0,g-4)
    c: Coincident(g1,g0)
    c: Coincident(g2,g0)
    c: Distance(g1) = 2
    c: Distance(g2) = 5
    c: Perpendicular(g0,g1)
    c: Perpendicular(g0,g2)
    c: Equal(g3,g0)
    c: Parallel(g3,g0)
    c: Coincident(g3,g1)
    c: Equal(g4,g0)
    c: Parallel(g4,g0)
    c: Coincident(g4,g2)
    c: Coincident(g5,g3)
    c: Coincident(g5,g0)
    c: Coincident(g6,g0)
    c: Coincident(g6,g4)
FEATURE [Part::Extrusion] Extrude078  label="Extrude078 - scavo_nuovo_driver_alto"
  Base = -> Sketch138
  Dir = (0,-1,2e-16)
  DirMode = 2
  FaceMakerClass = Part::FaceMakerBullseye
  FaceMakerMode = 3
  LengthFwd = 16.6
  LengthRev = 0
  Solid = true
  Symmetric = true
FEATURE [Sketcher::SketchObject] Sketch139  label="fermi_nuovo_driver_alto"
  ArcFitTolerance = 1e-06
  AttachmentSupport = -> [XZ_Plane]
  ExternalGeometry = -> [Sketch138,Sketch]
  FullyConstrained = true
  MakeInternals = false
  MapMode = 5
  Placement = pos=(0,0,0) rot=(1,0,0;1.5708rad)
  sketch-geometry (17):
    g0: LineSegment [constr] StartX=-188.314 StartY=16.4295 StartZ=0 EndX=-187.885 EndY=13.7638 EndZ=0
    g1: LineSegment [constr] StartX=-187.885 StartY=13.7638 StartZ=0 EndX=-187.456 EndY=11.0981 EndZ=0
    g2: LineSegment StartX=-187.885 StartY=13.7638 StartZ=0 EndX=-187.71 EndY=12.6778 EndZ=0
    g3: LineSegment StartX=-187.885 StartY=13.7638 StartZ=0 EndX=-188.06 EndY=14.8499 EndZ=0
    g4: LineSegment StartX=-187.71 StartY=12.6778 StartZ=0 EndX=-185.538 EndY=13.0274 EndZ=0
    g5: LineSegment StartX=-188.06 StartY=14.8499 StartZ=0 EndX=-185.888 EndY=15.1994 EndZ=0
    g6: LineSegment StartX=-185.888 StartY=15.1994 StartZ=0 EndX=-185.538 EndY=13.0274 EndZ=0
    g7: LineSegment StartX=-187.456 StartY=11.0981 StartZ=0 EndX=-189.035 EndY=10.8439 EndZ=0
    g8: LineSegment StartX=-188.314 StartY=16.4295 StartZ=0 EndX=-189.893 EndY=16.1753 EndZ=0
    g9: LineSegment StartX=-189.893 StartY=16.1753 StartZ=0 EndX=-189.035 EndY=10.8439 EndZ=0
    g10: LineSegment StartX=-187.456 StartY=11.0981 StartZ=0 EndX=-185.284 EndY=11.4477 EndZ=0
    g11: LineSegment StartX=-188.314 StartY=16.4295 StartZ=0 EndX=-186.142 EndY=16.7791 EndZ=0
    g12: LineSegment StartX=-184.308 StartY=15.4537 StartZ=0 EndX=-183.958 EndY=13.2816 EndZ=0
    g13: ArcOfCircle CenterX=-185.888 CenterY=15.1994 CenterZ=0 NormalX=0 NormalY=0 NormalZ=1 AngleXU=0 Radius=1.6 StartAngle=0.15957 EndAngle=1.73037
    g14: GeomPoint [constr] X=-184.562 Y=17.0333 Z=0
    g15: ArcOfCircle CenterX=-185.538 CenterY=13.0274 CenterZ=0 NormalX=0 NormalY=0 NormalZ=1 AngleXU=0 Radius=1.6 StartAngle=4.87196 EndAngle=6.44276
    g16: GeomPoint [constr] X=-183.704 Y=11.7019 Z=0
  constraints (43):
    c: Tangent(g1,g0) = -1.5708
    c: Distance(g0) = 2.7
    c: Equal(g1,g0)
    c: Tangent(g1,g-5)
    c: Coincident(g2,g0)
    c: Coincident(g3,g0)
    c: Distance(g2) = 1.1
    c: Equal(g3,g2)
    c: PointOnObject(g3,g2)
    c: Coincident(g4,g2)
    c: Coincident(g5,g3)
    c: Distance(g4) = 2.2
    c: Equal(g4,g5)
    c: Perpendicular(g1,g4)
    c: Perpendicular(g0,g5)
    c: Coincident(g6,g5)
    c: Coincident(g6,g4)
    c: Coincident(g7,g1)
    c: Coincident(g8,g0)
    c: Distance(g7) = 1.6
    c: Equal(g7,g8)
    c: Perpendicular(g1,g7)
    c: Perpendicular(g8,g0)
    c: Coincident(g9,g8)
    c: Coincident(g9,g7)
    c: Coincident(g10,g1)
    c: Coincident(g11,g0)
    c: Distance(g10,g16) = 3.8
    c: Perpendicular(g1,g10)
    c: Perpendicular(g1,g11)
    c: DistanceY(g0,g-4) = 3.8
    c: PointOnObject(g14,g12)
    c: PointOnObject(g14,g11)
    c: Tangent(g12,g13) = 1.5708
    c: Tangent(g11,g13) = 1.5708
    c: PointOnObject(g16,g12)
    c: PointOnObject(g16,g10)
    c: Tangent(g12,g15) = 1.5708
    c: Tangent(g10,g15) = -1.5708
    c: Equal(g13,g15)
    c: Coincident(g13,g5)
    c: Parallel(g2,g0)
    c: PointOnObject(g0,g-5)
FEATURE [Part::Extrusion] Extrude079  label="Extrude079 - fermi_nuovo_driver_alto"
  Base = -> Sketch139
  Dir = (0,-1,2e-16)
  DirMode = 2
  FaceMakerClass = Part::FaceMakerBullseye
  FaceMakerMode = 3
  LengthFwd = 25.2
  LengthRev = 0
  Solid = true
  Symmetric = true
FEATURE [Sketcher::SketchObject] Sketch140  label="scavo_diodo_nuovo_driver_alto"
  ArcFitTolerance = 1e-06
  AttachmentSupport = -> [XZ_Plane]
  ExternalGeometry = -> [Sketch138]
  FullyConstrained = true
  MakeInternals = false
  MapMode = 5
  Placement = pos=(0,0,0) rot=(1,0,0;1.5708rad)
  sketch-geometry (4):
    g0: LineSegment StartX=-190.79 StartY=17.5638 StartZ=0 EndX=-189.743 EndY=4.8067 EndZ=0
    g1: LineSegment StartX=-193.78 StartY=17.3185 StartZ=0 EndX=-192.733 EndY=4.56137 EndZ=0
    g2: LineSegment StartX=-190.79 StartY=17.5638 StartZ=0 EndX=-193.78 EndY=17.3185 EndZ=0
    g3: LineSegment StartX=-192.733 StartY=4.56137 StartZ=0 EndX=-189.743 EndY=4.8067 EndZ=0
  constraints (11):
    c: Equal(g0,g-3)
    c: Parallel(g0,g-3)
    c: Equal(g1,g-3)
    c: Parallel(g1,g-3)
    c: Coincident(g2,g0)
    c: Distance(g2) = 3
    c: Perpendicular(g0,g2)
    c: Coincident(g1,g2)
    c: Coincident(g3,g1)
    c: Coincident(g3,g0)
    c: Coincident(g0,g-3)
FEATURE [Part::Extrusion] Extrude080  label="Extrude080 - scavo_diodo_nuovo_driver_alto"
  Base = -> Sketch140
  Dir = (0,-1,2e-16)
  DirMode = 2
  FaceMakerClass = Part::FaceMakerBullseye
  FaceMakerMode = 3
  LengthFwd = 4
  LengthRev = 0
  Placement = pos=(0,7.8,0) rot=(0,0,1;0rad)
  Solid = true
  Symmetric = false
FEATURE [Part::MultiFuse] Fusion001
  Refine = true
  Shapes = -> [Cut043,Extrude079]
FEATURE [Part::Cut] Cut044
  Base = -> Fusion001
  Refine = true
  Tool = -> Extrude078
FEATURE [Part::Cut] Cut045
  Base = -> Cut044
  Refine = true
  Tool = -> Extrude080
FEATURE [Sketcher::SketchObject] Sketch141  label="fermi_nuovo_driver"
  ArcFitTolerance = 1e-06
  AttachmentSupport = -> [XZ_Plane]
  ExternalGeometry = -> [Sketch,Sketch137]
  FullyConstrained = true
  MakeInternals = false
  MapMode = 5
  Placement = pos=(0,0,0) rot=(1,0,0;1.5708rad)
  sketch-geometry (16):
    g0: LineSegment [constr] StartX=-165.477 StartY=-47.2177 StartZ=0 EndX=-167.759 EndY=-46.4761 EndZ=0
    g1: LineSegment [constr] StartX=-167.759 StartY=-46.4761 StartZ=0 EndX=-168.006 EndY=-47.2369 EndZ=0
    g2: LineSegment [constr] StartX=-168.006 StartY=-47.2369 StartZ=0 EndX=-169.675 EndY=-52.3726 EndZ=0
    g3: LineSegment StartX=-169.675 StartY=-52.3726 StartZ=0 EndX=-171.767 EndY=-51.6928 EndZ=0
    g4: LineSegment StartX=-172.795 StartY=-49.6767 StartZ=0 EndX=-172.115 EndY=-47.5843 EndZ=0
    g5: LineSegment StartX=-170.099 StartY=-46.5571 StartZ=0 EndX=-166.485 EndY=-47.7313 EndZ=0
    g6: LineSegment StartX=-166.485 StartY=-47.7313 StartZ=0 EndX=-168.153 EndY=-52.867 EndZ=0
    g7: LineSegment StartX=-169.675 StartY=-52.3726 StartZ=0 EndX=-168.153 EndY=-52.867 EndZ=0
    g8: LineSegment StartX=-170.593 StartY=-48.0788 StartZ=0 EndX=-171.273 EndY=-50.1711 EndZ=0
    g9: LineSegment StartX=-171.273 StartY=-50.1711 StartZ=0 EndX=-169.181 EndY=-50.8509 EndZ=0
    g10: LineSegment StartX=-169.181 StartY=-50.8509 StartZ=0 EndX=-168.501 EndY=-48.7586 EndZ=0
    g11: LineSegment StartX=-168.501 StartY=-48.7586 StartZ=0 EndX=-170.593 EndY=-48.0788 EndZ=0
    g12: ArcOfCircle CenterX=-170.593 CenterY=-48.0788 CenterZ=0 NormalX=0 NormalY=0 NormalZ=1 AngleXU=0 Radius=1.6 StartAngle=1.25664 EndAngle=2.82743
    g13: GeomPoint [constr] X=-171.62 Y=-46.0626 Z=0
    g14: ArcOfCircle CenterX=-171.273 CenterY=-50.1711 CenterZ=0 NormalX=0 NormalY=0 NormalZ=1 AngleXU=0 Radius=1.6 StartAngle=2.82743 EndAngle=4.39823
    g15: GeomPoint [constr] X=-173.289 Y=-51.1984 Z=0
  constraints (41):
    c: Coincident(g0,g-4)
    c: PointOnObject(g0,g-3)
    c: Parallel(g0,g-4)
    c: Coincident(g1,g0)
    c: Parallel(g1,g-3)
    c: Distance(g1) = 0.8
    c: Coincident(g2,g1)
    c: Distance(g2) = 5.4
    c: Coincident(g3,g2)
    c: Parallel(g2,g-3)
    c: Distance(g15,g13) = 5.4
    c: Perpendicular(g3,g2)
    c: Parallel(g4,g2)
    c: Distance(g5,g13) = 5.4
    c: Distance(g3,g15) = 3.8
    c: Perpendicular(g4,g5)
    c: Coincident(g6,g5)
    c: Distance(g6) = 5.4
    c: Parallel(g6,g4)
    c: Coincident(g7,g2)
    c: Coincident(g7,g6)
    c: Coincident(g8,g9)
    c: Coincident(g9,g10)
    c: Coincident(g10,g11)
    c: Coincident(g11,g8)
    c: Distance(g8,g10) = 2.2
    c: Distance(g9,g11) = 2.2
    c: Perpendicular(g11,g8)
    c: Equal(g8,g10)
    c: Equal(g11,g9)
    c: Tangent(g10,g2)
    c: Distance(g10,g1) = 1.6
    c: PointOnObject(g13,g4)
    c: PointOnObject(g13,g5)
    c: Tangent(g4,g12) = 1.5708
    c: Tangent(g5,g12) = 1.5708
    c: PointOnObject(g15,g4)
    c: Tangent(g4,g14) = 1.5708
    c: Tangent(g3,g14) = 1.5708
    c: Equal(g14,g12)
    c: Coincident(g12,g8)
FEATURE [Part::Extrusion] Extrude081  label="Extrude081 - fermi_nuovo_driver"
  Base = -> Sketch141
  Dir = (0,-1,2e-16)
  DirMode = 2
  FaceMakerClass = Part::FaceMakerBullseye
  FaceMakerMode = 3
  LengthFwd = 25.2
  LengthRev = 0
  Solid = true
  Symmetric = true
FEATURE [Part::MultiFuse] Fusion002
  Refine = true
  Shapes = -> [Cut045,Extrude081]
FEATURE [Part::Cut] Cut046
  Base = -> Fusion002
  Refine = true
  Tool = -> Extrude077
FEATURE [Sketcher::SketchObject] Sketch142  label="fermi_rele"
  ArcFitTolerance = 1e-06
  AttachmentSupport = -> [XZ_Plane]
  ExternalGeometry = -> [Sketch,Sketch136]
  FullyConstrained = true
  MakeInternals = false
  MapMode = 5
  Placement = pos=(0,0,0) rot=(1,0,0;1.5708rad)
  sketch-geometry (15):
    g0: LineSegment StartX=-177.245 StartY=-63.3719 StartZ=0 EndX=-177.924 EndY=-65.4642 EndZ=0
    g1: LineSegment StartX=-175.228 StartY=-62.3446 StartZ=0 EndX=-171.614 EndY=-63.5189 EndZ=0
    g2: LineSegment StartX=-171.614 StartY=-63.5189 StartZ=0 EndX=-173.283 EndY=-68.6546 EndZ=0
    g3: LineSegment StartX=-176.897 StartY=-67.4803 StartZ=0 EndX=-173.283 EndY=-68.6546 EndZ=0
    g4: LineSegment StartX=-175.723 StartY=-63.8663 StartZ=0 EndX=-173.631 EndY=-64.5461 EndZ=0
    g5: LineSegment StartX=-175.723 StartY=-63.8663 StartZ=0 EndX=-176.403 EndY=-65.9586 EndZ=0
    g6: LineSegment StartX=-173.631 StartY=-64.5461 StartZ=0 EndX=-174.31 EndY=-66.6385 EndZ=0
    g7: LineSegment StartX=-176.403 StartY=-65.9586 StartZ=0 EndX=-174.31 EndY=-66.6385 EndZ=0
    g8: LineSegment [constr] StartX=-173.631 StartY=-64.5461 StartZ=0 EndX=-173.136 EndY=-63.0245 EndZ=0
    g9: LineSegment [constr] StartX=-173.631 StartY=-64.5461 StartZ=0 EndX=-172.109 EndY=-65.0406 EndZ=0
    g10: LineSegment [constr] StartX=-170.35 StartY=-63.5093 StartZ=0 EndX=-173.013 EndY=-62.644 EndZ=0
    g11: ArcOfCircle CenterX=-175.723 CenterY=-63.8663 CenterZ=0 NormalX=0 NormalY=0 NormalZ=1 AngleXU=0 Radius=1.6 StartAngle=1.25664 EndAngle=2.82743
    g12: GeomPoint [constr] X=-176.75 Y=-61.8502 Z=0
    g13: ArcOfCircle CenterX=-176.403 CenterY=-65.9586 CenterZ=0 NormalX=0 NormalY=0 NormalZ=1 AngleXU=0 Radius=1.6 StartAngle=2.82743 EndAngle=4.39823
    g14: GeomPoint [constr] X=-178.419 Y=-66.9859 Z=0
  constraints (39):
    c: Distance(g14,g12) = 5.4
    c: Distance(g1,g12) = 5.4
    c: Perpendicular(g1,g0)
    c: Coincident(g2,g1)
    c: Parallel(g2,g0)
    c: Coincident(g3,g2)
    c: Parallel(g2,g-3)
    c: Coincident(g5,g4)
    c: Distance(g5) = 2.2
    c: Distance(g4) = 2.2
    c: Perpendicular(g4,g5)
    c: Coincident(g6,g4)
    c: Equal(g6,g5)
    c: Parallel(g6,g5)
    c: Coincident(g7,g5)
    c: Coincident(g7,g6)
    c: Coincident(g8,g4)
    c: Coincident(g9,g4)
    c: Distance(g8) = 1.6
    c: Distance(g9) = 1.6
    c: Parallel(g8,g6)
    c: Parallel(g9,g4)
    c: PointOnObject(g8,g1)
    c: PointOnObject(g9,g2)
    c: Coincident(g10,g-4)
    c: Parallel(g10,g-4)
    c: PointOnObject(g10,g-3)
    c: Tangent(g6,g-3) = 1.5708
    c: Distance(g4,g10) = 2
    c: PointOnObject(g12,g1)
    c: Tangent(g1,g11) = 1.5708
    c: Tangent(g0,g11) = -1.5708
    c: PointOnObject(g14,g3)
    c: PointOnObject(g14,g0)
    c: Tangent(g3,g13) = -1.5708
    c: Tangent(g0,g13) = -1.5708
    c: Equal(g11,g13)
    c: Coincident(g11,g4)
    c: Parallel(g3,g1)
FEATURE [Part::Extrusion] Extrude082  label="Extrude082 - fermi_rele"
  Base = -> Sketch142
  Dir = (0,-1,2e-16)
  DirMode = 2
  FaceMakerClass = Part::FaceMakerBullseye
  FaceMakerMode = 3
  LengthFwd = 25.2
  LengthRev = 0
  Solid = true
  Symmetric = true
FEATURE [Part::MultiFuse] Fusion003
  Refine = true
  Shapes = -> [Cut046,Extrude082]
FEATURE [Part::Cut] Cut047
  Base = -> Fusion003
  Refine = true
  Tool = -> Extrude076
FEATURE [Sketcher::SketchObject] Sketch143  label="foro_passaggio_cavi_led_batteria"
  ArcFitTolerance = 1e-06
  AttachmentSupport = -> [XZ_Plane]
  ExternalGeometry = -> [Sketch,Sketch042,Sketch036]
  FullyConstrained = true
  MakeInternals = false
  MapMode = 5
  Placement = pos=(0,0,0) rot=(1,0,0;1.5708rad)
  sketch-geometry (4):
    g0: LineSegment StartX=-207.775 StartY=-41.3701 StartZ=0 EndX=-213.607 EndY=-53.8767 EndZ=0
    g1: LineSegment StartX=-213.607 StartY=-53.8767 StartZ=0 EndX=-211.843 EndY=-59.5559 EndZ=0
    g2: LineSegment StartX=-207.775 StartY=-41.3701 StartZ=0 EndX=-207.775 EndY=-50.8316 EndZ=0
    g3: LineSegment StartX=-207.775 StartY=-50.8316 StartZ=0 EndX=-211.843 EndY=-59.5559 EndZ=0
  constraints (9):
    c: Coincident(g0,g-3)
    c: PointOnObject(g1,g-6)
    c: Coincident(g1,g0)
    c: Coincident(g2,g0)
    c: Coincident(g2,g-7)
    c: Coincident(g3,g2)
    c: Parallel(g3,g0)
    c: Coincident(g3,g1)
    c: Coincident(g0,g-5)
FEATURE [Part::Extrusion] Extrude083  label="Extrude083 - foro_passaggio_cavi_led_batteria"
  Base = -> Sketch143
  Dir = (0,-1,2e-16)
  DirMode = 2
  FaceMakerClass = Part::FaceMakerBullseye
  FaceMakerMode = 3
  LengthFwd = 6
  LengthRev = 0
  Solid = true
  Symmetric = true
FEATURE [Part::Cut] Cut048
  Base = -> Cut047
  Refine = true
  Tool = -> Extrude083
FEATURE [Sketcher::SketchObject] Sketch144  label="foro_areazione_alimentatore"
  ArcFitTolerance = 1e-06
  AttachmentSupport = -> [XZ_Plane]
  ExternalGeometry = -> [Sketch036]
  FullyConstrained = true
  MakeInternals = false
  MapMode = 5
  Placement = pos=(0,0,0) rot=(1,0,0;1.5708rad)
  sketch-geometry (4):
    g0: LineSegment StartX=-211.843 StartY=-60.3701 StartZ=0 EndX=-207.775 EndY=-60.3701 EndZ=0
    g1: LineSegment StartX=-207.775 StartY=-60.3701 StartZ=0 EndX=-207.775 EndY=-70.3701 EndZ=0
    g2: LineSegment StartX=-211.843 StartY=-60.3701 StartZ=0 EndX=-211.843 EndY=-70.3701 EndZ=0
    g3: LineSegment StartX=-207.775 StartY=-70.3701 StartZ=0 EndX=-211.843 EndY=-70.3701 EndZ=0
  constraints (11):
    c: Horizontal(g0)
    c: Distance(g1) = 10
    c: Coincident(g1,g0)
    c: Tangent(g1,g-3)
    c: PointOnObject(g0,g-4)
    c: Coincident(g2,g0)
    c: PointOnObject(g2,g-4)
    c: Coincident(g3,g1)
    c: Horizontal(g3)
    c: Coincident(g3,g2)
    c: DistanceY(g0,g-3) = 19
FEATURE [Part::Extrusion] Extrude084  label="Extrude084 - foro_areazione_alimentatore"
  Base = -> Sketch144
  Dir = (0,-1,2e-16)
  DirMode = 2
  FaceMakerClass = Part::FaceMakerBullseye
  FaceMakerMode = 3
  LengthFwd = 10
  LengthRev = 0
  Solid = true
  Symmetric = true
FEATURE [Part::Cut] Cut049
  Base = -> Cut048
  Refine = true
  Tool = -> Extrude084
FEATURE [Sketcher::SketchObject] Sketch145  label="foro_per_condesatore"
  ArcFitTolerance = 1e-06
  AttachmentSupport = -> [XZ_Plane]
  ExternalGeometry = -> [Sketch,Sketch139]
  FullyConstrained = true
  MakeInternals = false
  MapMode = 5
  Placement = pos=(0,0,0) rot=(1,0,0;1.5708rad)
  sketch-geometry (1):
    g0: Circle CenterX=-182.345 CenterY=7.02342 CenterZ=0 NormalX=0 NormalY=0 NormalZ=1 AngleXU=0 Radius=5.2
  constraints (3):
    c: Diameter(g0) = 10.4
    c: Tangent(g0,g-3)
    c: Tangent(g0,g-4)
FEATURE [Part::Extrusion] Extrude085  label="Extrude085 - foro_per_condesatore"
  Base = -> Sketch145
  Dir = (0,-1,2e-16)
  DirMode = 2
  FaceMakerClass = Part::FaceMakerBullseye
  FaceMakerMode = 3
  LengthFwd = 25.2
  LengthRev = 0
  Solid = true
  Symmetric = true
FEATURE [Part::Cut] Cut050
  Base = -> Cut049
  Refine = true
  Tool = -> Extrude085
FEATURE [Sketcher::SketchObject] Sketch146  label="scavo_pulsante_6x6_per_led_batteria"
  ArcFitTolerance = 1e-06
  AttachmentSupport = -> [XZ_Plane]
  ExternalGeometry = -> [Sketch036,Sketch016]
  FullyConstrained = true
  MakeInternals = false
  MapMode = 5
  Placement = pos=(0,0,0) rot=(1,0,0;1.5708rad)
  sketch-geometry (4):
    g0: LineSegment StartX=-217.243 StartY=-66.0316 StartZ=0 EndX=-217.243 EndY=-72.8316 EndZ=0
    g1: LineSegment StartX=-217.243 StartY=-72.8316 StartZ=0 EndX=-211.043 EndY=-72.8316 EndZ=0
    g2: LineSegment StartX=-211.043 StartY=-72.8316 StartZ=0 EndX=-211.043 EndY=-66.0316 EndZ=0
    g3: LineSegment StartX=-211.043 StartY=-66.0316 StartZ=0 EndX=-217.243 EndY=-66.0316 EndZ=0
  constraints (12):
    c: Coincident(g0,g1)
    c: Coincident(g1,g2)
    c: Coincident(g2,g3)
    c: Coincident(g3,g0)
    c: Vertical(g0)
    c: Vertical(g2)
    c: Horizontal(g1)
    c: Horizontal(g3)
    c: Distance(g0,g2) = 6.2
    c: Distance(g1,g3) = 6.8
    c: Tangent(g1,g-4)
    c: DistanceX(g-3,g1) = 0.8
FEATURE [Part::Extrusion] Extrude086  label="Extrude086 - scavo_pulsante_6x6_per_led_batteria"
  Base = -> Sketch146
  Dir = (0,-1,2e-16)
  DirMode = 2
  FaceMakerClass = Part::FaceMakerBullseye
  FaceMakerMode = 3
  LengthFwd = 4.2
  LengthRev = 0
  Placement = pos=(0,12.6,0) rot=(0,0,1;0rad)
  Solid = true
  Symmetric = false
FEATURE [Sketcher::SketchObject] Sketch147  label="scavo_led_stato_batteria"
  ArcFitTolerance = 1e-06
  AttachmentSupport = -> [XZ_Plane]
  ExternalGeometry = -> [Sketch036,Sketch146]
  FullyConstrained = true
  MakeInternals = false
  MapMode = 5
  Placement = pos=(0,0,0) rot=(1,0,0;1.5708rad)
  sketch-geometry (4):
    g0: LineSegment StartX=-215.643 StartY=-55.6944 StartZ=0 EndX=-215.643 EndY=-64.8944 EndZ=0
    g1: LineSegment StartX=-215.643 StartY=-64.8944 StartZ=0 EndX=-211.043 EndY=-64.8944 EndZ=0
    g2: LineSegment StartX=-211.043 StartY=-64.8944 StartZ=0 EndX=-211.043 EndY=-55.6944 EndZ=0
    g3: LineSegment StartX=-211.043 StartY=-55.6944 StartZ=0 EndX=-215.643 EndY=-55.6944 EndZ=0
  constraints (12):
    c: Coincident(g0,g1)
    c: Coincident(g1,g2)
    c: Coincident(g2,g3)
    c: Coincident(g3,g0)
    c: Vertical(g0)
    c: Vertical(g2)
    c: Horizontal(g1)
    c: Horizontal(g3)
    c: Distance(g0,g2) = 4.6
    c: Distance(g1,g3) = 9.2
    c: DistanceY(g2,g-3) = 5.6
    c: DistanceX(g2,g-4) = 0
FEATURE [PartDesign::Body] Body  label="Struttura pistola"
  AllowCompound = false
  Group = -> [Sketch,Sketch002,Sketch004,DatumPlane,Sketch005,DatumPlane001,CopyCut,Sketch008,Sketch009,Sketch010,Sketch011,Sketch012,Sketch013,Sketch014,Sketch015,Sketch016,Sketch017,Sketch018,Sketch019,Sketch020,Sketch022,Sketch023,Sketch024,Sketch025,Sketch026,Sketch027,Sketch029,Sketch030,Sketch031,Sketch032,Sketch033,Sketch034,Sketch035,Sketch036,Sketch037,Sketch038,Sketch039,Sketch040,Sketch041,Sketch042,+27 more]
  Origin = -> Origin
FEATURE [Part::Extrusion] Extrude087  label="Extrude087 - scavo_led_stato_batteria"
  Base = -> Sketch147
  Dir = (0,-1,2e-16)
  DirMode = 2
  FaceMakerClass = Part::FaceMakerBullseye
  FaceMakerMode = 3
  LengthFwd = 2
  LengthRev = 0
  Placement = pos=(0,12.6,0) rot=(0,0,1;0rad)
  Solid = true
  Symmetric = false
FEATURE [Part::Cut] Cut051
  Base = -> Cut050
  Refine = true
  Tool = -> Extrude086
FEATURE [Part::Cut] Cut052
  Base = -> Cut051
  Refine = true
  Tool = -> Extrude087
note: 2 file-system paths scrubbed to <path> (originals preserved in the JSON sidecar)
